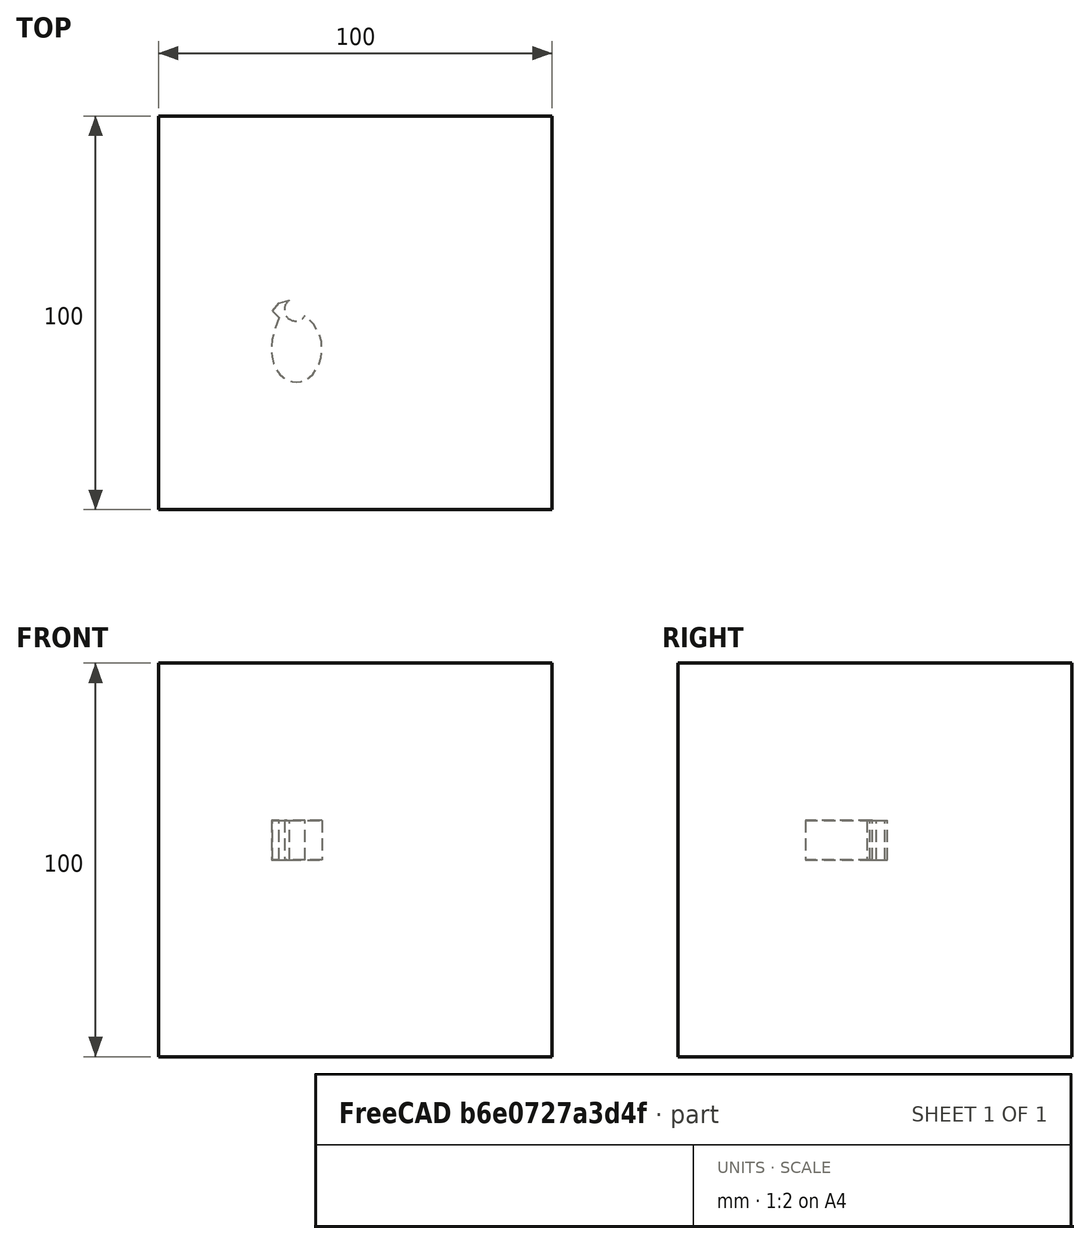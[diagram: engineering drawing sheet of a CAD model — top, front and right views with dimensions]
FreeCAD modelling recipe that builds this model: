
FCSTD DOCUMENT  (FreeCAD 0.19RUnknown)
Label: mirrorTest-1c
License: All rights reserved
LicenseURL: http://en.wikipedia.org/wiki/All_rights_reserved
objects: App::DocumentObjectGroupPython×1248, App::Part×2, Part::FeaturePython×1, Sketcher::SketchObject×1, Part::Extrusion×1, Part::Mirroring×1
note: 4 computed .brp shape members not serialized (recipe doc carries the construction recipe); baked Part::Feature solids carry a one-line shape summary decoded from their .brp

FEATURE [App::DocumentObjectGroupPython] HALFPI  # scripted group (container) (typed FeaturePython)
  name = HALFPI
  value = pi/2.
FEATURE [App::DocumentObjectGroupPython] PI  # scripted group (container) (typed FeaturePython)
  name = PI
  value = 1.*pi
FEATURE [App::DocumentObjectGroupPython] TWOPI  # scripted group (container) (typed FeaturePython)
  name = TWOPI
  value = 2.*pi
FEATURE [App::DocumentObjectGroupPython] Constants  # scripted group (container) (typed FeaturePython)
  Group = -> [HALFPI,PI,TWOPI]
FEATURE [App::DocumentObjectGroupPython] Variables  # scripted group (container) (typed FeaturePython)
FEATURE [App::DocumentObjectGroupPython] Quantities  # scripted group (container) (typed FeaturePython)
FEATURE [App::DocumentObjectGroupPython] Isotopes  # scripted group (container) (typed FeaturePython)
FEATURE [App::DocumentObjectGroupPython] Elements  # scripted group (container) (typed FeaturePython)
FEATURE [App::DocumentObjectGroupPython] G4Isotopes  # scripted group (container) (typed FeaturePython)
FEATURE [App::DocumentObjectGroupPython] H_element  # scripted group (container) (typed FeaturePython)
  Z = 1
  atom_value = 1.008
  formula = H
  name = H_element
FEATURE [App::DocumentObjectGroupPython] He_element  # scripted group (container) (typed FeaturePython)
  Z = 2
  atom_value = 4.0026
  formula = He
  name = He_element
FEATURE [App::DocumentObjectGroupPython] Li_element  # scripted group (container) (typed FeaturePython)
  Z = 3
  atom_value = 6.94
  formula = Li
  name = Li_element
FEATURE [App::DocumentObjectGroupPython] Be_element  # scripted group (container) (typed FeaturePython)
  Z = 4
  atom_value = 9.01218
  formula = Be
  name = Be_element
FEATURE [App::DocumentObjectGroupPython] B_element  # scripted group (container) (typed FeaturePython)
  Z = 5
  atom_value = 10.81
  formula = B
  name = B_element
FEATURE [App::DocumentObjectGroupPython] C_element  # scripted group (container) (typed FeaturePython)
  Z = 6
  atom_value = 12.011
  formula = C
  name = C_element
FEATURE [App::DocumentObjectGroupPython] N_element  # scripted group (container) (typed FeaturePython)
  Z = 7
  atom_value = 14.007
  formula = N
  name = N_element
FEATURE [App::DocumentObjectGroupPython] O_element  # scripted group (container) (typed FeaturePython)
  Z = 8
  atom_value = 15.999
  formula = O
  name = O_element
FEATURE [App::DocumentObjectGroupPython] F_element  # scripted group (container) (typed FeaturePython)
  Z = 9
  atom_value = 18.9984
  formula = F
  name = F_element
FEATURE [App::DocumentObjectGroupPython] Ne_element  # scripted group (container) (typed FeaturePython)
  Z = 10
  atom_value = 20.1797
  formula = Ne
  name = Ne_element
FEATURE [App::DocumentObjectGroupPython] Na_element  # scripted group (container) (typed FeaturePython)
  Z = 11
  atom_value = 22.9898
  formula = Na
  name = Na_element
FEATURE [App::DocumentObjectGroupPython] Mg_element  # scripted group (container) (typed FeaturePython)
  Z = 12
  atom_value = 24.305
  formula = Mg
  name = Mg_element
FEATURE [App::DocumentObjectGroupPython] Al_element  # scripted group (container) (typed FeaturePython)
  Z = 13
  atom_value = 26.9815
  formula = Al
  name = Al_element
FEATURE [App::DocumentObjectGroupPython] Si_element  # scripted group (container) (typed FeaturePython)
  Z = 14
  atom_value = 28.085
  formula = Si
  name = Si_element
FEATURE [App::DocumentObjectGroupPython] P_element  # scripted group (container) (typed FeaturePython)
  Z = 15
  atom_value = 30.9738
  formula = P
  name = P_element
FEATURE [App::DocumentObjectGroupPython] S_element  # scripted group (container) (typed FeaturePython)
  Z = 16
  atom_value = 32.06
  formula = S
  name = S_element
FEATURE [App::DocumentObjectGroupPython] Cl_element  # scripted group (container) (typed FeaturePython)
  Z = 17
  atom_value = 35.45
  formula = Cl
  name = Cl_element
FEATURE [App::DocumentObjectGroupPython] Ar_element  # scripted group (container) (typed FeaturePython)
  Z = 18
  atom_value = 39.95
  formula = Ar
  name = Ar_element
FEATURE [App::DocumentObjectGroupPython] K_element  # scripted group (container) (typed FeaturePython)
  Z = 19
  atom_value = 39.0983
  formula = K
  name = K_element
FEATURE [App::DocumentObjectGroupPython] Ca_element  # scripted group (container) (typed FeaturePython)
  Z = 20
  atom_value = 40.078
  formula = Ca
  name = Ca_element
FEATURE [App::DocumentObjectGroupPython] Sc_element  # scripted group (container) (typed FeaturePython)
  Z = 21
  atom_value = 44.9559
  formula = Sc
  name = Sc_element
FEATURE [App::DocumentObjectGroupPython] Ti_element  # scripted group (container) (typed FeaturePython)
  Z = 22
  atom_value = 47.867
  formula = Ti
  name = Ti_element
FEATURE [App::DocumentObjectGroupPython] V_element  # scripted group (container) (typed FeaturePython)
  Z = 23
  atom_value = 50.9415
  formula = V
  name = V_element
FEATURE [App::DocumentObjectGroupPython] Cr_element  # scripted group (container) (typed FeaturePython)
  Z = 24
  atom_value = 51.9961
  formula = Cr
  name = Cr_element
FEATURE [App::DocumentObjectGroupPython] Mn_element  # scripted group (container) (typed FeaturePython)
  Z = 25
  atom_value = 54.938
  formula = Mn
  name = Mn_element
FEATURE [App::DocumentObjectGroupPython] Fe_element  # scripted group (container) (typed FeaturePython)
  Z = 26
  atom_value = 55.845
  formula = Fe
  name = Fe_element
FEATURE [App::DocumentObjectGroupPython] Co_element  # scripted group (container) (typed FeaturePython)
  Z = 27
  atom_value = 58.9332
  formula = Co
  name = Co_element
FEATURE [App::DocumentObjectGroupPython] Ni_element  # scripted group (container) (typed FeaturePython)
  Z = 28
  atom_value = 58.6934
  formula = Ni
  name = Ni_element
FEATURE [App::DocumentObjectGroupPython] Cu_element  # scripted group (container) (typed FeaturePython)
  Z = 29
  atom_value = 63.546
  formula = Cu
  name = Cu_element
FEATURE [App::DocumentObjectGroupPython] Zn_element  # scripted group (container) (typed FeaturePython)
  Z = 30
  atom_value = 65.38
  formula = Zn
  name = Zn_element
FEATURE [App::DocumentObjectGroupPython] Ga_element  # scripted group (container) (typed FeaturePython)
  Z = 31
  atom_value = 69.723
  formula = Ga
  name = Ga_element
FEATURE [App::DocumentObjectGroupPython] Ge_element  # scripted group (container) (typed FeaturePython)
  Z = 32
  atom_value = 72.63
  formula = Ge
  name = Ge_element
FEATURE [App::DocumentObjectGroupPython] As_element  # scripted group (container) (typed FeaturePython)
  Z = 33
  atom_value = 74.9216
  formula = As
  name = As_element
FEATURE [App::DocumentObjectGroupPython] Se_element  # scripted group (container) (typed FeaturePython)
  Z = 34
  atom_value = 78.971
  formula = Se
  name = Se_element
FEATURE [App::DocumentObjectGroupPython] Br_element  # scripted group (container) (typed FeaturePython)
  Z = 35
  atom_value = 79.904
  formula = Br
  name = Br_element
FEATURE [App::DocumentObjectGroupPython] Kr_element  # scripted group (container) (typed FeaturePython)
  Z = 36
  atom_value = 83.798
  formula = Kr
  name = Kr_element
FEATURE [App::DocumentObjectGroupPython] Rb_element  # scripted group (container) (typed FeaturePython)
  Z = 37
  atom_value = 85.4678
  formula = Rb
  name = Rb_element
FEATURE [App::DocumentObjectGroupPython] Sr_element  # scripted group (container) (typed FeaturePython)
  Z = 38
  atom_value = 87.62
  formula = Sr
  name = Sr_element
FEATURE [App::DocumentObjectGroupPython] Y_element  # scripted group (container) (typed FeaturePython)
  Z = 39
  atom_value = 88.9058
  formula = Y
  name = Y_element
FEATURE [App::DocumentObjectGroupPython] Zr_element  # scripted group (container) (typed FeaturePython)
  Z = 40
  atom_value = 91.224
  formula = Zr
  name = Zr_element
FEATURE [App::DocumentObjectGroupPython] Nb_element  # scripted group (container) (typed FeaturePython)
  Z = 41
  atom_value = 92.9064
  formula = Nb
  name = Nb_element
FEATURE [App::DocumentObjectGroupPython] Mo_element  # scripted group (container) (typed FeaturePython)
  Z = 42
  atom_value = 95.95
  formula = Mo
  name = Mo_element
FEATURE [App::DocumentObjectGroupPython] Tc_element  # scripted group (container) (typed FeaturePython)
  Z = 43
  atom_value = 97
  formula = Tc
  name = Tc_element
FEATURE [App::DocumentObjectGroupPython] Ru_element  # scripted group (container) (typed FeaturePython)
  Z = 44
  atom_value = 101.07
  formula = Ru
  name = Ru_element
FEATURE [App::DocumentObjectGroupPython] Rh_element  # scripted group (container) (typed FeaturePython)
  Z = 45
  atom_value = 102.905
  formula = Rh
  name = Rh_element
FEATURE [App::DocumentObjectGroupPython] Pd_element  # scripted group (container) (typed FeaturePython)
  Z = 46
  atom_value = 106.42
  formula = Pd
  name = Pd_element
FEATURE [App::DocumentObjectGroupPython] Ag_element  # scripted group (container) (typed FeaturePython)
  Z = 47
  atom_value = 107.868
  formula = Ag
  name = Ag_element
FEATURE [App::DocumentObjectGroupPython] Cd_element  # scripted group (container) (typed FeaturePython)
  Z = 48
  atom_value = 112.414
  formula = Cd
  name = Cd_element
FEATURE [App::DocumentObjectGroupPython] In_element  # scripted group (container) (typed FeaturePython)
  Z = 49
  atom_value = 114.818
  formula = In
  name = In_element
FEATURE [App::DocumentObjectGroupPython] Sn_element  # scripted group (container) (typed FeaturePython)
  Z = 50
  atom_value = 118.71
  formula = Sn
  name = Sn_element
FEATURE [App::DocumentObjectGroupPython] Sb_element  # scripted group (container) (typed FeaturePython)
  Z = 51
  atom_value = 121.76
  formula = Sb
  name = Sb_element
FEATURE [App::DocumentObjectGroupPython] Te_element  # scripted group (container) (typed FeaturePython)
  Z = 52
  atom_value = 127.6
  formula = Te
  name = Te_element
FEATURE [App::DocumentObjectGroupPython] I_element  # scripted group (container) (typed FeaturePython)
  Z = 53
  atom_value = 126.904
  formula = I
  name = I_element
FEATURE [App::DocumentObjectGroupPython] Xe_element  # scripted group (container) (typed FeaturePython)
  Z = 54
  atom_value = 131.293
  formula = Xe
  name = Xe_element
FEATURE [App::DocumentObjectGroupPython] Cs_element  # scripted group (container) (typed FeaturePython)
  Z = 55
  atom_value = 132.905
  formula = Cs
  name = Cs_element
FEATURE [App::DocumentObjectGroupPython] Ba_element  # scripted group (container) (typed FeaturePython)
  Z = 56
  atom_value = 137.327
  formula = Ba
  name = Ba_element
FEATURE [App::DocumentObjectGroupPython] La_element  # scripted group (container) (typed FeaturePython)
  Z = 57
  atom_value = 138.905
  formula = La
  name = La_element
FEATURE [App::DocumentObjectGroupPython] Ce_element  # scripted group (container) (typed FeaturePython)
  Z = 58
  atom_value = 140.116
  formula = Ce
  name = Ce_element
FEATURE [App::DocumentObjectGroupPython] Pr_element  # scripted group (container) (typed FeaturePython)
  Z = 59
  atom_value = 140.908
  formula = Pr
  name = Pr_element
FEATURE [App::DocumentObjectGroupPython] Nd_element  # scripted group (container) (typed FeaturePython)
  Z = 60
  atom_value = 144.242
  formula = Nd
  name = Nd_element
FEATURE [App::DocumentObjectGroupPython] Pm_element  # scripted group (container) (typed FeaturePython)
  Z = 61
  atom_value = 145
  formula = Pm
  name = Pm_element
FEATURE [App::DocumentObjectGroupPython] Sm_element  # scripted group (container) (typed FeaturePython)
  Z = 62
  atom_value = 150.36
  formula = Sm
  name = Sm_element
FEATURE [App::DocumentObjectGroupPython] Eu_element  # scripted group (container) (typed FeaturePython)
  Z = 63
  atom_value = 151.964
  formula = Eu
  name = Eu_element
FEATURE [App::DocumentObjectGroupPython] Gd_element  # scripted group (container) (typed FeaturePython)
  Z = 64
  atom_value = 157.25
  formula = Gd
  name = Gd_element
FEATURE [App::DocumentObjectGroupPython] Tb_element  # scripted group (container) (typed FeaturePython)
  Z = 65
  atom_value = 158.925
  formula = Tb
  name = Tb_element
FEATURE [App::DocumentObjectGroupPython] Dy_element  # scripted group (container) (typed FeaturePython)
  Z = 66
  atom_value = 162.5
  formula = Dy
  name = Dy_element
FEATURE [App::DocumentObjectGroupPython] Ho_element  # scripted group (container) (typed FeaturePython)
  Z = 67
  atom_value = 164.93
  formula = Ho
  name = Ho_element
FEATURE [App::DocumentObjectGroupPython] Er_element  # scripted group (container) (typed FeaturePython)
  Z = 68
  atom_value = 167.259
  formula = Er
  name = Er_element
FEATURE [App::DocumentObjectGroupPython] Tm_element  # scripted group (container) (typed FeaturePython)
  Z = 69
  atom_value = 168.934
  formula = Tm
  name = Tm_element
FEATURE [App::DocumentObjectGroupPython] Yb_element  # scripted group (container) (typed FeaturePython)
  Z = 70
  atom_value = 173.045
  formula = Yb
  name = Yb_element
FEATURE [App::DocumentObjectGroupPython] Lu_element  # scripted group (container) (typed FeaturePython)
  Z = 71
  atom_value = 174.967
  formula = Lu
  name = Lu_element
FEATURE [App::DocumentObjectGroupPython] Hf_element  # scripted group (container) (typed FeaturePython)
  Z = 72
  atom_value = 178.49
  formula = Hf
  name = Hf_element
FEATURE [App::DocumentObjectGroupPython] Ta_element  # scripted group (container) (typed FeaturePython)
  Z = 73
  atom_value = 180.948
  formula = Ta
  name = Ta_element
FEATURE [App::DocumentObjectGroupPython] W_element  # scripted group (container) (typed FeaturePython)
  Z = 74
  atom_value = 183.84
  formula = W
  name = W_element
FEATURE [App::DocumentObjectGroupPython] Re_element  # scripted group (container) (typed FeaturePython)
  Z = 75
  atom_value = 186.207
  formula = Re
  name = Re_element
FEATURE [App::DocumentObjectGroupPython] Os_element  # scripted group (container) (typed FeaturePython)
  Z = 76
  atom_value = 190.23
  formula = Os
  name = Os_element
FEATURE [App::DocumentObjectGroupPython] Ir_element  # scripted group (container) (typed FeaturePython)
  Z = 77
  atom_value = 192.217
  formula = Ir
  name = Ir_element
FEATURE [App::DocumentObjectGroupPython] Pt_element  # scripted group (container) (typed FeaturePython)
  Z = 78
  atom_value = 195.084
  formula = Pt
  name = Pt_element
FEATURE [App::DocumentObjectGroupPython] Au_element  # scripted group (container) (typed FeaturePython)
  Z = 79
  atom_value = 196.967
  formula = Au
  name = Au_element
FEATURE [App::DocumentObjectGroupPython] Hg_element  # scripted group (container) (typed FeaturePython)
  Z = 80
  atom_value = 200.592
  formula = Hg
  name = Hg_element
FEATURE [App::DocumentObjectGroupPython] Tl_element  # scripted group (container) (typed FeaturePython)
  Z = 81
  atom_value = 204.38
  formula = Tl
  name = Tl_element
FEATURE [App::DocumentObjectGroupPython] Pb_element  # scripted group (container) (typed FeaturePython)
  Z = 82
  atom_value = 207.2
  formula = Pb
  name = Pb_element
FEATURE [App::DocumentObjectGroupPython] Bi_element  # scripted group (container) (typed FeaturePython)
  Z = 83
  atom_value = 208.98
  formula = Bi
  name = Bi_element
FEATURE [App::DocumentObjectGroupPython] Po_element  # scripted group (container) (typed FeaturePython)
  Z = 84
  atom_value = 209
  formula = Po
  name = Po_element
FEATURE [App::DocumentObjectGroupPython] At_element  # scripted group (container) (typed FeaturePython)
  Z = 85
  atom_value = 210
  formula = At
  name = At_element
FEATURE [App::DocumentObjectGroupPython] Rn_element  # scripted group (container) (typed FeaturePython)
  Z = 86
  atom_value = 222
  formula = Rn
  name = Rn_element
FEATURE [App::DocumentObjectGroupPython] Fr_element  # scripted group (container) (typed FeaturePython)
  Z = 87
  atom_value = 223
  formula = Fr
  name = Fr_element
FEATURE [App::DocumentObjectGroupPython] Ra_element  # scripted group (container) (typed FeaturePython)
  Z = 88
  atom_value = 226
  formula = Ra
  name = Ra_element
FEATURE [App::DocumentObjectGroupPython] Ac_element  # scripted group (container) (typed FeaturePython)
  Z = 89
  atom_value = 227
  formula = Ac
  name = Ac_element
FEATURE [App::DocumentObjectGroupPython] Th_element  # scripted group (container) (typed FeaturePython)
  Z = 90
  atom_value = 232.038
  formula = Th
  name = Th_element
FEATURE [App::DocumentObjectGroupPython] Pa_element  # scripted group (container) (typed FeaturePython)
  Z = 91
  atom_value = 231.036
  formula = Pa
  name = Pa_element
FEATURE [App::DocumentObjectGroupPython] U_element  # scripted group (container) (typed FeaturePython)
  Z = 92
  atom_value = 238.029
  formula = U
  name = U_element
FEATURE [App::DocumentObjectGroupPython] Np_element  # scripted group (container) (typed FeaturePython)
  Z = 93
  atom_value = 237
  formula = Np
  name = Np_element
FEATURE [App::DocumentObjectGroupPython] Pu_element  # scripted group (container) (typed FeaturePython)
  Z = 94
  atom_value = 244
  formula = Pu
  name = Pu_element
FEATURE [App::DocumentObjectGroupPython] Am_element  # scripted group (container) (typed FeaturePython)
  Z = 95
  atom_value = 243
  formula = Am
  name = Am_element
FEATURE [App::DocumentObjectGroupPython] Cm_element  # scripted group (container) (typed FeaturePython)
  Z = 96
  atom_value = 247
  formula = Cm
  name = Cm_element
FEATURE [App::DocumentObjectGroupPython] Bk_element  # scripted group (container) (typed FeaturePython)
  Z = 97
  atom_value = 247
  formula = Bk
  name = Bk_element
FEATURE [App::DocumentObjectGroupPython] Cf_element  # scripted group (container) (typed FeaturePython)
  Z = 98
  atom_value = 251
  formula = Cf
  name = Cf_element
FEATURE [App::DocumentObjectGroupPython] G4Elements  # scripted group (container) (typed FeaturePython)
  Group = -> [H_element,He_element,Li_element,Be_element,B_element,C_element,N_element,O_element,F_element,Ne_element,Na_element,Mg_element,Al_element,Si_element,P_element,S_element,Cl_element,Ar_element,K_element,Ca_element,Sc_element,Ti_element,V_element,Cr_element,Mn_element,Fe_element,Co_element,Ni_element,Cu_element,Zn_element,Ga_element,Ge_element,As_element,Se_element,Br_element,Kr_element,Rb_element,+61 more]
FEATURE [App::DocumentObjectGroupPython] H_element001  label="H_element : 0.101"  # scripted group (container) (typed FeaturePython)
  n = 0.101327
FEATURE [App::DocumentObjectGroupPython] C_element001  label="C_element : 0.775"  # scripted group (container) (typed FeaturePython)
  n = 0.7755
FEATURE [App::DocumentObjectGroupPython] N_element001  label="N_element : 0.035"  # scripted group (container) (typed FeaturePython)
  n = 0.035057
FEATURE [App::DocumentObjectGroupPython] O_element001  label="O_element : 0.052"  # scripted group (container) (typed FeaturePython)
  n = 0.0523159
FEATURE [App::DocumentObjectGroupPython] F_element001  label="F_element : 0.017"  # scripted group (container) (typed FeaturePython)
  n = 0.017422
FEATURE [App::DocumentObjectGroupPython] Ca_element001  label="Ca_element : 0.018"  # scripted group (container) (typed FeaturePython)
  n = 0.018378
FEATURE [App::DocumentObjectGroupPython] G4_A_150_TISSUE  label="G4_A-150_TISSUE"  # scripted group (container) (typed FeaturePython)
  Dunit = g/cm3
  Dvalue = 1.127
  Group = -> [H_element001,C_element001,N_element001,O_element001,F_element001,Ca_element001]
  conduct = 2
  density = 1
  expand = 3
  formula = G4_A-150_TISSUE
  name = G4_A-150_TISSUE
  specific = 4
FEATURE [App::DocumentObjectGroupPython] C_element002  label="C_element : 3"  # scripted group (container) (typed FeaturePython)
  n = 3
  ref = C_element
FEATURE [App::DocumentObjectGroupPython] H_element002  label="H_element : 6"  # scripted group (container) (typed FeaturePython)
  n = 6
  ref = H_element
FEATURE [App::DocumentObjectGroupPython] O_element002  label="O_element : 1"  # scripted group (container) (typed FeaturePython)
  n = 1
  ref = O_element
FEATURE [App::DocumentObjectGroupPython] G4_ACETONE  # scripted group (container) (typed FeaturePython)
  Dunit = g/cm3
  Dvalue = 0.7899
  Group = -> [C_element002,H_element002,O_element002]
  conduct = 2
  density = 1
  expand = 3
  formula = G4_ACETONE
  name = G4_ACETONE
  specific = 4
FEATURE [App::DocumentObjectGroupPython] C_element003  label="C_element : 2"  # scripted group (container) (typed FeaturePython)
  n = 2
  ref = C_element
FEATURE [App::DocumentObjectGroupPython] H_element003  label="H_element : 2"  # scripted group (container) (typed FeaturePython)
  n = 2
  ref = H_element
FEATURE [App::DocumentObjectGroupPython] G4_ACETYLENE  # scripted group (container) (typed FeaturePython)
  Dunit = g/cm3
  Dvalue = 0.0010967
  Group = -> [C_element003,H_element003]
  conduct = 2
  density = 1
  expand = 3
  formula = G4_ACETYLENE
  name = G4_ACETYLENE
  specific = 4
FEATURE [App::DocumentObjectGroupPython] C_element004  label="C_element : 5"  # scripted group (container) (typed FeaturePython)
  n = 5
  ref = C_element
FEATURE [App::DocumentObjectGroupPython] H_element004  label="H_element : 5"  # scripted group (container) (typed FeaturePython)
  n = 5
  ref = H_element
FEATURE [App::DocumentObjectGroupPython] N_element002  label="N_element : 5"  # scripted group (container) (typed FeaturePython)
  n = 5
  ref = N_element
FEATURE [App::DocumentObjectGroupPython] G4_ADENINE  # scripted group (container) (typed FeaturePython)
  Dunit = g/cm3
  Dvalue = 1.6
  Group = -> [C_element004,H_element004,N_element002]
  conduct = 2
  density = 1
  expand = 3
  formula = G4_ADENINE
  name = G4_ADENINE
  specific = 4
FEATURE [App::DocumentObjectGroupPython] H_element005  label="H_element : 0.114"  # scripted group (container) (typed FeaturePython)
  n = 0.114
FEATURE [App::DocumentObjectGroupPython] C_element005  label="C_element : 0.598"  # scripted group (container) (typed FeaturePython)
  n = 0.598
FEATURE [App::DocumentObjectGroupPython] N_element003  label="N_element : 0.007"  # scripted group (container) (typed FeaturePython)
  n = 0.007
FEATURE [App::DocumentObjectGroupPython] O_element003  label="O_element : 0.278"  # scripted group (container) (typed FeaturePython)
  n = 0.278
FEATURE [App::DocumentObjectGroupPython] Na_element001  label="Na_element : 0.001"  # scripted group (container) (typed FeaturePython)
  n = 0.001
FEATURE [App::DocumentObjectGroupPython] S_element001  label="S_element : 0.001"  # scripted group (container) (typed FeaturePython)
  n = 0.001
FEATURE [App::DocumentObjectGroupPython] Cl_element001  label="Cl_element : 0.001"  # scripted group (container) (typed FeaturePython)
  n = 0.001
FEATURE [App::DocumentObjectGroupPython] G4_ADIPOSE_TISSUE_ICRP  # scripted group (container) (typed FeaturePython)
  Dunit = g/cm3
  Dvalue = 0.95
  Group = -> [H_element005,C_element005,N_element003,O_element003,Na_element001,S_element001,Cl_element001]
  conduct = 2
  density = 1
  expand = 3
  formula = G4_ADIPOSE_TISSUE_ICRP
  name = G4_ADIPOSE_TISSUE_ICRP
  specific = 4
FEATURE [App::DocumentObjectGroupPython] C_element006  label="C_element : 0.000"  # scripted group (container) (typed FeaturePython)
  n = 0.000124
FEATURE [App::DocumentObjectGroupPython] N_element004  label="N_element : 0.755"  # scripted group (container) (typed FeaturePython)
  n = 0.755268
FEATURE [App::DocumentObjectGroupPython] O_element004  label="O_element : 0.232"  # scripted group (container) (typed FeaturePython)
  n = 0.231781
FEATURE [App::DocumentObjectGroupPython] Ar_element001  label="Ar_element : 0.013"  # scripted group (container) (typed FeaturePython)
  n = 0.012827
FEATURE [App::DocumentObjectGroupPython] G4_AIR  # scripted group (container) (typed FeaturePython)
  Dunit = g/cm3
  Dvalue = 0.00120479
  Group = -> [C_element006,N_element004,O_element004,Ar_element001]
  conduct = 2
  density = 1
  expand = 3
  formula = G4_AIR
  name = G4_AIR
  specific = 4
FEATURE [App::DocumentObjectGroupPython] C_element007  label="C_element : 006"  # scripted group (container) (typed FeaturePython)
  n = 3
  ref = C_element
FEATURE [App::DocumentObjectGroupPython] H_element006  label="H_element : 7"  # scripted group (container) (typed FeaturePython)
  n = 7
  ref = H_element
FEATURE [App::DocumentObjectGroupPython] N_element005  label="N_element : 1"  # scripted group (container) (typed FeaturePython)
  n = 1
  ref = N_element
FEATURE [App::DocumentObjectGroupPython] O_element005  label="O_element : 2"  # scripted group (container) (typed FeaturePython)
  n = 2
  ref = O_element
FEATURE [App::DocumentObjectGroupPython] G4_ALANINE  # scripted group (container) (typed FeaturePython)
  Dunit = g/cm3
  Dvalue = 1.42
  Group = -> [C_element007,H_element006,N_element005,O_element005]
  conduct = 2
  density = 1
  expand = 3
  formula = G4_ALANINE
  name = G4_ALANINE
  specific = 4
FEATURE [App::DocumentObjectGroupPython] Al_element001  label="Al_element : 2"  # scripted group (container) (typed FeaturePython)
  n = 2
  ref = Al_element
FEATURE [App::DocumentObjectGroupPython] O_element006  label="O_element : 3"  # scripted group (container) (typed FeaturePython)
  n = 3
  ref = O_element
FEATURE [App::DocumentObjectGroupPython] G4_ALUMINUM_OXIDE  # scripted group (container) (typed FeaturePython)
  Dunit = g/cm3
  Dvalue = 3.97
  Group = -> [Al_element001,O_element006]
  conduct = 2
  density = 1
  expand = 3
  formula = G4_ALUMINUM_OXIDE
  name = G4_ALUMINUM_OXIDE
  specific = 4
FEATURE [App::DocumentObjectGroupPython] H_element007  label="H_element : 0.106"  # scripted group (container) (typed FeaturePython)
  n = 0.10593
FEATURE [App::DocumentObjectGroupPython] C_element008  label="C_element : 0.789"  # scripted group (container) (typed FeaturePython)
  n = 0.788974
FEATURE [App::DocumentObjectGroupPython] O_element007  label="O_element : 0.105"  # scripted group (container) (typed FeaturePython)
  n = 0.105096
FEATURE [App::DocumentObjectGroupPython] G4_AMBER  # scripted group (container) (typed FeaturePython)
  Dunit = g/cm3
  Dvalue = 1.1
  Group = -> [H_element007,C_element008,O_element007]
  conduct = 2
  density = 1
  expand = 3
  formula = G4_AMBER
  name = G4_AMBER
  specific = 4
FEATURE [App::DocumentObjectGroupPython] N_element006  label="N_element : 006"  # scripted group (container) (typed FeaturePython)
  n = 1
  ref = N_element
FEATURE [App::DocumentObjectGroupPython] H_element008  label="H_element : 3"  # scripted group (container) (typed FeaturePython)
  n = 3
  ref = H_element
FEATURE [App::DocumentObjectGroupPython] G4_AMMONIA  # scripted group (container) (typed FeaturePython)
  Dunit = g/cm3
  Dvalue = 0.000826019
  Group = -> [N_element006,H_element008]
  conduct = 2
  density = 1
  expand = 3
  formula = G4_AMMONIA
  name = G4_AMMONIA
  specific = 4
FEATURE [App::DocumentObjectGroupPython] C_element009  label="C_element : 6"  # scripted group (container) (typed FeaturePython)
  n = 6
  ref = C_element
FEATURE [App::DocumentObjectGroupPython] H_element009  label="H_element : 008"  # scripted group (container) (typed FeaturePython)
  n = 7
  ref = H_element
FEATURE [App::DocumentObjectGroupPython] N_element007  label="N_element : 007"  # scripted group (container) (typed FeaturePython)
  n = 1
  ref = N_element
FEATURE [App::DocumentObjectGroupPython] G4_ANILINE  # scripted group (container) (typed FeaturePython)
  Dunit = g/cm3
  Dvalue = 1.0235
  Group = -> [C_element009,H_element009,N_element007]
  conduct = 2
  density = 1
  expand = 3
  formula = G4_ANILINE
  name = G4_ANILINE
  specific = 4
FEATURE [App::DocumentObjectGroupPython] C_element010  label="C_element : 14"  # scripted group (container) (typed FeaturePython)
  n = 14
  ref = C_element
FEATURE [App::DocumentObjectGroupPython] H_element010  label="H_element : 10"  # scripted group (container) (typed FeaturePython)
  n = 10
  ref = H_element
FEATURE [App::DocumentObjectGroupPython] G4_ANTHRACENE  # scripted group (container) (typed FeaturePython)
  Dunit = g/cm3
  Dvalue = 1.283
  Group = -> [C_element010,H_element010]
  conduct = 2
  density = 1
  expand = 3
  formula = G4_ANTHRACENE
  name = G4_ANTHRACENE
  specific = 4
FEATURE [App::DocumentObjectGroupPython] H_element011  label="H_element : 0.065"  # scripted group (container) (typed FeaturePython)
  n = 0.0654709
FEATURE [App::DocumentObjectGroupPython] C_element011  label="C_element : 0.537"  # scripted group (container) (typed FeaturePython)
  n = 0.536944
FEATURE [App::DocumentObjectGroupPython] N_element008  label="N_element : 0.021"  # scripted group (container) (typed FeaturePython)
  n = 0.0215
FEATURE [App::DocumentObjectGroupPython] O_element008  label="O_element : 0.032"  # scripted group (container) (typed FeaturePython)
  n = 0.032085
FEATURE [App::DocumentObjectGroupPython] F_element002  label="F_element : 0.167"  # scripted group (container) (typed FeaturePython)
  n = 0.167411
FEATURE [App::DocumentObjectGroupPython] Ca_element002  label="Ca_element : 0.177"  # scripted group (container) (typed FeaturePython)
  n = 0.176589
FEATURE [App::DocumentObjectGroupPython] G4_B_100_BONE  label="G4_B-100_BONE"  # scripted group (container) (typed FeaturePython)
  Dunit = g/cm3
  Dvalue = 1.45
  Group = -> [H_element011,C_element011,N_element008,O_element008,F_element002,Ca_element002]
  conduct = 2
  density = 1
  expand = 3
  formula = G4_B-100_BONE
  name = G4_B-100_BONE
  specific = 4
FEATURE [App::DocumentObjectGroupPython] H_element012  label="H_element : 0.057"  # scripted group (container) (typed FeaturePython)
  n = 0.057441
FEATURE [App::DocumentObjectGroupPython] C_element012  label="C_element : 0.790"  # scripted group (container) (typed FeaturePython)
  n = 0.774591
FEATURE [App::DocumentObjectGroupPython] O_element009  label="O_element : 0.168"  # scripted group (container) (typed FeaturePython)
  n = 0.167968
FEATURE [App::DocumentObjectGroupPython] G4_BAKELITE  # scripted group (container) (typed FeaturePython)
  Dunit = g/cm3
  Dvalue = 1.25
  Group = -> [H_element012,C_element012,O_element009]
  conduct = 2
  density = 1
  expand = 3
  formula = G4_BAKELITE
  name = G4_BAKELITE
  specific = 4
FEATURE [App::DocumentObjectGroupPython] Ba_element001  label="Ba_element : 1"  # scripted group (container) (typed FeaturePython)
  n = 1
  ref = Ba_element
FEATURE [App::DocumentObjectGroupPython] F_element003  label="F_element : 2"  # scripted group (container) (typed FeaturePython)
  n = 2
  ref = F_element
FEATURE [App::DocumentObjectGroupPython] G4_BARIUM_FLUORIDE  # scripted group (container) (typed FeaturePython)
  Dunit = g/cm3
  Dvalue = 4.89
  Group = -> [Ba_element001,F_element003]
  conduct = 2
  density = 1
  expand = 3
  formula = G4_BARIUM_FLUORIDE
  name = G4_BARIUM_FLUORIDE
  specific = 4
FEATURE [App::DocumentObjectGroupPython] Ba_element002  label="Ba_element : 002"  # scripted group (container) (typed FeaturePython)
  n = 1
  ref = Ba_element
FEATURE [App::DocumentObjectGroupPython] S_element002  label="S_element : 1"  # scripted group (container) (typed FeaturePython)
  n = 1
  ref = S_element
FEATURE [App::DocumentObjectGroupPython] O_element010  label="O_element : 4"  # scripted group (container) (typed FeaturePython)
  n = 4
  ref = O_element
FEATURE [App::DocumentObjectGroupPython] G4_BARIUM_SULFATE  # scripted group (container) (typed FeaturePython)
  Dunit = g/cm3
  Dvalue = 4.5
  Group = -> [Ba_element002,S_element002,O_element010]
  conduct = 2
  density = 1
  expand = 3
  formula = G4_BARIUM_SULFATE
  name = G4_BARIUM_SULFATE
  specific = 4
FEATURE [App::DocumentObjectGroupPython] C_element013  label="C_element : 007"  # scripted group (container) (typed FeaturePython)
  n = 6
  ref = C_element
FEATURE [App::DocumentObjectGroupPython] H_element013  label="H_element : 009"  # scripted group (container) (typed FeaturePython)
  n = 6
  ref = H_element
FEATURE [App::DocumentObjectGroupPython] G4_BENZENE  # scripted group (container) (typed FeaturePython)
  Dunit = g/cm3
  Dvalue = 0.87865
  Group = -> [C_element013,H_element013]
  conduct = 2
  density = 1
  expand = 3
  formula = G4_BENZENE
  name = G4_BENZENE
  specific = 4
FEATURE [App::DocumentObjectGroupPython] Be_element001  label="Be_element : 1"  # scripted group (container) (typed FeaturePython)
  n = 1
  ref = Be_element
FEATURE [App::DocumentObjectGroupPython] O_element011  label="O_element : 005"  # scripted group (container) (typed FeaturePython)
  n = 1
  ref = O_element
FEATURE [App::DocumentObjectGroupPython] G4_BERYLLIUM_OXIDE  # scripted group (container) (typed FeaturePython)
  Dunit = g/cm3
  Dvalue = 3.01
  Group = -> [Be_element001,O_element011]
  conduct = 2
  density = 1
  expand = 3
  formula = G4_BERYLLIUM_OXIDE
  name = G4_BERYLLIUM_OXIDE
  specific = 4
FEATURE [App::DocumentObjectGroupPython] Bi_element001  label="Bi_element : 4"  # scripted group (container) (typed FeaturePython)
  n = 4
  ref = Bi_element
FEATURE [App::DocumentObjectGroupPython] Ge_element001  label="Ge_element : 3"  # scripted group (container) (typed FeaturePython)
  n = 3
  ref = Ge_element
FEATURE [App::DocumentObjectGroupPython] O_element012  label="O_element : 12"  # scripted group (container) (typed FeaturePython)
  n = 12
  ref = O_element
FEATURE [App::DocumentObjectGroupPython] G4_BGO  # scripted group (container) (typed FeaturePython)
  Dunit = g/cm3
  Dvalue = 7.13
  Group = -> [Bi_element001,Ge_element001,O_element012]
  conduct = 2
  density = 1
  expand = 3
  formula = G4_BGO
  name = G4_BGO
  specific = 4
FEATURE [App::DocumentObjectGroupPython] H_element014  label="H_element : 0.102"  # scripted group (container) (typed FeaturePython)
  n = 0.102
FEATURE [App::DocumentObjectGroupPython] C_element014  label="C_element : 0.110"  # scripted group (container) (typed FeaturePython)
  n = 0.11
FEATURE [App::DocumentObjectGroupPython] N_element009  label="N_element : 0.033"  # scripted group (container) (typed FeaturePython)
  n = 0.033
FEATURE [App::DocumentObjectGroupPython] O_element013  label="O_element : 0.745"  # scripted group (container) (typed FeaturePython)
  n = 0.745
FEATURE [App::DocumentObjectGroupPython] Na_element002  label="Na_element : 0.002"  # scripted group (container) (typed FeaturePython)
  n = 0.001
FEATURE [App::DocumentObjectGroupPython] P_element001  label="P_element : 0.001"  # scripted group (container) (typed FeaturePython)
  n = 0.001
FEATURE [App::DocumentObjectGroupPython] S_element003  label="S_element : 0.002"  # scripted group (container) (typed FeaturePython)
  n = 0.002
FEATURE [App::DocumentObjectGroupPython] Cl_element002  label="Cl_element : 0.003"  # scripted group (container) (typed FeaturePython)
  n = 0.003
FEATURE [App::DocumentObjectGroupPython] K_element001  label="K_element : 0.002"  # scripted group (container) (typed FeaturePython)
  n = 0.002
FEATURE [App::DocumentObjectGroupPython] Fe_element001  label="Fe_element : 0.001"  # scripted group (container) (typed FeaturePython)
  n = 0.001
FEATURE [App::DocumentObjectGroupPython] G4_BLOOD_ICRP  # scripted group (container) (typed FeaturePython)
  Dunit = g/cm3
  Dvalue = 1.06
  Group = -> [H_element014,C_element014,N_element009,O_element013,Na_element002,P_element001,S_element003,Cl_element002,K_element001,Fe_element001]
  conduct = 2
  density = 1
  expand = 3
  formula = G4_BLOOD_ICRP
  name = G4_BLOOD_ICRP
  specific = 4
FEATURE [App::DocumentObjectGroupPython] H_element015  label="H_element : 0.064"  # scripted group (container) (typed FeaturePython)
  n = 0.064
FEATURE [App::DocumentObjectGroupPython] C_element015  label="C_element : 0.278"  # scripted group (container) (typed FeaturePython)
  n = 0.278
FEATURE [App::DocumentObjectGroupPython] N_element010  label="N_element : 0.027"  # scripted group (container) (typed FeaturePython)
  n = 0.027
FEATURE [App::DocumentObjectGroupPython] O_element014  label="O_element : 0.410"  # scripted group (container) (typed FeaturePython)
  n = 0.41
FEATURE [App::DocumentObjectGroupPython] Mg_element001  label="Mg_element : 0.002"  # scripted group (container) (typed FeaturePython)
  n = 0.002
FEATURE [App::DocumentObjectGroupPython] P_element002  label="P_element : 0.070"  # scripted group (container) (typed FeaturePython)
  n = 0.07
FEATURE [App::DocumentObjectGroupPython] S_element004  label="S_element : 0.003"  # scripted group (container) (typed FeaturePython)
  n = 0.002
FEATURE [App::DocumentObjectGroupPython] Ca_element003  label="Ca_element : 0.147"  # scripted group (container) (typed FeaturePython)
  n = 0.147
FEATURE [App::DocumentObjectGroupPython] G4_BONE_COMPACT_ICRU  # scripted group (container) (typed FeaturePython)
  Dunit = g/cm3
  Dvalue = 1.85
  Group = -> [H_element015,C_element015,N_element010,O_element014,Mg_element001,P_element002,S_element004,Ca_element003]
  conduct = 2
  density = 1
  expand = 3
  formula = G4_BONE_COMPACT_ICRU
  name = G4_BONE_COMPACT_ICRU
  specific = 4
FEATURE [App::DocumentObjectGroupPython] H_element016  label="H_element : 0.034"  # scripted group (container) (typed FeaturePython)
  n = 0.034
FEATURE [App::DocumentObjectGroupPython] C_element016  label="C_element : 0.155"  # scripted group (container) (typed FeaturePython)
  n = 0.155
FEATURE [App::DocumentObjectGroupPython] N_element011  label="N_element : 0.042"  # scripted group (container) (typed FeaturePython)
  n = 0.042
FEATURE [App::DocumentObjectGroupPython] O_element015  label="O_element : 0.435"  # scripted group (container) (typed FeaturePython)
  n = 0.435
FEATURE [App::DocumentObjectGroupPython] Na_element003  label="Na_element : 0.003"  # scripted group (container) (typed FeaturePython)
  n = 0.001
FEATURE [App::DocumentObjectGroupPython] Mg_element002  label="Mg_element : 0.003"  # scripted group (container) (typed FeaturePython)
  n = 0.002
FEATURE [App::DocumentObjectGroupPython] P_element003  label="P_element : 0.103"  # scripted group (container) (typed FeaturePython)
  n = 0.103
FEATURE [App::DocumentObjectGroupPython] S_element005  label="S_element : 0.004"  # scripted group (container) (typed FeaturePython)
  n = 0.003
FEATURE [App::DocumentObjectGroupPython] Ca_element004  label="Ca_element : 0.225"  # scripted group (container) (typed FeaturePython)
  n = 0.225
FEATURE [App::DocumentObjectGroupPython] G4_BONE_CORTICAL_ICRP  # scripted group (container) (typed FeaturePython)
  Dunit = g/cm3
  Dvalue = 1.92
  Group = -> [H_element016,C_element016,N_element011,O_element015,Na_element003,Mg_element002,P_element003,S_element005,Ca_element004]
  conduct = 2
  density = 1
  expand = 3
  formula = G4_BONE_CORTICAL_ICRP
  name = G4_BONE_CORTICAL_ICRP
  specific = 4
FEATURE [App::DocumentObjectGroupPython] B_element001  label="B_element : 4"  # scripted group (container) (typed FeaturePython)
  n = 4
  ref = B_element
FEATURE [App::DocumentObjectGroupPython] C_element017  label="C_element : 1"  # scripted group (container) (typed FeaturePython)
  n = 1
  ref = C_element
FEATURE [App::DocumentObjectGroupPython] G4_BORON_CARBIDE  # scripted group (container) (typed FeaturePython)
  Dunit = g/cm3
  Dvalue = 2.52
  Group = -> [B_element001,C_element017]
  conduct = 2
  density = 1
  expand = 3
  formula = G4_BORON_CARBIDE
  name = G4_BORON_CARBIDE
  specific = 4
FEATURE [App::DocumentObjectGroupPython] B_element002  label="B_element : 2"  # scripted group (container) (typed FeaturePython)
  n = 2
  ref = B_element
FEATURE [App::DocumentObjectGroupPython] O_element016  label="O_element : 006"  # scripted group (container) (typed FeaturePython)
  n = 3
  ref = O_element
FEATURE [App::DocumentObjectGroupPython] G4_BORON_OXIDE  # scripted group (container) (typed FeaturePython)
  Dunit = g/cm3
  Dvalue = 1.812
  Group = -> [B_element002,O_element016]
  conduct = 2
  density = 1
  expand = 3
  formula = G4_BORON_OXIDE
  name = G4_BORON_OXIDE
  specific = 4
FEATURE [App::DocumentObjectGroupPython] H_element017  label="H_element : 0.107"  # scripted group (container) (typed FeaturePython)
  n = 0.107
FEATURE [App::DocumentObjectGroupPython] C_element018  label="C_element : 0.145"  # scripted group (container) (typed FeaturePython)
  n = 0.145
FEATURE [App::DocumentObjectGroupPython] N_element012  label="N_element : 0.022"  # scripted group (container) (typed FeaturePython)
  n = 0.022
FEATURE [App::DocumentObjectGroupPython] O_element017  label="O_element : 0.712"  # scripted group (container) (typed FeaturePython)
  n = 0.712
FEATURE [App::DocumentObjectGroupPython] Na_element004  label="Na_element : 0.004"  # scripted group (container) (typed FeaturePython)
  n = 0.002
FEATURE [App::DocumentObjectGroupPython] P_element004  label="P_element : 0.004"  # scripted group (container) (typed FeaturePython)
  n = 0.004
FEATURE [App::DocumentObjectGroupPython] S_element006  label="S_element : 0.005"  # scripted group (container) (typed FeaturePython)
  n = 0.002
FEATURE [App::DocumentObjectGroupPython] Cl_element003  label="Cl_element : 0.004"  # scripted group (container) (typed FeaturePython)
  n = 0.003
FEATURE [App::DocumentObjectGroupPython] K_element002  label="K_element : 0.003"  # scripted group (container) (typed FeaturePython)
  n = 0.003
FEATURE [App::DocumentObjectGroupPython] G4_BRAIN_ICRP  # scripted group (container) (typed FeaturePython)
  Dunit = g/cm3
  Dvalue = 1.04
  Group = -> [H_element017,C_element018,N_element012,O_element017,Na_element004,P_element004,S_element006,Cl_element003,K_element002]
  conduct = 2
  density = 1
  expand = 3
  formula = G4_BRAIN_ICRP
  name = G4_BRAIN_ICRP
  specific = 4
FEATURE [App::DocumentObjectGroupPython] C_element019  label="C_element : 4"  # scripted group (container) (typed FeaturePython)
  n = 4
  ref = C_element
FEATURE [App::DocumentObjectGroupPython] H_element018  label="H_element : 010"  # scripted group (container) (typed FeaturePython)
  n = 10
  ref = H_element
FEATURE [App::DocumentObjectGroupPython] G4_BUTANE  # scripted group (container) (typed FeaturePython)
  Dunit = g/cm3
  Dvalue = 0.00249343
  Group = -> [C_element019,H_element018]
  conduct = 2
  density = 1
  expand = 3
  formula = G4_BUTANE
  name = G4_BUTANE
  specific = 4
FEATURE [App::DocumentObjectGroupPython] C_element020  label="C_element : 008"  # scripted group (container) (typed FeaturePython)
  n = 4
  ref = C_element
FEATURE [App::DocumentObjectGroupPython] H_element019  label="H_element : 011"  # scripted group (container) (typed FeaturePython)
  n = 10
  ref = H_element
FEATURE [App::DocumentObjectGroupPython] O_element018  label="O_element : 007"  # scripted group (container) (typed FeaturePython)
  n = 1
  ref = O_element
FEATURE [App::DocumentObjectGroupPython] G4_N_BUTYL_ALCOHOL  label="G4_N-BUTYL_ALCOHOL"  # scripted group (container) (typed FeaturePython)
  Dunit = g/cm3
  Dvalue = 0.8098
  Group = -> [C_element020,H_element019,O_element018]
  conduct = 2
  density = 1
  expand = 3
  formula = G4_N-BUTYL_ALCOHOL
  name = G4_N-BUTYL_ALCOHOL
  specific = 4
FEATURE [App::DocumentObjectGroupPython] H_element020  label="H_element : 0.025"  # scripted group (container) (typed FeaturePython)
  n = 0.02468
FEATURE [App::DocumentObjectGroupPython] C_element021  label="C_element : 0.502"  # scripted group (container) (typed FeaturePython)
  n = 0.501611
FEATURE [App::DocumentObjectGroupPython] O_element019  label="O_element : 0.005"  # scripted group (container) (typed FeaturePython)
  n = 0.004527
FEATURE [App::DocumentObjectGroupPython] F_element004  label="F_element : 0.465"  # scripted group (container) (typed FeaturePython)
  n = 0.465209
FEATURE [App::DocumentObjectGroupPython] Si_element001  label="Si_element : 0.004"  # scripted group (container) (typed FeaturePython)
  n = 0.003973
FEATURE [App::DocumentObjectGroupPython] G4_C_552  label="G4_C-552"  # scripted group (container) (typed FeaturePython)
  Dunit = g/cm3
  Dvalue = 1.76
  Group = -> [H_element020,C_element021,O_element019,F_element004,Si_element001]
  conduct = 2
  density = 1
  expand = 3
  formula = G4_C-552
  name = G4_C-552
  specific = 4
FEATURE [App::DocumentObjectGroupPython] Cd_element001  label="Cd_element : 1"  # scripted group (container) (typed FeaturePython)
  n = 1
  ref = Cd_element
FEATURE [App::DocumentObjectGroupPython] Te_element001  label="Te_element : 1"  # scripted group (container) (typed FeaturePython)
  n = 1
  ref = Te_element
FEATURE [App::DocumentObjectGroupPython] G4_CADMIUM_TELLURIDE  # scripted group (container) (typed FeaturePython)
  Dunit = g/cm3
  Dvalue = 6.2
  Group = -> [Cd_element001,Te_element001]
  conduct = 2
  density = 1
  expand = 3
  formula = G4_CADMIUM_TELLURIDE
  name = G4_CADMIUM_TELLURIDE
  specific = 4
FEATURE [App::DocumentObjectGroupPython] Cd_element002  label="Cd_element : 002"  # scripted group (container) (typed FeaturePython)
  n = 1
  ref = Cd_element
FEATURE [App::DocumentObjectGroupPython] W_element001  label="W_element : 1"  # scripted group (container) (typed FeaturePython)
  n = 1
  ref = W_element
FEATURE [App::DocumentObjectGroupPython] O_element020  label="O_element : 008"  # scripted group (container) (typed FeaturePython)
  n = 4
  ref = O_element
FEATURE [App::DocumentObjectGroupPython] G4_CADMIUM_TUNGSTATE  # scripted group (container) (typed FeaturePython)
  Dunit = g/cm3
  Dvalue = 7.9
  Group = -> [Cd_element002,W_element001,O_element020]
  conduct = 2
  density = 1
  expand = 3
  formula = G4_CADMIUM_TUNGSTATE
  name = G4_CADMIUM_TUNGSTATE
  specific = 4
FEATURE [App::DocumentObjectGroupPython] Ca_element005  label="Ca_element : 1"  # scripted group (container) (typed FeaturePython)
  n = 1
  ref = Ca_element
FEATURE [App::DocumentObjectGroupPython] C_element022  label="C_element : 009"  # scripted group (container) (typed FeaturePython)
  n = 1
  ref = C_element
FEATURE [App::DocumentObjectGroupPython] O_element021  label="O_element : 009"  # scripted group (container) (typed FeaturePython)
  n = 3
  ref = O_element
FEATURE [App::DocumentObjectGroupPython] G4_CALCIUM_CARBONATE  # scripted group (container) (typed FeaturePython)
  Dunit = g/cm3
  Dvalue = 2.8
  Group = -> [Ca_element005,C_element022,O_element021]
  conduct = 2
  density = 1
  expand = 3
  formula = G4_CALCIUM_CARBONATE
  name = G4_CALCIUM_CARBONATE
  specific = 4
FEATURE [App::DocumentObjectGroupPython] Ca_element006  label="Ca_element : 002"  # scripted group (container) (typed FeaturePython)
  n = 1
  ref = Ca_element
FEATURE [App::DocumentObjectGroupPython] F_element005  label="F_element : 003"  # scripted group (container) (typed FeaturePython)
  n = 2
  ref = F_element
FEATURE [App::DocumentObjectGroupPython] G4_CALCIUM_FLUORIDE  # scripted group (container) (typed FeaturePython)
  Dunit = g/cm3
  Dvalue = 3.18
  Group = -> [Ca_element006,F_element005]
  conduct = 2
  density = 1
  expand = 3
  formula = G4_CALCIUM_FLUORIDE
  name = G4_CALCIUM_FLUORIDE
  specific = 4
FEATURE [App::DocumentObjectGroupPython] Ca_element007  label="Ca_element : 003"  # scripted group (container) (typed FeaturePython)
  n = 1
  ref = Ca_element
FEATURE [App::DocumentObjectGroupPython] O_element022  label="O_element : 010"  # scripted group (container) (typed FeaturePython)
  n = 1
  ref = O_element
FEATURE [App::DocumentObjectGroupPython] G4_CALCIUM_OXIDE  # scripted group (container) (typed FeaturePython)
  Dunit = g/cm3
  Dvalue = 3.3
  Group = -> [Ca_element007,O_element022]
  conduct = 2
  density = 1
  expand = 3
  formula = G4_CALCIUM_OXIDE
  name = G4_CALCIUM_OXIDE
  specific = 4
FEATURE [App::DocumentObjectGroupPython] Ca_element008  label="Ca_element : 004"  # scripted group (container) (typed FeaturePython)
  n = 1
  ref = Ca_element
FEATURE [App::DocumentObjectGroupPython] S_element007  label="S_element : 002"  # scripted group (container) (typed FeaturePython)
  n = 1
  ref = S_element
FEATURE [App::DocumentObjectGroupPython] O_element023  label="O_element : 011"  # scripted group (container) (typed FeaturePython)
  n = 4
  ref = O_element
FEATURE [App::DocumentObjectGroupPython] G4_CALCIUM_SULFATE  # scripted group (container) (typed FeaturePython)
  Dunit = g/cm3
  Dvalue = 2.96
  Group = -> [Ca_element008,S_element007,O_element023]
  conduct = 2
  density = 1
  expand = 3
  formula = G4_CALCIUM_SULFATE
  name = G4_CALCIUM_SULFATE
  specific = 4
FEATURE [App::DocumentObjectGroupPython] Ca_element009  label="Ca_element : 005"  # scripted group (container) (typed FeaturePython)
  n = 1
  ref = Ca_element
FEATURE [App::DocumentObjectGroupPython] W_element002  label="W_element : 002"  # scripted group (container) (typed FeaturePython)
  n = 1
  ref = W_element
FEATURE [App::DocumentObjectGroupPython] O_element024  label="O_element : 012"  # scripted group (container) (typed FeaturePython)
  n = 4
  ref = O_element
FEATURE [App::DocumentObjectGroupPython] G4_CALCIUM_TUNGSTATE  # scripted group (container) (typed FeaturePython)
  Dunit = g/cm3
  Dvalue = 6.062
  Group = -> [Ca_element009,W_element002,O_element024]
  conduct = 2
  density = 1
  expand = 3
  formula = G4_CALCIUM_TUNGSTATE
  name = G4_CALCIUM_TUNGSTATE
  specific = 4
FEATURE [App::DocumentObjectGroupPython] C_element023  label="C_element : 010"  # scripted group (container) (typed FeaturePython)
  n = 1
  ref = C_element
FEATURE [App::DocumentObjectGroupPython] O_element025  label="O_element : 013"  # scripted group (container) (typed FeaturePython)
  n = 2
  ref = O_element
FEATURE [App::DocumentObjectGroupPython] G4_CARBON_DIOXIDE  # scripted group (container) (typed FeaturePython)
  Dunit = g/cm3
  Dvalue = 0.00184212
  Group = -> [C_element023,O_element025]
  conduct = 2
  density = 1
  expand = 3
  formula = G4_CARBON_DIOXIDE
  name = G4_CARBON_DIOXIDE
  specific = 4
FEATURE [App::DocumentObjectGroupPython] C_element024  label="C_element : 011"  # scripted group (container) (typed FeaturePython)
  n = 1
  ref = C_element
FEATURE [App::DocumentObjectGroupPython] Cl_element004  label="Cl_element : 4"  # scripted group (container) (typed FeaturePython)
  n = 4
  ref = Cl_element
FEATURE [App::DocumentObjectGroupPython] G4_CARBON_TETRACHLORIDE  # scripted group (container) (typed FeaturePython)
  Dunit = g/cm3
  Dvalue = 1.594
  Group = -> [C_element024,Cl_element004]
  conduct = 2
  density = 1
  expand = 3
  formula = G4_CARBON_TETRACHLORIDE
  name = G4_CARBON_TETRACHLORIDE
  specific = 4
FEATURE [App::DocumentObjectGroupPython] C_element025  label="C_element : 012"  # scripted group (container) (typed FeaturePython)
  n = 6
  ref = C_element
FEATURE [App::DocumentObjectGroupPython] H_element021  label="H_element : 012"  # scripted group (container) (typed FeaturePython)
  n = 10
  ref = H_element
FEATURE [App::DocumentObjectGroupPython] O_element026  label="O_element : 5"  # scripted group (container) (typed FeaturePython)
  n = 5
  ref = O_element
FEATURE [App::DocumentObjectGroupPython] G4_CELLULOSE_CELLOPHANE  # scripted group (container) (typed FeaturePython)
  Dunit = g/cm3
  Dvalue = 1.42
  Group = -> [C_element025,H_element021,O_element026]
  conduct = 2
  density = 1
  expand = 3
  formula = G4_CELLULOSE_CELLOPHANE
  name = G4_CELLULOSE_CELLOPHANE
  specific = 4
FEATURE [App::DocumentObjectGroupPython] H_element022  label="H_element : 0.067"  # scripted group (container) (typed FeaturePython)
  n = 0.067125
FEATURE [App::DocumentObjectGroupPython] C_element026  label="C_element : 0.545"  # scripted group (container) (typed FeaturePython)
  n = 0.545403
FEATURE [App::DocumentObjectGroupPython] O_element027  label="O_element : 0.387"  # scripted group (container) (typed FeaturePython)
  n = 0.387472
FEATURE [App::DocumentObjectGroupPython] G4_CELLULOSE_BUTYRATE  # scripted group (container) (typed FeaturePython)
  Dunit = g/cm3
  Dvalue = 1.2
  Group = -> [H_element022,C_element026,O_element027]
  conduct = 2
  density = 1
  expand = 3
  formula = G4_CELLULOSE_BUTYRATE
  name = G4_CELLULOSE_BUTYRATE
  specific = 4
FEATURE [App::DocumentObjectGroupPython] H_element023  label="H_element : 0.029"  # scripted group (container) (typed FeaturePython)
  n = 0.029216
FEATURE [App::DocumentObjectGroupPython] C_element027  label="C_element : 0.271"  # scripted group (container) (typed FeaturePython)
  n = 0.271296
FEATURE [App::DocumentObjectGroupPython] N_element013  label="N_element : 0.121"  # scripted group (container) (typed FeaturePython)
  n = 0.121276
FEATURE [App::DocumentObjectGroupPython] O_element028  label="O_element : 0.578"  # scripted group (container) (typed FeaturePython)
  n = 0.578212
FEATURE [App::DocumentObjectGroupPython] G4_CELLULOSE_NITRATE  # scripted group (container) (typed FeaturePython)
  Dunit = g/cm3
  Dvalue = 1.49
  Group = -> [H_element023,C_element027,N_element013,O_element028]
  conduct = 2
  density = 1
  expand = 3
  formula = G4_CELLULOSE_NITRATE
  name = G4_CELLULOSE_NITRATE
  specific = 4
FEATURE [App::DocumentObjectGroupPython] H_element024  label="H_element : 0.108"  # scripted group (container) (typed FeaturePython)
  n = 0.107596
FEATURE [App::DocumentObjectGroupPython] N_element014  label="N_element : 0.001"  # scripted group (container) (typed FeaturePython)
  n = 0.0008
FEATURE [App::DocumentObjectGroupPython] O_element029  label="O_element : 0.875"  # scripted group (container) (typed FeaturePython)
  n = 0.874976
FEATURE [App::DocumentObjectGroupPython] S_element008  label="S_element : 0.015"  # scripted group (container) (typed FeaturePython)
  n = 0.014627
FEATURE [App::DocumentObjectGroupPython] Ce_element001  label="Ce_element : 0.002"  # scripted group (container) (typed FeaturePython)
  n = 0.002001
FEATURE [App::DocumentObjectGroupPython] G4_CERIC_SULFATE  # scripted group (container) (typed FeaturePython)
  Dunit = g/cm3
  Dvalue = 1.03
  Group = -> [H_element024,N_element014,O_element029,S_element008,Ce_element001]
  conduct = 2
  density = 1
  expand = 3
  formula = G4_CERIC_SULFATE
  name = G4_CERIC_SULFATE
  specific = 4
FEATURE [App::DocumentObjectGroupPython] Cs_element001  label="Cs_element : 1"  # scripted group (container) (typed FeaturePython)
  n = 1
  ref = Cs_element
FEATURE [App::DocumentObjectGroupPython] F_element006  label="F_element : 1"  # scripted group (container) (typed FeaturePython)
  n = 1
  ref = F_element
FEATURE [App::DocumentObjectGroupPython] G4_CESIUM_FLUORIDE  # scripted group (container) (typed FeaturePython)
  Dunit = g/cm3
  Dvalue = 4.115
  Group = -> [Cs_element001,F_element006]
  conduct = 2
  density = 1
  expand = 3
  formula = G4_CESIUM_FLUORIDE
  name = G4_CESIUM_FLUORIDE
  specific = 4
FEATURE [App::DocumentObjectGroupPython] Cs_element002  label="Cs_element : 002"  # scripted group (container) (typed FeaturePython)
  n = 1
  ref = Cs_element
FEATURE [App::DocumentObjectGroupPython] I_element001  label="I_element : 1"  # scripted group (container) (typed FeaturePython)
  n = 1
  ref = I_element
FEATURE [App::DocumentObjectGroupPython] G4_CESIUM_IODIDE  # scripted group (container) (typed FeaturePython)
  Dunit = g/cm3
  Dvalue = 4.51
  Group = -> [Cs_element002,I_element001]
  conduct = 2
  density = 1
  expand = 3
  formula = G4_CESIUM_IODIDE
  name = G4_CESIUM_IODIDE
  specific = 4
FEATURE [App::DocumentObjectGroupPython] C_element028  label="C_element : 013"  # scripted group (container) (typed FeaturePython)
  n = 6
  ref = C_element
FEATURE [App::DocumentObjectGroupPython] H_element025  label="H_element : 013"  # scripted group (container) (typed FeaturePython)
  n = 5
  ref = H_element
FEATURE [App::DocumentObjectGroupPython] Cl_element005  label="Cl_element : 1"  # scripted group (container) (typed FeaturePython)
  n = 1
  ref = Cl_element
FEATURE [App::DocumentObjectGroupPython] G4_CHLOROBENZENE  # scripted group (container) (typed FeaturePython)
  Dunit = g/cm3
  Dvalue = 1.1058
  Group = -> [C_element028,H_element025,Cl_element005]
  conduct = 2
  density = 1
  expand = 3
  formula = G4_CHLOROBENZENE
  name = G4_CHLOROBENZENE
  specific = 4
FEATURE [App::DocumentObjectGroupPython] C_element029  label="C_element : 014"  # scripted group (container) (typed FeaturePython)
  n = 1
  ref = C_element
FEATURE [App::DocumentObjectGroupPython] H_element026  label="H_element : 1"  # scripted group (container) (typed FeaturePython)
  n = 1
  ref = H_element
FEATURE [App::DocumentObjectGroupPython] Cl_element006  label="Cl_element : 3"  # scripted group (container) (typed FeaturePython)
  n = 3
  ref = Cl_element
FEATURE [App::DocumentObjectGroupPython] G4_CHLOROFORM  # scripted group (container) (typed FeaturePython)
  Dunit = g/cm3
  Dvalue = 1.4832
  Group = -> [C_element029,H_element026,Cl_element006]
  conduct = 2
  density = 1
  expand = 3
  formula = G4_CHLOROFORM
  name = G4_CHLOROFORM
  specific = 4
FEATURE [App::DocumentObjectGroupPython] H_element027  label="H_element : 0.010"  # scripted group (container) (typed FeaturePython)
  n = 0.01
FEATURE [App::DocumentObjectGroupPython] C_element030  label="C_element : 0.001"  # scripted group (container) (typed FeaturePython)
  n = 0.001
FEATURE [App::DocumentObjectGroupPython] O_element030  label="O_element : 0.529"  # scripted group (container) (typed FeaturePython)
  n = 0.529107
FEATURE [App::DocumentObjectGroupPython] Na_element005  label="Na_element : 0.016"  # scripted group (container) (typed FeaturePython)
  n = 0.016
FEATURE [App::DocumentObjectGroupPython] Mg_element003  label="Mg_element : 0.004"  # scripted group (container) (typed FeaturePython)
  n = 0.002
FEATURE [App::DocumentObjectGroupPython] Al_element002  label="Al_element : 0.034"  # scripted group (container) (typed FeaturePython)
  n = 0.033872
FEATURE [App::DocumentObjectGroupPython] Si_element002  label="Si_element : 0.337"  # scripted group (container) (typed FeaturePython)
  n = 0.337021
FEATURE [App::DocumentObjectGroupPython] K_element003  label="K_element : 0.013"  # scripted group (container) (typed FeaturePython)
  n = 0.013
FEATURE [App::DocumentObjectGroupPython] Ca_element010  label="Ca_element : 0.044"  # scripted group (container) (typed FeaturePython)
  n = 0.044
FEATURE [App::DocumentObjectGroupPython] Fe_element002  label="Fe_element : 0.014"  # scripted group (container) (typed FeaturePython)
  n = 0.014
FEATURE [App::DocumentObjectGroupPython] G4_CONCRETE  # scripted group (container) (typed FeaturePython)
  Dunit = g/cm3
  Dvalue = 2.3
  Group = -> [H_element027,C_element030,O_element030,Na_element005,Mg_element003,Al_element002,Si_element002,K_element003,Ca_element010,Fe_element002]
  conduct = 2
  density = 1
  expand = 3
  formula = G4_CONCRETE
  name = G4_CONCRETE
  specific = 4
FEATURE [App::DocumentObjectGroupPython] C_element031  label="C_element : 015"  # scripted group (container) (typed FeaturePython)
  n = 6
  ref = C_element
FEATURE [App::DocumentObjectGroupPython] H_element028  label="H_element : 12"  # scripted group (container) (typed FeaturePython)
  n = 12
  ref = H_element
FEATURE [App::DocumentObjectGroupPython] G4_CYCLOHEXANE  # scripted group (container) (typed FeaturePython)
  Dunit = g/cm3
  Dvalue = 0.779
  Group = -> [C_element031,H_element028]
  conduct = 2
  density = 1
  expand = 3
  formula = G4_CYCLOHEXANE
  name = G4_CYCLOHEXANE
  specific = 4
FEATURE [App::DocumentObjectGroupPython] C_element032  label="C_element : 016"  # scripted group (container) (typed FeaturePython)
  n = 6
  ref = C_element
FEATURE [App::DocumentObjectGroupPython] H_element029  label="H_element : 4"  # scripted group (container) (typed FeaturePython)
  n = 4
  ref = H_element
FEATURE [App::DocumentObjectGroupPython] Cl_element007  label="Cl_element : 2"  # scripted group (container) (typed FeaturePython)
  n = 2
  ref = Cl_element
FEATURE [App::DocumentObjectGroupPython] G4_1_2_DICHLOROBENZENE  label="G4_1.2-DICHLOROBENZENE"  # scripted group (container) (typed FeaturePython)
  Dunit = g/cm3
  Dvalue = 1.3048
  Group = -> [C_element032,H_element029,Cl_element007]
  conduct = 2
  density = 1
  expand = 3
  formula = G4_1.2-DICHLOROBENZENE
  name = G4_1.2-DICHLOROBENZENE
  specific = 4
FEATURE [App::DocumentObjectGroupPython] C_element033  label="C_element : 017"  # scripted group (container) (typed FeaturePython)
  n = 4
  ref = C_element
FEATURE [App::DocumentObjectGroupPython] H_element030  label="H_element : 8"  # scripted group (container) (typed FeaturePython)
  n = 8
  ref = H_element
FEATURE [App::DocumentObjectGroupPython] O_element031  label="O_element : 014"  # scripted group (container) (typed FeaturePython)
  n = 1
  ref = O_element
FEATURE [App::DocumentObjectGroupPython] Cl_element008  label="Cl_element : 005"  # scripted group (container) (typed FeaturePython)
  n = 2
  ref = Cl_element
FEATURE [App::DocumentObjectGroupPython] G4_DICHLORODIETHYL_ETHER  # scripted group (container) (typed FeaturePython)
  Dunit = g/cm3
  Dvalue = 1.2199
  Group = -> [C_element033,H_element030,O_element031,Cl_element008]
  conduct = 2
  density = 1
  expand = 3
  formula = G4_DICHLORODIETHYL_ETHER
  name = G4_DICHLORODIETHYL_ETHER
  specific = 4
FEATURE [App::DocumentObjectGroupPython] C_element034  label="C_element : 018"  # scripted group (container) (typed FeaturePython)
  n = 2
  ref = C_element
FEATURE [App::DocumentObjectGroupPython] H_element031  label="H_element : 014"  # scripted group (container) (typed FeaturePython)
  n = 4
  ref = H_element
FEATURE [App::DocumentObjectGroupPython] Cl_element009  label="Cl_element : 006"  # scripted group (container) (typed FeaturePython)
  n = 2
  ref = Cl_element
FEATURE [App::DocumentObjectGroupPython] G4_1_2_DICHLOROETHANE  label="G4_1.2-DICHLOROETHANE"  # scripted group (container) (typed FeaturePython)
  Dunit = g/cm3
  Dvalue = 1.2351
  Group = -> [C_element034,H_element031,Cl_element009]
  conduct = 2
  density = 1
  expand = 3
  formula = G4_1.2-DICHLOROETHANE
  name = G4_1.2-DICHLOROETHANE
  specific = 4
FEATURE [App::DocumentObjectGroupPython] C_element035  label="C_element : 019"  # scripted group (container) (typed FeaturePython)
  n = 4
  ref = C_element
FEATURE [App::DocumentObjectGroupPython] H_element032  label="H_element : 015"  # scripted group (container) (typed FeaturePython)
  n = 10
  ref = H_element
FEATURE [App::DocumentObjectGroupPython] O_element032  label="O_element : 015"  # scripted group (container) (typed FeaturePython)
  n = 1
  ref = O_element
FEATURE [App::DocumentObjectGroupPython] G4_DIETHYL_ETHER  # scripted group (container) (typed FeaturePython)
  Dunit = g/cm3
  Dvalue = 0.71378
  Group = -> [C_element035,H_element032,O_element032]
  conduct = 2
  density = 1
  expand = 3
  formula = G4_DIETHYL_ETHER
  name = G4_DIETHYL_ETHER
  specific = 4
FEATURE [App::DocumentObjectGroupPython] C_element036  label="C_element : 020"  # scripted group (container) (typed FeaturePython)
  n = 3
  ref = C_element
FEATURE [App::DocumentObjectGroupPython] H_element033  label="H_element : 016"  # scripted group (container) (typed FeaturePython)
  n = 7
  ref = H_element
FEATURE [App::DocumentObjectGroupPython] N_element015  label="N_element : 008"  # scripted group (container) (typed FeaturePython)
  n = 1
  ref = N_element
FEATURE [App::DocumentObjectGroupPython] O_element033  label="O_element : 016"  # scripted group (container) (typed FeaturePython)
  n = 1
  ref = O_element
FEATURE [App::DocumentObjectGroupPython] G4_N_N_DIMETHYL_FORMAMIDE  label="G4_N.N-DIMETHYL_FORMAMIDE"  # scripted group (container) (typed FeaturePython)
  Dunit = g/cm3
  Dvalue = 0.9487
  Group = -> [C_element036,H_element033,N_element015,O_element033]
  conduct = 2
  density = 1
  expand = 3
  formula = G4_N.N-DIMETHYL_FORMAMIDE
  name = G4_N.N-DIMETHYL_FORMAMIDE
  specific = 4
FEATURE [App::DocumentObjectGroupPython] C_element037  label="C_element : 021"  # scripted group (container) (typed FeaturePython)
  n = 2
  ref = C_element
FEATURE [App::DocumentObjectGroupPython] H_element034  label="H_element : 017"  # scripted group (container) (typed FeaturePython)
  n = 6
  ref = H_element
FEATURE [App::DocumentObjectGroupPython] O_element034  label="O_element : 017"  # scripted group (container) (typed FeaturePython)
  n = 1
  ref = O_element
FEATURE [App::DocumentObjectGroupPython] S_element009  label="S_element : 003"  # scripted group (container) (typed FeaturePython)
  n = 1
  ref = S_element
FEATURE [App::DocumentObjectGroupPython] G4_DIMETHYL_SULFOXIDE  # scripted group (container) (typed FeaturePython)
  Dunit = g/cm3
  Dvalue = 1.1014
  Group = -> [C_element037,H_element034,O_element034,S_element009]
  conduct = 2
  density = 1
  expand = 3
  formula = G4_DIMETHYL_SULFOXIDE
  name = G4_DIMETHYL_SULFOXIDE
  specific = 4
FEATURE [App::DocumentObjectGroupPython] C_element038  label="C_element : 022"  # scripted group (container) (typed FeaturePython)
  n = 2
  ref = C_element
FEATURE [App::DocumentObjectGroupPython] H_element035  label="H_element : 018"  # scripted group (container) (typed FeaturePython)
  n = 6
  ref = H_element
FEATURE [App::DocumentObjectGroupPython] G4_ETHANE  # scripted group (container) (typed FeaturePython)
  Dunit = g/cm3
  Dvalue = 0.00125324
  Group = -> [C_element038,H_element035]
  conduct = 2
  density = 1
  expand = 3
  formula = G4_ETHANE
  name = G4_ETHANE
  specific = 4
FEATURE [App::DocumentObjectGroupPython] C_element039  label="C_element : 023"  # scripted group (container) (typed FeaturePython)
  n = 2
  ref = C_element
FEATURE [App::DocumentObjectGroupPython] H_element036  label="H_element : 019"  # scripted group (container) (typed FeaturePython)
  n = 6
  ref = H_element
FEATURE [App::DocumentObjectGroupPython] O_element035  label="O_element : 018"  # scripted group (container) (typed FeaturePython)
  n = 1
  ref = O_element
FEATURE [App::DocumentObjectGroupPython] G4_ETHYL_ALCOHOL  # scripted group (container) (typed FeaturePython)
  Dunit = g/cm3
  Dvalue = 0.7893
  Group = -> [C_element039,H_element036,O_element035]
  conduct = 2
  density = 1
  expand = 3
  formula = G4_ETHYL_ALCOHOL
  name = G4_ETHYL_ALCOHOL
  specific = 4
FEATURE [App::DocumentObjectGroupPython] H_element037  label="H_element : 0.090"  # scripted group (container) (typed FeaturePython)
  n = 0.090027
FEATURE [App::DocumentObjectGroupPython] C_element040  label="C_element : 0.585"  # scripted group (container) (typed FeaturePython)
  n = 0.585182
FEATURE [App::DocumentObjectGroupPython] O_element036  label="O_element : 0.325"  # scripted group (container) (typed FeaturePython)
  n = 0.324791
FEATURE [App::DocumentObjectGroupPython] G4_ETHYL_CELLULOSE  # scripted group (container) (typed FeaturePython)
  Dunit = g/cm3
  Dvalue = 1.13
  Group = -> [H_element037,C_element040,O_element036]
  conduct = 2
  density = 1
  expand = 3
  formula = G4_ETHYL_CELLULOSE
  name = G4_ETHYL_CELLULOSE
  specific = 4
FEATURE [App::DocumentObjectGroupPython] C_element041  label="C_element : 024"  # scripted group (container) (typed FeaturePython)
  n = 2
  ref = C_element
FEATURE [App::DocumentObjectGroupPython] H_element038  label="H_element : 020"  # scripted group (container) (typed FeaturePython)
  n = 4
  ref = H_element
FEATURE [App::DocumentObjectGroupPython] G4_ETHYLENE  # scripted group (container) (typed FeaturePython)
  Dunit = g/cm3
  Dvalue = 0.00117497
  Group = -> [C_element041,H_element038]
  conduct = 2
  density = 1
  expand = 3
  formula = G4_ETHYLENE
  name = G4_ETHYLENE
  specific = 4
FEATURE [App::DocumentObjectGroupPython] H_element039  label="H_element : 0.096"  # scripted group (container) (typed FeaturePython)
  n = 0.096
FEATURE [App::DocumentObjectGroupPython] C_element042  label="C_element : 0.195"  # scripted group (container) (typed FeaturePython)
  n = 0.195
FEATURE [App::DocumentObjectGroupPython] N_element016  label="N_element : 0.057"  # scripted group (container) (typed FeaturePython)
  n = 0.057
FEATURE [App::DocumentObjectGroupPython] O_element037  label="O_element : 0.646"  # scripted group (container) (typed FeaturePython)
  n = 0.646
FEATURE [App::DocumentObjectGroupPython] Na_element006  label="Na_element : 0.017"  # scripted group (container) (typed FeaturePython)
  n = 0.001
FEATURE [App::DocumentObjectGroupPython] P_element005  label="P_element : 0.104"  # scripted group (container) (typed FeaturePython)
  n = 0.001
FEATURE [App::DocumentObjectGroupPython] S_element010  label="S_element : 0.016"  # scripted group (container) (typed FeaturePython)
  n = 0.003
FEATURE [App::DocumentObjectGroupPython] Cl_element010  label="Cl_element : 0.005"  # scripted group (container) (typed FeaturePython)
  n = 0.001
FEATURE [App::DocumentObjectGroupPython] G4_EYE_LENS_ICRP  # scripted group (container) (typed FeaturePython)
  Dunit = g/cm3
  Dvalue = 1.07
  Group = -> [H_element039,C_element042,N_element016,O_element037,Na_element006,P_element005,S_element010,Cl_element010]
  conduct = 2
  density = 1
  expand = 3
  formula = G4_EYE_LENS_ICRP
  name = G4_EYE_LENS_ICRP
  specific = 4
FEATURE [App::DocumentObjectGroupPython] Fe_element003  label="Fe_element : 2"  # scripted group (container) (typed FeaturePython)
  n = 2
  ref = Fe_element
FEATURE [App::DocumentObjectGroupPython] O_element038  label="O_element : 019"  # scripted group (container) (typed FeaturePython)
  n = 3
  ref = O_element
FEATURE [App::DocumentObjectGroupPython] G4_FERRIC_OXIDE  # scripted group (container) (typed FeaturePython)
  Dunit = g/cm3
  Dvalue = 5.2
  Group = -> [Fe_element003,O_element038]
  conduct = 2
  density = 1
  expand = 3
  formula = G4_FERRIC_OXIDE
  name = G4_FERRIC_OXIDE
  specific = 4
FEATURE [App::DocumentObjectGroupPython] Fe_element004  label="Fe_element : 1"  # scripted group (container) (typed FeaturePython)
  n = 1
  ref = Fe_element
FEATURE [App::DocumentObjectGroupPython] B_element003  label="B_element : 1"  # scripted group (container) (typed FeaturePython)
  n = 1
  ref = B_element
FEATURE [App::DocumentObjectGroupPython] G4_FERROBORIDE  # scripted group (container) (typed FeaturePython)
  Dunit = g/cm3
  Dvalue = 7.15
  Group = -> [Fe_element004,B_element003]
  conduct = 2
  density = 1
  expand = 3
  formula = G4_FERROBORIDE
  name = G4_FERROBORIDE
  specific = 4
FEATURE [App::DocumentObjectGroupPython] Fe_element005  label="Fe_element : 003"  # scripted group (container) (typed FeaturePython)
  n = 1
  ref = Fe_element
FEATURE [App::DocumentObjectGroupPython] O_element039  label="O_element : 020"  # scripted group (container) (typed FeaturePython)
  n = 1
  ref = O_element
FEATURE [App::DocumentObjectGroupPython] G4_FERROUS_OXIDE  # scripted group (container) (typed FeaturePython)
  Dunit = g/cm3
  Dvalue = 5.7
  Group = -> [Fe_element005,O_element039]
  conduct = 2
  density = 1
  expand = 3
  formula = G4_FERROUS_OXIDE
  name = G4_FERROUS_OXIDE
  specific = 4
FEATURE [App::DocumentObjectGroupPython] H_element040  label="H_element : 0.115"  # scripted group (container) (typed FeaturePython)
  n = 0.108259
FEATURE [App::DocumentObjectGroupPython] N_element017  label="N_element : 0.000"  # scripted group (container) (typed FeaturePython)
  n = 2.7e-05
FEATURE [App::DocumentObjectGroupPython] O_element040  label="O_element : 0.879"  # scripted group (container) (typed FeaturePython)
  n = 0.878636
FEATURE [App::DocumentObjectGroupPython] Na_element007  label="Na_element : 0.000"  # scripted group (container) (typed FeaturePython)
  n = 2.2e-05
FEATURE [App::DocumentObjectGroupPython] S_element011  label="S_element : 0.013"  # scripted group (container) (typed FeaturePython)
  n = 0.012968
FEATURE [App::DocumentObjectGroupPython] Cl_element011  label="Cl_element : 0.000"  # scripted group (container) (typed FeaturePython)
  n = 3.4e-05
FEATURE [App::DocumentObjectGroupPython] Fe_element006  label="Fe_element : 0.000"  # scripted group (container) (typed FeaturePython)
  n = 5.4e-05
FEATURE [App::DocumentObjectGroupPython] G4_FERROUS_SULFATE  # scripted group (container) (typed FeaturePython)
  Dunit = g/cm3
  Dvalue = 1.024
  Group = -> [H_element040,N_element017,O_element040,Na_element007,S_element011,Cl_element011,Fe_element006]
  conduct = 2
  density = 1
  expand = 3
  formula = G4_FERROUS_SULFATE
  name = G4_FERROUS_SULFATE
  specific = 4
FEATURE [App::DocumentObjectGroupPython] C_element043  label="C_element : 0.099"  # scripted group (container) (typed FeaturePython)
  n = 0.099335
FEATURE [App::DocumentObjectGroupPython] F_element007  label="F_element : 0.314"  # scripted group (container) (typed FeaturePython)
  n = 0.314247
FEATURE [App::DocumentObjectGroupPython] Cl_element012  label="Cl_element : 0.586"  # scripted group (container) (typed FeaturePython)
  n = 0.586418
FEATURE [App::DocumentObjectGroupPython] G4_FREON_12  label="G4_FREON-12"  # scripted group (container) (typed FeaturePython)
  Dunit = g/cm3
  Dvalue = 1.12
  Group = -> [C_element043,F_element007,Cl_element012]
  conduct = 2
  density = 1
  expand = 3
  formula = G4_FREON-12
  name = G4_FREON-12
  specific = 4
FEATURE [App::DocumentObjectGroupPython] C_element044  label="C_element : 0.057"  # scripted group (container) (typed FeaturePython)
  n = 0.057245
FEATURE [App::DocumentObjectGroupPython] F_element008  label="F_element : 0.181"  # scripted group (container) (typed FeaturePython)
  n = 0.181096
FEATURE [App::DocumentObjectGroupPython] Br_element001  label="Br_element : 0.762"  # scripted group (container) (typed FeaturePython)
  n = 0.761659
FEATURE [App::DocumentObjectGroupPython] G4_FREON_12B2  label="G4_FREON-12B2"  # scripted group (container) (typed FeaturePython)
  Dunit = g/cm3
  Dvalue = 1.8
  Group = -> [C_element044,F_element008,Br_element001]
  conduct = 2
  density = 1
  expand = 3
  formula = G4_FREON-12B2
  name = G4_FREON-12B2
  specific = 4
FEATURE [App::DocumentObjectGroupPython] C_element045  label="C_element : 0.115"  # scripted group (container) (typed FeaturePython)
  n = 0.114983
FEATURE [App::DocumentObjectGroupPython] F_element009  label="F_element : 0.546"  # scripted group (container) (typed FeaturePython)
  n = 0.545621
FEATURE [App::DocumentObjectGroupPython] Cl_element013  label="Cl_element : 0.339"  # scripted group (container) (typed FeaturePython)
  n = 0.339396
FEATURE [App::DocumentObjectGroupPython] G4_FREON_13  label="G4_FREON-13"  # scripted group (container) (typed FeaturePython)
  Dunit = g/cm3
  Dvalue = 0.95
  Group = -> [C_element045,F_element009,Cl_element013]
  conduct = 2
  density = 1
  expand = 3
  formula = G4_FREON-13
  name = G4_FREON-13
  specific = 4
FEATURE [App::DocumentObjectGroupPython] C_element046  label="C_element : 025"  # scripted group (container) (typed FeaturePython)
  n = 1
  ref = C_element
FEATURE [App::DocumentObjectGroupPython] F_element010  label="F_element : 3"  # scripted group (container) (typed FeaturePython)
  n = 3
  ref = F_element
FEATURE [App::DocumentObjectGroupPython] Br_element002  label="Br_element : 1"  # scripted group (container) (typed FeaturePython)
  n = 1
  ref = Br_element
FEATURE [App::DocumentObjectGroupPython] G4_FREON_13B1  label="G4_FREON-13B1"  # scripted group (container) (typed FeaturePython)
  Dunit = g/cm3
  Dvalue = 1.5
  Group = -> [C_element046,F_element010,Br_element002]
  conduct = 2
  density = 1
  expand = 3
  formula = G4_FREON-13B1
  name = G4_FREON-13B1
  specific = 4
FEATURE [App::DocumentObjectGroupPython] C_element047  label="C_element : 0.061"  # scripted group (container) (typed FeaturePython)
  n = 0.061309
FEATURE [App::DocumentObjectGroupPython] F_element011  label="F_element : 0.291"  # scripted group (container) (typed FeaturePython)
  n = 0.290924
FEATURE [App::DocumentObjectGroupPython] I_element002  label="I_element : 0.648"  # scripted group (container) (typed FeaturePython)
  n = 0.647767
FEATURE [App::DocumentObjectGroupPython] G4_FREON_13I1  label="G4_FREON-13I1"  # scripted group (container) (typed FeaturePython)
  Dunit = g/cm3
  Dvalue = 1.8
  Group = -> [C_element047,F_element011,I_element002]
  conduct = 2
  density = 1
  expand = 3
  formula = G4_FREON-13I1
  name = G4_FREON-13I1
  specific = 4
FEATURE [App::DocumentObjectGroupPython] Gd_element001  label="Gd_element : 2"  # scripted group (container) (typed FeaturePython)
  n = 2
  ref = Gd_element
FEATURE [App::DocumentObjectGroupPython] O_element041  label="O_element : 021"  # scripted group (container) (typed FeaturePython)
  n = 2
  ref = O_element
FEATURE [App::DocumentObjectGroupPython] S_element012  label="S_element : 004"  # scripted group (container) (typed FeaturePython)
  n = 1
  ref = S_element
FEATURE [App::DocumentObjectGroupPython] G4_GADOLINIUM_OXYSULFIDE  # scripted group (container) (typed FeaturePython)
  Dunit = g/cm3
  Dvalue = 7.44
  Group = -> [Gd_element001,O_element041,S_element012]
  conduct = 2
  density = 1
  expand = 3
  formula = G4_GADOLINIUM_OXYSULFIDE
  name = G4_GADOLINIUM_OXYSULFIDE
  specific = 4
FEATURE [App::DocumentObjectGroupPython] Ga_element001  label="Ga_element : 1"  # scripted group (container) (typed FeaturePython)
  n = 1
  ref = Ga_element
FEATURE [App::DocumentObjectGroupPython] As_element001  label="As_element : 1"  # scripted group (container) (typed FeaturePython)
  n = 1
  ref = As_element
FEATURE [App::DocumentObjectGroupPython] G4_GALLIUM_ARSENIDE  # scripted group (container) (typed FeaturePython)
  Dunit = g/cm3
  Dvalue = 5.31
  Group = -> [Ga_element001,As_element001]
  conduct = 2
  density = 1
  expand = 3
  formula = G4_GALLIUM_ARSENIDE
  name = G4_GALLIUM_ARSENIDE
  specific = 4
FEATURE [App::DocumentObjectGroupPython] H_element041  label="H_element : 0.081"  # scripted group (container) (typed FeaturePython)
  n = 0.08118
FEATURE [App::DocumentObjectGroupPython] C_element048  label="C_element : 0.416"  # scripted group (container) (typed FeaturePython)
  n = 0.41606
FEATURE [App::DocumentObjectGroupPython] N_element018  label="N_element : 0.111"  # scripted group (container) (typed FeaturePython)
  n = 0.11124
FEATURE [App::DocumentObjectGroupPython] O_element042  label="O_element : 0.381"  # scripted group (container) (typed FeaturePython)
  n = 0.38064
FEATURE [App::DocumentObjectGroupPython] S_element013  label="S_element : 0.011"  # scripted group (container) (typed FeaturePython)
  n = 0.01088
FEATURE [App::DocumentObjectGroupPython] G4_GEL_PHOTO_EMULSION  # scripted group (container) (typed FeaturePython)
  Dunit = g/cm3
  Dvalue = 1.2914
  Group = -> [H_element041,C_element048,N_element018,O_element042,S_element013]
  conduct = 2
  density = 1
  expand = 3
  formula = G4_GEL_PHOTO_EMULSION
  name = G4_GEL_PHOTO_EMULSION
  specific = 4
FEATURE [App::DocumentObjectGroupPython] B_element004  label="B_element : 0.040"  # scripted group (container) (typed FeaturePython)
  n = 0.0400639
FEATURE [App::DocumentObjectGroupPython] O_element043  label="O_element : 0.540"  # scripted group (container) (typed FeaturePython)
  n = 0.539561
FEATURE [App::DocumentObjectGroupPython] Na_element008  label="Na_element : 0.028"  # scripted group (container) (typed FeaturePython)
  n = 0.0281909
FEATURE [App::DocumentObjectGroupPython] Al_element003  label="Al_element : 0.012"  # scripted group (container) (typed FeaturePython)
  n = 0.011644
FEATURE [App::DocumentObjectGroupPython] Si_element003  label="Si_element : 0.377"  # scripted group (container) (typed FeaturePython)
  n = 0.377219
FEATURE [App::DocumentObjectGroupPython] K_element004  label="K_element : 0.014"  # scripted group (container) (typed FeaturePython)
  n = 0.00332099
FEATURE [App::DocumentObjectGroupPython] G4_Pyrex_Glass  # scripted group (container) (typed FeaturePython)
  Dunit = g/cm3
  Dvalue = 2.23
  Group = -> [B_element004,O_element043,Na_element008,Al_element003,Si_element003,K_element004]
  conduct = 2
  density = 1
  expand = 3
  formula = G4_Pyrex_Glass
  name = G4_Pyrex_Glass
  specific = 4
FEATURE [App::DocumentObjectGroupPython] O_element044  label="O_element : 0.156"  # scripted group (container) (typed FeaturePython)
  n = 0.156453
FEATURE [App::DocumentObjectGroupPython] Si_element004  label="Si_element : 0.081"  # scripted group (container) (typed FeaturePython)
  n = 0.080866
FEATURE [App::DocumentObjectGroupPython] Ti_element001  label="Ti_element : 0.008"  # scripted group (container) (typed FeaturePython)
  n = 0.008092
FEATURE [App::DocumentObjectGroupPython] As_element002  label="As_element : 0.003"  # scripted group (container) (typed FeaturePython)
  n = 0.002651
FEATURE [App::DocumentObjectGroupPython] Pb_element001  label="Pb_element : 0.752"  # scripted group (container) (typed FeaturePython)
  n = 0.751938
FEATURE [App::DocumentObjectGroupPython] G4_GLASS_LEAD  # scripted group (container) (typed FeaturePython)
  Dunit = g/cm3
  Dvalue = 6.22
  Group = -> [O_element044,Si_element004,Ti_element001,As_element002,Pb_element001]
  conduct = 2
  density = 1
  expand = 3
  formula = G4_GLASS_LEAD
  name = G4_GLASS_LEAD
  specific = 4
FEATURE [App::DocumentObjectGroupPython] O_element045  label="O_element : 0.460"  # scripted group (container) (typed FeaturePython)
  n = 0.4598
FEATURE [App::DocumentObjectGroupPython] Na_element009  label="Na_element : 0.096"  # scripted group (container) (typed FeaturePython)
  n = 0.0964411
FEATURE [App::DocumentObjectGroupPython] Si_element005  label="Si_element : 0.378"  # scripted group (container) (typed FeaturePython)
  n = 0.336553
FEATURE [App::DocumentObjectGroupPython] Ca_element011  label="Ca_element : 0.107"  # scripted group (container) (typed FeaturePython)
  n = 0.107205
FEATURE [App::DocumentObjectGroupPython] G4_GLASS_PLATE  # scripted group (container) (typed FeaturePython)
  Dunit = g/cm3
  Dvalue = 2.4
  Group = -> [O_element045,Na_element009,Si_element005,Ca_element011]
  conduct = 2
  density = 1
  expand = 3
  formula = G4_GLASS_PLATE
  name = G4_GLASS_PLATE
  specific = 4
FEATURE [App::DocumentObjectGroupPython] C_element049  label="C_element : 026"  # scripted group (container) (typed FeaturePython)
  n = 5
  ref = C_element
FEATURE [App::DocumentObjectGroupPython] H_element042  label="H_element : 021"  # scripted group (container) (typed FeaturePython)
  n = 10
  ref = H_element
FEATURE [App::DocumentObjectGroupPython] N_element019  label="N_element : 2"  # scripted group (container) (typed FeaturePython)
  n = 2
  ref = N_element
FEATURE [App::DocumentObjectGroupPython] O_element046  label="O_element : 022"  # scripted group (container) (typed FeaturePython)
  n = 3
  ref = O_element
FEATURE [App::DocumentObjectGroupPython] G4_GLUTAMINE  # scripted group (container) (typed FeaturePython)
  Dunit = g/cm3
  Dvalue = 1.46
  Group = -> [C_element049,H_element042,N_element019,O_element046]
  conduct = 2
  density = 1
  expand = 3
  formula = G4_GLUTAMINE
  name = G4_GLUTAMINE
  specific = 4
FEATURE [App::DocumentObjectGroupPython] C_element050  label="C_element : 027"  # scripted group (container) (typed FeaturePython)
  n = 3
  ref = C_element
FEATURE [App::DocumentObjectGroupPython] H_element043  label="H_element : 022"  # scripted group (container) (typed FeaturePython)
  n = 8
  ref = H_element
FEATURE [App::DocumentObjectGroupPython] O_element047  label="O_element : 023"  # scripted group (container) (typed FeaturePython)
  n = 3
  ref = O_element
FEATURE [App::DocumentObjectGroupPython] G4_GLYCEROL  # scripted group (container) (typed FeaturePython)
  Dunit = g/cm3
  Dvalue = 1.2613
  Group = -> [C_element050,H_element043,O_element047]
  conduct = 2
  density = 1
  expand = 3
  formula = G4_GLYCEROL
  name = G4_GLYCEROL
  specific = 4
FEATURE [App::DocumentObjectGroupPython] C_element051  label="C_element : 028"  # scripted group (container) (typed FeaturePython)
  n = 5
  ref = C_element
FEATURE [App::DocumentObjectGroupPython] H_element044  label="H_element : 023"  # scripted group (container) (typed FeaturePython)
  n = 5
  ref = H_element
FEATURE [App::DocumentObjectGroupPython] N_element020  label="N_element : 009"  # scripted group (container) (typed FeaturePython)
  n = 5
  ref = N_element
FEATURE [App::DocumentObjectGroupPython] O_element048  label="O_element : 024"  # scripted group (container) (typed FeaturePython)
  n = 1
  ref = O_element
FEATURE [App::DocumentObjectGroupPython] G4_GUANINE  # scripted group (container) (typed FeaturePython)
  Dunit = g/cm3
  Dvalue = 2.2
  Group = -> [C_element051,H_element044,N_element020,O_element048]
  conduct = 2
  density = 1
  expand = 3
  formula = G4_GUANINE
  name = G4_GUANINE
  specific = 4
FEATURE [App::DocumentObjectGroupPython] Ca_element012  label="Ca_element : 006"  # scripted group (container) (typed FeaturePython)
  n = 1
  ref = Ca_element
FEATURE [App::DocumentObjectGroupPython] S_element014  label="S_element : 005"  # scripted group (container) (typed FeaturePython)
  n = 1
  ref = S_element
FEATURE [App::DocumentObjectGroupPython] O_element049  label="O_element : 6"  # scripted group (container) (typed FeaturePython)
  n = 6
  ref = O_element
FEATURE [App::DocumentObjectGroupPython] H_element045  label="H_element : 024"  # scripted group (container) (typed FeaturePython)
  n = 4
  ref = H_element
FEATURE [App::DocumentObjectGroupPython] G4_GYPSUM  # scripted group (container) (typed FeaturePython)
  Dunit = g/cm3
  Dvalue = 2.32
  Group = -> [Ca_element012,S_element014,O_element049,H_element045]
  conduct = 2
  density = 1
  expand = 3
  formula = G4_GYPSUM
  name = G4_GYPSUM
  specific = 4
FEATURE [App::DocumentObjectGroupPython] C_element052  label="C_element : 7"  # scripted group (container) (typed FeaturePython)
  n = 7
  ref = C_element
FEATURE [App::DocumentObjectGroupPython] H_element046  label="H_element : 16"  # scripted group (container) (typed FeaturePython)
  n = 16
  ref = H_element
FEATURE [App::DocumentObjectGroupPython] G4_N_HEPTANE  label="G4_N-HEPTANE"  # scripted group (container) (typed FeaturePython)
  Dunit = g/cm3
  Dvalue = 0.68376
  Group = -> [C_element052,H_element046]
  conduct = 2
  density = 1
  expand = 3
  formula = G4_N-HEPTANE
  name = G4_N-HEPTANE
  specific = 4
FEATURE [App::DocumentObjectGroupPython] C_element053  label="C_element : 029"  # scripted group (container) (typed FeaturePython)
  n = 6
  ref = C_element
FEATURE [App::DocumentObjectGroupPython] H_element047  label="H_element : 14"  # scripted group (container) (typed FeaturePython)
  n = 14
  ref = H_element
FEATURE [App::DocumentObjectGroupPython] G4_N_HEXANE  label="G4_N-HEXANE"  # scripted group (container) (typed FeaturePython)
  Dunit = g/cm3
  Dvalue = 0.6603
  Group = -> [C_element053,H_element047]
  conduct = 2
  density = 1
  expand = 3
  formula = G4_N-HEXANE
  name = G4_N-HEXANE
  specific = 4
FEATURE [App::DocumentObjectGroupPython] C_element054  label="C_element : 22"  # scripted group (container) (typed FeaturePython)
  n = 22
  ref = C_element
FEATURE [App::DocumentObjectGroupPython] H_element048  label="H_element : 025"  # scripted group (container) (typed FeaturePython)
  n = 10
  ref = H_element
FEATURE [App::DocumentObjectGroupPython] N_element021  label="N_element : 010"  # scripted group (container) (typed FeaturePython)
  n = 2
  ref = N_element
FEATURE [App::DocumentObjectGroupPython] O_element050  label="O_element : 025"  # scripted group (container) (typed FeaturePython)
  n = 5
  ref = O_element
FEATURE [App::DocumentObjectGroupPython] G4_KAPTON  # scripted group (container) (typed FeaturePython)
  Dunit = g/cm3
  Dvalue = 1.42
  Group = -> [C_element054,H_element048,N_element021,O_element050]
  conduct = 2
  density = 1
  expand = 3
  formula = G4_KAPTON
  name = G4_KAPTON
  specific = 4
FEATURE [App::DocumentObjectGroupPython] La_element001  label="La_element : 1"  # scripted group (container) (typed FeaturePython)
  n = 1
  ref = La_element
FEATURE [App::DocumentObjectGroupPython] Br_element003  label="Br_element : 002"  # scripted group (container) (typed FeaturePython)
  n = 1
  ref = Br_element
FEATURE [App::DocumentObjectGroupPython] O_element051  label="O_element : 026"  # scripted group (container) (typed FeaturePython)
  n = 1
  ref = O_element
FEATURE [App::DocumentObjectGroupPython] G4_LANTHANUM_OXYBROMIDE  # scripted group (container) (typed FeaturePython)
  Dunit = g/cm3
  Dvalue = 6.28
  Group = -> [La_element001,Br_element003,O_element051]
  conduct = 2
  density = 1
  expand = 3
  formula = G4_LANTHANUM_OXYBROMIDE
  name = G4_LANTHANUM_OXYBROMIDE
  specific = 4
FEATURE [App::DocumentObjectGroupPython] La_element002  label="La_element : 2"  # scripted group (container) (typed FeaturePython)
  n = 2
  ref = La_element
FEATURE [App::DocumentObjectGroupPython] O_element052  label="O_element : 027"  # scripted group (container) (typed FeaturePython)
  n = 2
  ref = O_element
FEATURE [App::DocumentObjectGroupPython] S_element015  label="S_element : 006"  # scripted group (container) (typed FeaturePython)
  n = 1
  ref = S_element
FEATURE [App::DocumentObjectGroupPython] G4_LANTHANUM_OXYSULFIDE  # scripted group (container) (typed FeaturePython)
  Dunit = g/cm3
  Dvalue = 5.86
  Group = -> [La_element002,O_element052,S_element015]
  conduct = 2
  density = 1
  expand = 3
  formula = G4_LANTHANUM_OXYSULFIDE
  name = G4_LANTHANUM_OXYSULFIDE
  specific = 4
FEATURE [App::DocumentObjectGroupPython] O_element053  label="O_element : 0.072"  # scripted group (container) (typed FeaturePython)
  n = 0.071682
FEATURE [App::DocumentObjectGroupPython] Pb_element002  label="Pb_element : 0.928"  # scripted group (container) (typed FeaturePython)
  n = 0.928318
FEATURE [App::DocumentObjectGroupPython] G4_LEAD_OXIDE  # scripted group (container) (typed FeaturePython)
  Dunit = g/cm3
  Dvalue = 9.53
  Group = -> [O_element053,Pb_element002]
  conduct = 2
  density = 1
  expand = 3
  formula = G4_LEAD_OXIDE
  name = G4_LEAD_OXIDE
  specific = 4
FEATURE [App::DocumentObjectGroupPython] Li_element001  label="Li_element : 1"  # scripted group (container) (typed FeaturePython)
  n = 1
  ref = Li_element
FEATURE [App::DocumentObjectGroupPython] N_element022  label="N_element : 011"  # scripted group (container) (typed FeaturePython)
  n = 1
  ref = N_element
FEATURE [App::DocumentObjectGroupPython] H_element049  label="H_element : 026"  # scripted group (container) (typed FeaturePython)
  n = 2
  ref = H_element
FEATURE [App::DocumentObjectGroupPython] G4_LITHIUM_AMIDE  # scripted group (container) (typed FeaturePython)
  Dunit = g/cm3
  Dvalue = 1.178
  Group = -> [Li_element001,N_element022,H_element049]
  conduct = 2
  density = 1
  expand = 3
  formula = G4_LITHIUM_AMIDE
  name = G4_LITHIUM_AMIDE
  specific = 4
FEATURE [App::DocumentObjectGroupPython] Li_element002  label="Li_element : 2"  # scripted group (container) (typed FeaturePython)
  n = 2
  ref = Li_element
FEATURE [App::DocumentObjectGroupPython] C_element055  label="C_element : 030"  # scripted group (container) (typed FeaturePython)
  n = 1
  ref = C_element
FEATURE [App::DocumentObjectGroupPython] O_element054  label="O_element : 028"  # scripted group (container) (typed FeaturePython)
  n = 3
  ref = O_element
FEATURE [App::DocumentObjectGroupPython] G4_LITHIUM_CARBONATE  # scripted group (container) (typed FeaturePython)
  Dunit = g/cm3
  Dvalue = 2.11
  Group = -> [Li_element002,C_element055,O_element054]
  conduct = 2
  density = 1
  expand = 3
  formula = G4_LITHIUM_CARBONATE
  name = G4_LITHIUM_CARBONATE
  specific = 4
FEATURE [App::DocumentObjectGroupPython] Li_element003  label="Li_element : 003"  # scripted group (container) (typed FeaturePython)
  n = 1
  ref = Li_element
FEATURE [App::DocumentObjectGroupPython] F_element012  label="F_element : 004"  # scripted group (container) (typed FeaturePython)
  n = 1
  ref = F_element
FEATURE [App::DocumentObjectGroupPython] G4_LITHIUM_FLUORIDE  # scripted group (container) (typed FeaturePython)
  Dunit = g/cm3
  Dvalue = 2.635
  Group = -> [Li_element003,F_element012]
  conduct = 2
  density = 1
  expand = 3
  formula = G4_LITHIUM_FLUORIDE
  name = G4_LITHIUM_FLUORIDE
  specific = 4
FEATURE [App::DocumentObjectGroupPython] Li_element004  label="Li_element : 004"  # scripted group (container) (typed FeaturePython)
  n = 1
  ref = Li_element
FEATURE [App::DocumentObjectGroupPython] H_element050  label="H_element : 027"  # scripted group (container) (typed FeaturePython)
  n = 1
  ref = H_element
FEATURE [App::DocumentObjectGroupPython] G4_LITHIUM_HYDRIDE  # scripted group (container) (typed FeaturePython)
  Dunit = g/cm3
  Dvalue = 0.82
  Group = -> [Li_element004,H_element050]
  conduct = 2
  density = 1
  expand = 3
  formula = G4_LITHIUM_HYDRIDE
  name = G4_LITHIUM_HYDRIDE
  specific = 4
FEATURE [App::DocumentObjectGroupPython] Li_element005  label="Li_element : 005"  # scripted group (container) (typed FeaturePython)
  n = 1
  ref = Li_element
FEATURE [App::DocumentObjectGroupPython] I_element003  label="I_element : 002"  # scripted group (container) (typed FeaturePython)
  n = 1
  ref = I_element
FEATURE [App::DocumentObjectGroupPython] G4_LITHIUM_IODIDE  # scripted group (container) (typed FeaturePython)
  Dunit = g/cm3
  Dvalue = 3.494
  Group = -> [Li_element005,I_element003]
  conduct = 2
  density = 1
  expand = 3
  formula = G4_LITHIUM_IODIDE
  name = G4_LITHIUM_IODIDE
  specific = 4
FEATURE [App::DocumentObjectGroupPython] Li_element006  label="Li_element : 006"  # scripted group (container) (typed FeaturePython)
  n = 2
  ref = Li_element
FEATURE [App::DocumentObjectGroupPython] O_element055  label="O_element : 029"  # scripted group (container) (typed FeaturePython)
  n = 1
  ref = O_element
FEATURE [App::DocumentObjectGroupPython] G4_LITHIUM_OXIDE  # scripted group (container) (typed FeaturePython)
  Dunit = g/cm3
  Dvalue = 2.013
  Group = -> [Li_element006,O_element055]
  conduct = 2
  density = 1
  expand = 3
  formula = G4_LITHIUM_OXIDE
  name = G4_LITHIUM_OXIDE
  specific = 4
FEATURE [App::DocumentObjectGroupPython] Li_element007  label="Li_element : 007"  # scripted group (container) (typed FeaturePython)
  n = 2
  ref = Li_element
FEATURE [App::DocumentObjectGroupPython] B_element005  label="B_element : 005"  # scripted group (container) (typed FeaturePython)
  n = 4
  ref = B_element
FEATURE [App::DocumentObjectGroupPython] O_element056  label="O_element : 7"  # scripted group (container) (typed FeaturePython)
  n = 7
  ref = O_element
FEATURE [App::DocumentObjectGroupPython] G4_LITHIUM_TETRABORATE  # scripted group (container) (typed FeaturePython)
  Dunit = g/cm3
  Dvalue = 2.44
  Group = -> [Li_element007,B_element005,O_element056]
  conduct = 2
  density = 1
  expand = 3
  formula = G4_LITHIUM_TETRABORATE
  name = G4_LITHIUM_TETRABORATE
  specific = 4
FEATURE [App::DocumentObjectGroupPython] H_element051  label="H_element : 0.105"  # scripted group (container) (typed FeaturePython)
  n = 0.105
FEATURE [App::DocumentObjectGroupPython] C_element056  label="C_element : 0.083"  # scripted group (container) (typed FeaturePython)
  n = 0.083
FEATURE [App::DocumentObjectGroupPython] N_element023  label="N_element : 0.023"  # scripted group (container) (typed FeaturePython)
  n = 0.023
FEATURE [App::DocumentObjectGroupPython] O_element057  label="O_element : 0.779"  # scripted group (container) (typed FeaturePython)
  n = 0.779
FEATURE [App::DocumentObjectGroupPython] Na_element010  label="Na_element : 0.097"  # scripted group (container) (typed FeaturePython)
  n = 0.002
FEATURE [App::DocumentObjectGroupPython] P_element006  label="P_element : 0.105"  # scripted group (container) (typed FeaturePython)
  n = 0.001
FEATURE [App::DocumentObjectGroupPython] S_element016  label="S_element : 0.017"  # scripted group (container) (typed FeaturePython)
  n = 0.002
FEATURE [App::DocumentObjectGroupPython] Cl_element014  label="Cl_element : 0.587"  # scripted group (container) (typed FeaturePython)
  n = 0.003
FEATURE [App::DocumentObjectGroupPython] K_element005  label="K_element : 0.015"  # scripted group (container) (typed FeaturePython)
  n = 0.002
FEATURE [App::DocumentObjectGroupPython] G4_LUNG_ICRP  # scripted group (container) (typed FeaturePython)
  Dunit = g/cm3
  Dvalue = 1.04
  Group = -> [H_element051,C_element056,N_element023,O_element057,Na_element010,P_element006,S_element016,Cl_element014,K_element005]
  conduct = 2
  density = 1
  expand = 3
  formula = G4_LUNG_ICRP
  name = G4_LUNG_ICRP
  specific = 4
FEATURE [App::DocumentObjectGroupPython] H_element052  label="H_element : 0.116"  # scripted group (container) (typed FeaturePython)
  n = 0.114318
FEATURE [App::DocumentObjectGroupPython] C_element057  label="C_element : 0.656"  # scripted group (container) (typed FeaturePython)
  n = 0.655824
FEATURE [App::DocumentObjectGroupPython] O_element058  label="O_element : 0.092"  # scripted group (container) (typed FeaturePython)
  n = 0.0921831
FEATURE [App::DocumentObjectGroupPython] Mg_element004  label="Mg_element : 0.135"  # scripted group (container) (typed FeaturePython)
  n = 0.134792
FEATURE [App::DocumentObjectGroupPython] Ca_element013  label="Ca_element : 0.003"  # scripted group (container) (typed FeaturePython)
  n = 0.002883
FEATURE [App::DocumentObjectGroupPython] G4_M3_WAX  # scripted group (container) (typed FeaturePython)
  Dunit = g/cm3
  Dvalue = 1.05
  Group = -> [H_element052,C_element057,O_element058,Mg_element004,Ca_element013]
  conduct = 2
  density = 1
  expand = 3
  formula = G4_M3_WAX
  name = G4_M3_WAX
  specific = 4
FEATURE [App::DocumentObjectGroupPython] Mg_element005  label="Mg_element : 1"  # scripted group (container) (typed FeaturePython)
  n = 1
  ref = Mg_element
FEATURE [App::DocumentObjectGroupPython] C_element058  label="C_element : 031"  # scripted group (container) (typed FeaturePython)
  n = 1
  ref = C_element
FEATURE [App::DocumentObjectGroupPython] O_element059  label="O_element : 030"  # scripted group (container) (typed FeaturePython)
  n = 3
  ref = O_element
FEATURE [App::DocumentObjectGroupPython] G4_MAGNESIUM_CARBONATE  # scripted group (container) (typed FeaturePython)
  Dunit = g/cm3
  Dvalue = 2.958
  Group = -> [Mg_element005,C_element058,O_element059]
  conduct = 2
  density = 1
  expand = 3
  formula = G4_MAGNESIUM_CARBONATE
  name = G4_MAGNESIUM_CARBONATE
  specific = 4
FEATURE [App::DocumentObjectGroupPython] Mg_element006  label="Mg_element : 002"  # scripted group (container) (typed FeaturePython)
  n = 1
  ref = Mg_element
FEATURE [App::DocumentObjectGroupPython] F_element013  label="F_element : 005"  # scripted group (container) (typed FeaturePython)
  n = 2
  ref = F_element
FEATURE [App::DocumentObjectGroupPython] G4_MAGNESIUM_FLUORIDE  # scripted group (container) (typed FeaturePython)
  Dunit = g/cm3
  Dvalue = 3
  Group = -> [Mg_element006,F_element013]
  conduct = 2
  density = 1
  expand = 3
  formula = G4_MAGNESIUM_FLUORIDE
  name = G4_MAGNESIUM_FLUORIDE
  specific = 4
FEATURE [App::DocumentObjectGroupPython] Mg_element007  label="Mg_element : 003"  # scripted group (container) (typed FeaturePython)
  n = 1
  ref = Mg_element
FEATURE [App::DocumentObjectGroupPython] O_element060  label="O_element : 031"  # scripted group (container) (typed FeaturePython)
  n = 1
  ref = O_element
FEATURE [App::DocumentObjectGroupPython] G4_MAGNESIUM_OXIDE  # scripted group (container) (typed FeaturePython)
  Dunit = g/cm3
  Dvalue = 3.58
  Group = -> [Mg_element007,O_element060]
  conduct = 2
  density = 1
  expand = 3
  formula = G4_MAGNESIUM_OXIDE
  name = G4_MAGNESIUM_OXIDE
  specific = 4
FEATURE [App::DocumentObjectGroupPython] Mg_element008  label="Mg_element : 004"  # scripted group (container) (typed FeaturePython)
  n = 1
  ref = Mg_element
FEATURE [App::DocumentObjectGroupPython] B_element006  label="B_element : 006"  # scripted group (container) (typed FeaturePython)
  n = 4
  ref = B_element
FEATURE [App::DocumentObjectGroupPython] O_element061  label="O_element : 032"  # scripted group (container) (typed FeaturePython)
  n = 7
  ref = O_element
FEATURE [App::DocumentObjectGroupPython] G4_MAGNESIUM_TETRABORATE  # scripted group (container) (typed FeaturePython)
  Dunit = g/cm3
  Dvalue = 2.53
  Group = -> [Mg_element008,B_element006,O_element061]
  conduct = 2
  density = 1
  expand = 3
  formula = G4_MAGNESIUM_TETRABORATE
  name = G4_MAGNESIUM_TETRABORATE
  specific = 4
FEATURE [App::DocumentObjectGroupPython] Hg_element001  label="Hg_element : 1"  # scripted group (container) (typed FeaturePython)
  n = 1
  ref = Hg_element
FEATURE [App::DocumentObjectGroupPython] I_element004  label="I_element : 2"  # scripted group (container) (typed FeaturePython)
  n = 2
  ref = I_element
FEATURE [App::DocumentObjectGroupPython] G4_MERCURIC_IODIDE  # scripted group (container) (typed FeaturePython)
  Dunit = g/cm3
  Dvalue = 6.36
  Group = -> [Hg_element001,I_element004]
  conduct = 2
  density = 1
  expand = 3
  formula = G4_MERCURIC_IODIDE
  name = G4_MERCURIC_IODIDE
  specific = 4
FEATURE [App::DocumentObjectGroupPython] C_element059  label="C_element : 032"  # scripted group (container) (typed FeaturePython)
  n = 1
  ref = C_element
FEATURE [App::DocumentObjectGroupPython] H_element053  label="H_element : 028"  # scripted group (container) (typed FeaturePython)
  n = 4
  ref = H_element
FEATURE [App::DocumentObjectGroupPython] G4_METHANE  # scripted group (container) (typed FeaturePython)
  Dunit = g/cm3
  Dvalue = 0.000667151
  Group = -> [C_element059,H_element053]
  conduct = 2
  density = 1
  expand = 3
  formula = G4_METHANE
  name = G4_METHANE
  specific = 4
FEATURE [App::DocumentObjectGroupPython] C_element060  label="C_element : 033"  # scripted group (container) (typed FeaturePython)
  n = 1
  ref = C_element
FEATURE [App::DocumentObjectGroupPython] H_element054  label="H_element : 029"  # scripted group (container) (typed FeaturePython)
  n = 4
  ref = H_element
FEATURE [App::DocumentObjectGroupPython] O_element062  label="O_element : 033"  # scripted group (container) (typed FeaturePython)
  n = 1
  ref = O_element
FEATURE [App::DocumentObjectGroupPython] G4_METHANOL  # scripted group (container) (typed FeaturePython)
  Dunit = g/cm3
  Dvalue = 0.7914
  Group = -> [C_element060,H_element054,O_element062]
  conduct = 2
  density = 1
  expand = 3
  formula = G4_METHANOL
  name = G4_METHANOL
  specific = 4
FEATURE [App::DocumentObjectGroupPython] H_element055  label="H_element : 0.134"  # scripted group (container) (typed FeaturePython)
  n = 0.13404
FEATURE [App::DocumentObjectGroupPython] C_element061  label="C_element : 0.778"  # scripted group (container) (typed FeaturePython)
  n = 0.77796
FEATURE [App::DocumentObjectGroupPython] O_element063  label="O_element : 0.035"  # scripted group (container) (typed FeaturePython)
  n = 0.03502
FEATURE [App::DocumentObjectGroupPython] Mg_element009  label="Mg_element : 0.039"  # scripted group (container) (typed FeaturePython)
  n = 0.038594
FEATURE [App::DocumentObjectGroupPython] Ti_element002  label="Ti_element : 0.014"  # scripted group (container) (typed FeaturePython)
  n = 0.014386
FEATURE [App::DocumentObjectGroupPython] G4_MIX_D_WAX  # scripted group (container) (typed FeaturePython)
  Dunit = g/cm3
  Dvalue = 0.99
  Group = -> [H_element055,C_element061,O_element063,Mg_element009,Ti_element002]
  conduct = 2
  density = 1
  expand = 3
  formula = G4_MIX_D_WAX
  name = G4_MIX_D_WAX
  specific = 4
FEATURE [App::DocumentObjectGroupPython] H_element056  label="H_element : 0.135"  # scripted group (container) (typed FeaturePython)
  n = 0.081192
FEATURE [App::DocumentObjectGroupPython] C_element062  label="C_element : 0.583"  # scripted group (container) (typed FeaturePython)
  n = 0.583442
FEATURE [App::DocumentObjectGroupPython] N_element024  label="N_element : 0.018"  # scripted group (container) (typed FeaturePython)
  n = 0.017798
FEATURE [App::DocumentObjectGroupPython] O_element064  label="O_element : 0.186"  # scripted group (container) (typed FeaturePython)
  n = 0.186381
FEATURE [App::DocumentObjectGroupPython] Mg_element010  label="Mg_element : 0.130"  # scripted group (container) (typed FeaturePython)
  n = 0.130287
FEATURE [App::DocumentObjectGroupPython] Cl_element015  label="Cl_element : 0.588"  # scripted group (container) (typed FeaturePython)
  n = 0.0009
FEATURE [App::DocumentObjectGroupPython] G4_MS20_TISSUE  # scripted group (container) (typed FeaturePython)
  Dunit = g/cm3
  Dvalue = 1
  Group = -> [H_element056,C_element062,N_element024,O_element064,Mg_element010,Cl_element015]
  conduct = 2
  density = 1
  expand = 3
  formula = G4_MS20_TISSUE
  name = G4_MS20_TISSUE
  specific = 4
FEATURE [App::DocumentObjectGroupPython] H_element057  label="H_element : 0.136"  # scripted group (container) (typed FeaturePython)
  n = 0.102
FEATURE [App::DocumentObjectGroupPython] C_element063  label="C_element : 0.143"  # scripted group (container) (typed FeaturePython)
  n = 0.143
FEATURE [App::DocumentObjectGroupPython] N_element025  label="N_element : 0.034"  # scripted group (container) (typed FeaturePython)
  n = 0.034
FEATURE [App::DocumentObjectGroupPython] O_element065  label="O_element : 0.710"  # scripted group (container) (typed FeaturePython)
  n = 0.71
FEATURE [App::DocumentObjectGroupPython] Na_element011  label="Na_element : 0.098"  # scripted group (container) (typed FeaturePython)
  n = 0.001
FEATURE [App::DocumentObjectGroupPython] P_element007  label="P_element : 0.002"  # scripted group (container) (typed FeaturePython)
  n = 0.002
FEATURE [App::DocumentObjectGroupPython] S_element017  label="S_element : 0.018"  # scripted group (container) (typed FeaturePython)
  n = 0.003
FEATURE [App::DocumentObjectGroupPython] Cl_element016  label="Cl_element : 0.589"  # scripted group (container) (typed FeaturePython)
  n = 0.001
FEATURE [App::DocumentObjectGroupPython] K_element006  label="K_element : 0.004"  # scripted group (container) (typed FeaturePython)
  n = 0.004
FEATURE [App::DocumentObjectGroupPython] G4_MUSCLE_SKELETAL_ICRP  # scripted group (container) (typed FeaturePython)
  Dunit = g/cm3
  Dvalue = 1.05
  Group = -> [H_element057,C_element063,N_element025,O_element065,Na_element011,P_element007,S_element017,Cl_element016,K_element006]
  conduct = 2
  density = 1
  expand = 3
  formula = G4_MUSCLE_SKELETAL_ICRP
  name = G4_MUSCLE_SKELETAL_ICRP
  specific = 4
FEATURE [App::DocumentObjectGroupPython] H_element058  label="H_element : 0.137"  # scripted group (container) (typed FeaturePython)
  n = 0.102102
FEATURE [App::DocumentObjectGroupPython] C_element064  label="C_element : 0.123"  # scripted group (container) (typed FeaturePython)
  n = 0.123123
FEATURE [App::DocumentObjectGroupPython] N_element026  label="N_element : 0.756"  # scripted group (container) (typed FeaturePython)
  n = 0.035035
FEATURE [App::DocumentObjectGroupPython] O_element066  label="O_element : 0.730"  # scripted group (container) (typed FeaturePython)
  n = 0.72973
FEATURE [App::DocumentObjectGroupPython] Na_element012  label="Na_element : 0.099"  # scripted group (container) (typed FeaturePython)
  n = 0.001001
FEATURE [App::DocumentObjectGroupPython] P_element008  label="P_element : 0.106"  # scripted group (container) (typed FeaturePython)
  n = 0.002002
FEATURE [App::DocumentObjectGroupPython] S_element018  label="S_element : 0.019"  # scripted group (container) (typed FeaturePython)
  n = 0.004004
FEATURE [App::DocumentObjectGroupPython] K_element007  label="K_element : 0.016"  # scripted group (container) (typed FeaturePython)
  n = 0.003003
FEATURE [App::DocumentObjectGroupPython] G4_MUSCLE_STRIATED_ICRU  # scripted group (container) (typed FeaturePython)
  Dunit = g/cm3
  Dvalue = 1.04
  Group = -> [H_element058,C_element064,N_element026,O_element066,Na_element012,P_element008,S_element018,K_element007]
  conduct = 2
  density = 1
  expand = 3
  formula = G4_MUSCLE_STRIATED_ICRU
  name = G4_MUSCLE_STRIATED_ICRU
  specific = 4
FEATURE [App::DocumentObjectGroupPython] H_element059  label="H_element : 0.098"  # scripted group (container) (typed FeaturePython)
  n = 0.0982341
FEATURE [App::DocumentObjectGroupPython] C_element065  label="C_element : 0.156"  # scripted group (container) (typed FeaturePython)
  n = 0.156214
FEATURE [App::DocumentObjectGroupPython] N_element027  label="N_element : 0.757"  # scripted group (container) (typed FeaturePython)
  n = 0.035451
FEATURE [App::DocumentObjectGroupPython] O_element067  label="O_element : 0.880"  # scripted group (container) (typed FeaturePython)
  n = 0.710101
FEATURE [App::DocumentObjectGroupPython] G4_MUSCLE_WITH_SUCROSE  # scripted group (container) (typed FeaturePython)
  Dunit = g/cm3
  Dvalue = 1.11
  Group = -> [H_element059,C_element065,N_element027,O_element067]
  conduct = 2
  density = 1
  expand = 3
  formula = G4_MUSCLE_WITH_SUCROSE
  name = G4_MUSCLE_WITH_SUCROSE
  specific = 4
FEATURE [App::DocumentObjectGroupPython] H_element060  label="H_element : 0.138"  # scripted group (container) (typed FeaturePython)
  n = 0.101969
FEATURE [App::DocumentObjectGroupPython] C_element066  label="C_element : 0.120"  # scripted group (container) (typed FeaturePython)
  n = 0.120058
FEATURE [App::DocumentObjectGroupPython] N_element028  label="N_element : 0.758"  # scripted group (container) (typed FeaturePython)
  n = 0.035451
FEATURE [App::DocumentObjectGroupPython] O_element068  label="O_element : 0.743"  # scripted group (container) (typed FeaturePython)
  n = 0.742522
FEATURE [App::DocumentObjectGroupPython] G4_MUSCLE_WITHOUT_SUCROSE  # scripted group (container) (typed FeaturePython)
  Dunit = g/cm3
  Dvalue = 1.07
  Group = -> [H_element060,C_element066,N_element028,O_element068]
  conduct = 2
  density = 1
  expand = 3
  formula = G4_MUSCLE_WITHOUT_SUCROSE
  name = G4_MUSCLE_WITHOUT_SUCROSE
  specific = 4
FEATURE [App::DocumentObjectGroupPython] C_element067  label="C_element : 10"  # scripted group (container) (typed FeaturePython)
  n = 10
  ref = C_element
FEATURE [App::DocumentObjectGroupPython] H_element061  label="H_element : 030"  # scripted group (container) (typed FeaturePython)
  n = 8
  ref = H_element
FEATURE [App::DocumentObjectGroupPython] G4_NAPHTHALENE  # scripted group (container) (typed FeaturePython)
  Dunit = g/cm3
  Dvalue = 1.145
  Group = -> [C_element067,H_element061]
  conduct = 2
  density = 1
  expand = 3
  formula = G4_NAPHTHALENE
  name = G4_NAPHTHALENE
  specific = 4
FEATURE [App::DocumentObjectGroupPython] C_element068  label="C_element : 034"  # scripted group (container) (typed FeaturePython)
  n = 6
  ref = C_element
FEATURE [App::DocumentObjectGroupPython] H_element062  label="H_element : 031"  # scripted group (container) (typed FeaturePython)
  n = 5
  ref = H_element
FEATURE [App::DocumentObjectGroupPython] N_element029  label="N_element : 012"  # scripted group (container) (typed FeaturePython)
  n = 1
  ref = N_element
FEATURE [App::DocumentObjectGroupPython] O_element069  label="O_element : 034"  # scripted group (container) (typed FeaturePython)
  n = 2
  ref = O_element
FEATURE [App::DocumentObjectGroupPython] G4_NITROBENZENE  # scripted group (container) (typed FeaturePython)
  Dunit = g/cm3
  Dvalue = 1.19867
  Group = -> [C_element068,H_element062,N_element029,O_element069]
  conduct = 2
  density = 1
  expand = 3
  formula = G4_NITROBENZENE
  name = G4_NITROBENZENE
  specific = 4
FEATURE [App::DocumentObjectGroupPython] N_element030  label="N_element : 013"  # scripted group (container) (typed FeaturePython)
  n = 2
  ref = N_element
FEATURE [App::DocumentObjectGroupPython] O_element070  label="O_element : 035"  # scripted group (container) (typed FeaturePython)
  n = 1
  ref = O_element
FEATURE [App::DocumentObjectGroupPython] G4_NITROUS_OXIDE  # scripted group (container) (typed FeaturePython)
  Dunit = g/cm3
  Dvalue = 0.00183094
  Group = -> [N_element030,O_element070]
  conduct = 2
  density = 1
  expand = 3
  formula = G4_NITROUS_OXIDE
  name = G4_NITROUS_OXIDE
  specific = 4
FEATURE [App::DocumentObjectGroupPython] H_element063  label="H_element : 0.104"  # scripted group (container) (typed FeaturePython)
  n = 0.103509
FEATURE [App::DocumentObjectGroupPython] C_element069  label="C_element : 0.648"  # scripted group (container) (typed FeaturePython)
  n = 0.648416
FEATURE [App::DocumentObjectGroupPython] N_element031  label="N_element : 0.100"  # scripted group (container) (typed FeaturePython)
  n = 0.0995361
FEATURE [App::DocumentObjectGroupPython] O_element071  label="O_element : 0.149"  # scripted group (container) (typed FeaturePython)
  n = 0.148539
FEATURE [App::DocumentObjectGroupPython] G4_NYLON_8062  label="G4_NYLON-8062"  # scripted group (container) (typed FeaturePython)
  Dunit = g/cm3
  Dvalue = 1.08
  Group = -> [H_element063,C_element069,N_element031,O_element071]
  conduct = 2
  density = 1
  expand = 3
  formula = G4_NYLON-8062
  name = G4_NYLON-8062
  specific = 4
FEATURE [App::DocumentObjectGroupPython] C_element070  label="C_element : 035"  # scripted group (container) (typed FeaturePython)
  n = 6
  ref = C_element
FEATURE [App::DocumentObjectGroupPython] H_element064  label="H_element : 11"  # scripted group (container) (typed FeaturePython)
  n = 11
  ref = H_element
FEATURE [App::DocumentObjectGroupPython] N_element032  label="N_element : 014"  # scripted group (container) (typed FeaturePython)
  n = 1
  ref = N_element
FEATURE [App::DocumentObjectGroupPython] O_element072  label="O_element : 036"  # scripted group (container) (typed FeaturePython)
  n = 1
  ref = O_element
FEATURE [App::DocumentObjectGroupPython] G4_NYLON_6_6  label="G4_NYLON-6-6"  # scripted group (container) (typed FeaturePython)
  Dunit = g/cm3
  Dvalue = 1.14
  Group = -> [C_element070,H_element064,N_element032,O_element072]
  conduct = 2
  density = 1
  expand = 3
  formula = G4_NYLON-6-6
  name = G4_NYLON-6-6
  specific = 4
FEATURE [App::DocumentObjectGroupPython] H_element065  label="H_element : 0.139"  # scripted group (container) (typed FeaturePython)
  n = 0.107062
FEATURE [App::DocumentObjectGroupPython] C_element071  label="C_element : 0.680"  # scripted group (container) (typed FeaturePython)
  n = 0.680449
FEATURE [App::DocumentObjectGroupPython] N_element033  label="N_element : 0.099"  # scripted group (container) (typed FeaturePython)
  n = 0.099189
FEATURE [App::DocumentObjectGroupPython] O_element073  label="O_element : 0.113"  # scripted group (container) (typed FeaturePython)
  n = 0.1133
FEATURE [App::DocumentObjectGroupPython] G4_NYLON_6_10  label="G4_NYLON-6-10"  # scripted group (container) (typed FeaturePython)
  Dunit = g/cm3
  Dvalue = 1.14
  Group = -> [H_element065,C_element071,N_element033,O_element073]
  conduct = 2
  density = 1
  expand = 3
  formula = G4_NYLON-6-10
  name = G4_NYLON-6-10
  specific = 4
FEATURE [App::DocumentObjectGroupPython] H_element066  label="H_element : 0.140"  # scripted group (container) (typed FeaturePython)
  n = 0.115476
FEATURE [App::DocumentObjectGroupPython] C_element072  label="C_element : 0.721"  # scripted group (container) (typed FeaturePython)
  n = 0.720818
FEATURE [App::DocumentObjectGroupPython] N_element034  label="N_element : 0.076"  # scripted group (container) (typed FeaturePython)
  n = 0.0764169
FEATURE [App::DocumentObjectGroupPython] O_element074  label="O_element : 0.087"  # scripted group (container) (typed FeaturePython)
  n = 0.0872889
FEATURE [App::DocumentObjectGroupPython] G4_NYLON_11_RILSAN  label="G4_NYLON-11_RILSAN"  # scripted group (container) (typed FeaturePython)
  Dunit = g/cm3
  Dvalue = 1.425
  Group = -> [H_element066,C_element072,N_element034,O_element074]
  conduct = 2
  density = 1
  expand = 3
  formula = G4_NYLON-11_RILSAN
  name = G4_NYLON-11_RILSAN
  specific = 4
FEATURE [App::DocumentObjectGroupPython] C_element073  label="C_element : 8"  # scripted group (container) (typed FeaturePython)
  n = 8
  ref = C_element
FEATURE [App::DocumentObjectGroupPython] H_element067  label="H_element : 18"  # scripted group (container) (typed FeaturePython)
  n = 18
  ref = H_element
FEATURE [App::DocumentObjectGroupPython] G4_OCTANE  # scripted group (container) (typed FeaturePython)
  Dunit = g/cm3
  Dvalue = 0.7026
  Group = -> [C_element073,H_element067]
  conduct = 2
  density = 1
  expand = 3
  formula = G4_OCTANE
  name = G4_OCTANE
  specific = 4
FEATURE [App::DocumentObjectGroupPython] C_element074  label="C_element : 25"  # scripted group (container) (typed FeaturePython)
  n = 25
  ref = C_element
FEATURE [App::DocumentObjectGroupPython] H_element068  label="H_element : 52"  # scripted group (container) (typed FeaturePython)
  n = 52
  ref = H_element
FEATURE [App::DocumentObjectGroupPython] G4_PARAFFIN  # scripted group (container) (typed FeaturePython)
  Dunit = g/cm3
  Dvalue = 0.93
  Group = -> [C_element074,H_element068]
  conduct = 2
  density = 1
  expand = 3
  formula = G4_PARAFFIN
  name = G4_PARAFFIN
  specific = 4
FEATURE [App::DocumentObjectGroupPython] C_element075  label="C_element : 036"  # scripted group (container) (typed FeaturePython)
  n = 5
  ref = C_element
FEATURE [App::DocumentObjectGroupPython] H_element069  label="H_element : 032"  # scripted group (container) (typed FeaturePython)
  n = 12
  ref = H_element
FEATURE [App::DocumentObjectGroupPython] G4_N_PENTANE  label="G4_N-PENTANE"  # scripted group (container) (typed FeaturePython)
  Dunit = g/cm3
  Dvalue = 0.6262
  Group = -> [C_element075,H_element069]
  conduct = 2
  density = 1
  expand = 3
  formula = G4_N-PENTANE
  name = G4_N-PENTANE
  specific = 4
FEATURE [App::DocumentObjectGroupPython] H_element070  label="H_element : 0.014"  # scripted group (container) (typed FeaturePython)
  n = 0.0141
FEATURE [App::DocumentObjectGroupPython] C_element076  label="C_element : 0.072"  # scripted group (container) (typed FeaturePython)
  n = 0.072261
FEATURE [App::DocumentObjectGroupPython] N_element035  label="N_element : 0.019"  # scripted group (container) (typed FeaturePython)
  n = 0.01932
FEATURE [App::DocumentObjectGroupPython] O_element075  label="O_element : 0.066"  # scripted group (container) (typed FeaturePython)
  n = 0.066101
FEATURE [App::DocumentObjectGroupPython] S_element019  label="S_element : 0.020"  # scripted group (container) (typed FeaturePython)
  n = 0.00189
FEATURE [App::DocumentObjectGroupPython] Br_element004  label="Br_element : 0.349"  # scripted group (container) (typed FeaturePython)
  n = 0.349103
FEATURE [App::DocumentObjectGroupPython] Ag_element001  label="Ag_element : 0.474"  # scripted group (container) (typed FeaturePython)
  n = 0.474105
FEATURE [App::DocumentObjectGroupPython] I_element005  label="I_element : 0.003"  # scripted group (container) (typed FeaturePython)
  n = 0.00312
FEATURE [App::DocumentObjectGroupPython] G4_PHOTO_EMULSION  # scripted group (container) (typed FeaturePython)
  Dunit = g/cm3
  Dvalue = 3.815
  Group = -> [H_element070,C_element076,N_element035,O_element075,S_element019,Br_element004,Ag_element001,I_element005]
  conduct = 2
  density = 1
  expand = 3
  formula = G4_PHOTO_EMULSION
  name = G4_PHOTO_EMULSION
  specific = 4
FEATURE [App::DocumentObjectGroupPython] C_element077  label="C_element : 9"  # scripted group (container) (typed FeaturePython)
  n = 9
  ref = C_element
FEATURE [App::DocumentObjectGroupPython] H_element071  label="H_element : 033"  # scripted group (container) (typed FeaturePython)
  n = 10
  ref = H_element
FEATURE [App::DocumentObjectGroupPython] G4_PLASTIC_SC_VINYLTOLUENE  # scripted group (container) (typed FeaturePython)
  Dunit = g/cm3
  Dvalue = 1.032
  Group = -> [C_element077,H_element071]
  conduct = 2
  density = 1
  expand = 3
  formula = G4_PLASTIC_SC_VINYLTOLUENE
  name = G4_PLASTIC_SC_VINYLTOLUENE
  specific = 4
FEATURE [App::DocumentObjectGroupPython] Pu_element001  label="Pu_element : 1"  # scripted group (container) (typed FeaturePython)
  n = 1
  ref = Pu_element
FEATURE [App::DocumentObjectGroupPython] O_element076  label="O_element : 037"  # scripted group (container) (typed FeaturePython)
  n = 2
  ref = O_element
FEATURE [App::DocumentObjectGroupPython] G4_PLUTONIUM_DIOXIDE  # scripted group (container) (typed FeaturePython)
  Dunit = g/cm3
  Dvalue = 11.46
  Group = -> [Pu_element001,O_element076]
  conduct = 2
  density = 1
  expand = 3
  formula = G4_PLUTONIUM_DIOXIDE
  name = G4_PLUTONIUM_DIOXIDE
  specific = 4
FEATURE [App::DocumentObjectGroupPython] C_element078  label="C_element : 037"  # scripted group (container) (typed FeaturePython)
  n = 3
  ref = C_element
FEATURE [App::DocumentObjectGroupPython] H_element072  label="H_element : 034"  # scripted group (container) (typed FeaturePython)
  n = 3
  ref = H_element
FEATURE [App::DocumentObjectGroupPython] N_element036  label="N_element : 015"  # scripted group (container) (typed FeaturePython)
  n = 1
  ref = N_element
FEATURE [App::DocumentObjectGroupPython] G4_POLYACRYLONITRILE  # scripted group (container) (typed FeaturePython)
  Dunit = g/cm3
  Dvalue = 1.17
  Group = -> [C_element078,H_element072,N_element036]
  conduct = 2
  density = 1
  expand = 3
  formula = G4_POLYACRYLONITRILE
  name = G4_POLYACRYLONITRILE
  specific = 4
FEATURE [App::DocumentObjectGroupPython] C_element079  label="C_element : 16"  # scripted group (container) (typed FeaturePython)
  n = 16
  ref = C_element
FEATURE [App::DocumentObjectGroupPython] H_element073  label="H_element : 035"  # scripted group (container) (typed FeaturePython)
  n = 14
  ref = H_element
FEATURE [App::DocumentObjectGroupPython] O_element077  label="O_element : 038"  # scripted group (container) (typed FeaturePython)
  n = 3
  ref = O_element
FEATURE [App::DocumentObjectGroupPython] G4_POLYCARBONATE  # scripted group (container) (typed FeaturePython)
  Dunit = g/cm3
  Dvalue = 1.2
  Group = -> [C_element079,H_element073,O_element077]
  conduct = 2
  density = 1
  expand = 3
  formula = G4_POLYCARBONATE
  name = G4_POLYCARBONATE
  specific = 4
FEATURE [App::DocumentObjectGroupPython] C_element080  label="C_element : 038"  # scripted group (container) (typed FeaturePython)
  n = 8
  ref = C_element
FEATURE [App::DocumentObjectGroupPython] H_element074  label="H_element : 036"  # scripted group (container) (typed FeaturePython)
  n = 7
  ref = H_element
FEATURE [App::DocumentObjectGroupPython] Cl_element017  label="Cl_element : 007"  # scripted group (container) (typed FeaturePython)
  n = 1
  ref = Cl_element
FEATURE [App::DocumentObjectGroupPython] G4_POLYCHLOROSTYRENE  # scripted group (container) (typed FeaturePython)
  Dunit = g/cm3
  Dvalue = 1.3
  Group = -> [C_element080,H_element074,Cl_element017]
  conduct = 2
  density = 1
  expand = 3
  formula = G4_POLYCHLOROSTYRENE
  name = G4_POLYCHLOROSTYRENE
  specific = 4
FEATURE [App::DocumentObjectGroupPython] C_element081  label="C_element : 039"  # scripted group (container) (typed FeaturePython)
  n = 1
  ref = C_element
FEATURE [App::DocumentObjectGroupPython] H_element075  label="H_element : 037"  # scripted group (container) (typed FeaturePython)
  n = 2
  ref = H_element
FEATURE [App::DocumentObjectGroupPython] G4_POLYETHYLENE  # scripted group (container) (typed FeaturePython)
  Dunit = g/cm3
  Dvalue = 0.94
  Group = -> [C_element081,H_element075]
  conduct = 2
  density = 1
  expand = 3
  formula = G4_POLYETHYLENE
  name = G4_POLYETHYLENE
  specific = 4
FEATURE [App::DocumentObjectGroupPython] C_element082  label="C_element : 040"  # scripted group (container) (typed FeaturePython)
  n = 10
  ref = C_element
FEATURE [App::DocumentObjectGroupPython] H_element076  label="H_element : 038"  # scripted group (container) (typed FeaturePython)
  n = 8
  ref = H_element
FEATURE [App::DocumentObjectGroupPython] O_element078  label="O_element : 039"  # scripted group (container) (typed FeaturePython)
  n = 4
  ref = O_element
FEATURE [App::DocumentObjectGroupPython] G4_MYLAR  # scripted group (container) (typed FeaturePython)
  Dunit = g/cm3
  Dvalue = 1.4
  Group = -> [C_element082,H_element076,O_element078]
  conduct = 2
  density = 1
  expand = 3
  formula = G4_MYLAR
  name = G4_MYLAR
  specific = 4
FEATURE [App::DocumentObjectGroupPython] C_element083  label="C_element : 041"  # scripted group (container) (typed FeaturePython)
  n = 5
  ref = C_element
FEATURE [App::DocumentObjectGroupPython] H_element077  label="H_element : 039"  # scripted group (container) (typed FeaturePython)
  n = 8
  ref = H_element
FEATURE [App::DocumentObjectGroupPython] O_element079  label="O_element : 040"  # scripted group (container) (typed FeaturePython)
  n = 2
  ref = O_element
FEATURE [App::DocumentObjectGroupPython] G4_PLEXIGLASS  # scripted group (container) (typed FeaturePython)
  Dunit = g/cm3
  Dvalue = 1.19
  Group = -> [C_element083,H_element077,O_element079]
  conduct = 2
  density = 1
  expand = 3
  formula = G4_PLEXIGLASS
  name = G4_PLEXIGLASS
  specific = 4
FEATURE [App::DocumentObjectGroupPython] C_element084  label="C_element : 042"  # scripted group (container) (typed FeaturePython)
  n = 1
  ref = C_element
FEATURE [App::DocumentObjectGroupPython] H_element078  label="H_element : 040"  # scripted group (container) (typed FeaturePython)
  n = 2
  ref = H_element
FEATURE [App::DocumentObjectGroupPython] O_element080  label="O_element : 041"  # scripted group (container) (typed FeaturePython)
  n = 1
  ref = O_element
FEATURE [App::DocumentObjectGroupPython] G4_POLYOXYMETHYLENE  # scripted group (container) (typed FeaturePython)
  Dunit = g/cm3
  Dvalue = 1.425
  Group = -> [C_element084,H_element078,O_element080]
  conduct = 2
  density = 1
  expand = 3
  formula = G4_POLYOXYMETHYLENE
  name = G4_POLYOXYMETHYLENE
  specific = 4
FEATURE [App::DocumentObjectGroupPython] C_element085  label="C_element : 043"  # scripted group (container) (typed FeaturePython)
  n = 2
  ref = C_element
FEATURE [App::DocumentObjectGroupPython] H_element079  label="H_element : 041"  # scripted group (container) (typed FeaturePython)
  n = 4
  ref = H_element
FEATURE [App::DocumentObjectGroupPython] G4_POLYPROPYLENE  # scripted group (container) (typed FeaturePython)
  Dunit = g/cm3
  Dvalue = 0.9
  Group = -> [C_element085,H_element079]
  conduct = 2
  density = 1
  expand = 3
  formula = G4_POLYPROPYLENE
  name = G4_POLYPROPYLENE
  specific = 4
FEATURE [App::DocumentObjectGroupPython] C_element086  label="C_element : 044"  # scripted group (container) (typed FeaturePython)
  n = 8
  ref = C_element
FEATURE [App::DocumentObjectGroupPython] H_element080  label="H_element : 042"  # scripted group (container) (typed FeaturePython)
  n = 8
  ref = H_element
FEATURE [App::DocumentObjectGroupPython] G4_POLYSTYRENE  # scripted group (container) (typed FeaturePython)
  Dunit = g/cm3
  Dvalue = 1.06
  Group = -> [C_element086,H_element080]
  conduct = 2
  density = 1
  expand = 3
  formula = G4_POLYSTYRENE
  name = G4_POLYSTYRENE
  specific = 4
FEATURE [App::DocumentObjectGroupPython] C_element087  label="C_element : 045"  # scripted group (container) (typed FeaturePython)
  n = 2
  ref = C_element
FEATURE [App::DocumentObjectGroupPython] F_element014  label="F_element : 4"  # scripted group (container) (typed FeaturePython)
  n = 4
  ref = F_element
FEATURE [App::DocumentObjectGroupPython] G4_TEFLON  # scripted group (container) (typed FeaturePython)
  Dunit = g/cm3
  Dvalue = 2.2
  Group = -> [C_element087,F_element014]
  conduct = 2
  density = 1
  expand = 3
  formula = G4_TEFLON
  name = G4_TEFLON
  specific = 4
FEATURE [App::DocumentObjectGroupPython] C_element088  label="C_element : 046"  # scripted group (container) (typed FeaturePython)
  n = 2
  ref = C_element
FEATURE [App::DocumentObjectGroupPython] F_element015  label="F_element : 006"  # scripted group (container) (typed FeaturePython)
  n = 3
  ref = F_element
FEATURE [App::DocumentObjectGroupPython] Cl_element018  label="Cl_element : 008"  # scripted group (container) (typed FeaturePython)
  n = 1
  ref = Cl_element
FEATURE [App::DocumentObjectGroupPython] G4_POLYTRIFLUOROCHLOROETHYLENE  # scripted group (container) (typed FeaturePython)
  Dunit = g/cm3
  Dvalue = 2.1
  Group = -> [C_element088,F_element015,Cl_element018]
  conduct = 2
  density = 1
  expand = 3
  formula = G4_POLYTRIFLUOROCHLOROETHYLENE
  name = G4_POLYTRIFLUOROCHLOROETHYLENE
  specific = 4
FEATURE [App::DocumentObjectGroupPython] C_element089  label="C_element : 047"  # scripted group (container) (typed FeaturePython)
  n = 4
  ref = C_element
FEATURE [App::DocumentObjectGroupPython] H_element081  label="H_element : 043"  # scripted group (container) (typed FeaturePython)
  n = 6
  ref = H_element
FEATURE [App::DocumentObjectGroupPython] O_element081  label="O_element : 042"  # scripted group (container) (typed FeaturePython)
  n = 2
  ref = O_element
FEATURE [App::DocumentObjectGroupPython] G4_POLYVINYL_ACETATE  # scripted group (container) (typed FeaturePython)
  Dunit = g/cm3
  Dvalue = 1.19
  Group = -> [C_element089,H_element081,O_element081]
  conduct = 2
  density = 1
  expand = 3
  formula = G4_POLYVINYL_ACETATE
  name = G4_POLYVINYL_ACETATE
  specific = 4
FEATURE [App::DocumentObjectGroupPython] C_element090  label="C_element : 048"  # scripted group (container) (typed FeaturePython)
  n = 2
  ref = C_element
FEATURE [App::DocumentObjectGroupPython] H_element082  label="H_element : 044"  # scripted group (container) (typed FeaturePython)
  n = 4
  ref = H_element
FEATURE [App::DocumentObjectGroupPython] O_element082  label="O_element : 043"  # scripted group (container) (typed FeaturePython)
  n = 1
  ref = O_element
FEATURE [App::DocumentObjectGroupPython] G4_POLYVINYL_ALCOHOL  # scripted group (container) (typed FeaturePython)
  Dunit = g/cm3
  Dvalue = 1.3
  Group = -> [C_element090,H_element082,O_element082]
  conduct = 2
  density = 1
  expand = 3
  formula = G4_POLYVINYL_ALCOHOL
  name = G4_POLYVINYL_ALCOHOL
  specific = 4
FEATURE [App::DocumentObjectGroupPython] C_element091  label="C_element : 049"  # scripted group (container) (typed FeaturePython)
  n = 8
  ref = C_element
FEATURE [App::DocumentObjectGroupPython] H_element083  label="H_element : 045"  # scripted group (container) (typed FeaturePython)
  n = 14
  ref = H_element
FEATURE [App::DocumentObjectGroupPython] O_element083  label="O_element : 044"  # scripted group (container) (typed FeaturePython)
  n = 2
  ref = O_element
FEATURE [App::DocumentObjectGroupPython] G4_POLYVINYL_BUTYRAL  # scripted group (container) (typed FeaturePython)
  Dunit = g/cm3
  Dvalue = 1.12
  Group = -> [C_element091,H_element083,O_element083]
  conduct = 2
  density = 1
  expand = 3
  formula = G4_POLYVINYL_BUTYRAL
  name = G4_POLYVINYL_BUTYRAL
  specific = 4
FEATURE [App::DocumentObjectGroupPython] C_element092  label="C_element : 050"  # scripted group (container) (typed FeaturePython)
  n = 2
  ref = C_element
FEATURE [App::DocumentObjectGroupPython] H_element084  label="H_element : 046"  # scripted group (container) (typed FeaturePython)
  n = 3
  ref = H_element
FEATURE [App::DocumentObjectGroupPython] Cl_element019  label="Cl_element : 009"  # scripted group (container) (typed FeaturePython)
  n = 1
  ref = Cl_element
FEATURE [App::DocumentObjectGroupPython] G4_POLYVINYL_CHLORIDE  # scripted group (container) (typed FeaturePython)
  Dunit = g/cm3
  Dvalue = 1.3
  Group = -> [C_element092,H_element084,Cl_element019]
  conduct = 2
  density = 1
  expand = 3
  formula = G4_POLYVINYL_CHLORIDE
  name = G4_POLYVINYL_CHLORIDE
  specific = 4
FEATURE [App::DocumentObjectGroupPython] C_element093  label="C_element : 051"  # scripted group (container) (typed FeaturePython)
  n = 2
  ref = C_element
FEATURE [App::DocumentObjectGroupPython] H_element085  label="H_element : 047"  # scripted group (container) (typed FeaturePython)
  n = 2
  ref = H_element
FEATURE [App::DocumentObjectGroupPython] Cl_element020  label="Cl_element : 010"  # scripted group (container) (typed FeaturePython)
  n = 2
  ref = Cl_element
FEATURE [App::DocumentObjectGroupPython] G4_POLYVINYLIDENE_CHLORIDE  # scripted group (container) (typed FeaturePython)
  Dunit = g/cm3
  Dvalue = 1.7
  Group = -> [C_element093,H_element085,Cl_element020]
  conduct = 2
  density = 1
  expand = 3
  formula = G4_POLYVINYLIDENE_CHLORIDE
  name = G4_POLYVINYLIDENE_CHLORIDE
  specific = 4
FEATURE [App::DocumentObjectGroupPython] C_element094  label="C_element : 052"  # scripted group (container) (typed FeaturePython)
  n = 2
  ref = C_element
FEATURE [App::DocumentObjectGroupPython] H_element086  label="H_element : 048"  # scripted group (container) (typed FeaturePython)
  n = 2
  ref = H_element
FEATURE [App::DocumentObjectGroupPython] F_element016  label="F_element : 007"  # scripted group (container) (typed FeaturePython)
  n = 2
  ref = F_element
FEATURE [App::DocumentObjectGroupPython] G4_POLYVINYLIDENE_FLUORIDE  # scripted group (container) (typed FeaturePython)
  Dunit = g/cm3
  Dvalue = 1.76
  Group = -> [C_element094,H_element086,F_element016]
  conduct = 2
  density = 1
  expand = 3
  formula = G4_POLYVINYLIDENE_FLUORIDE
  name = G4_POLYVINYLIDENE_FLUORIDE
  specific = 4
FEATURE [App::DocumentObjectGroupPython] C_element095  label="C_element : 053"  # scripted group (container) (typed FeaturePython)
  n = 6
  ref = C_element
FEATURE [App::DocumentObjectGroupPython] H_element087  label="H_element : 9"  # scripted group (container) (typed FeaturePython)
  n = 9
  ref = H_element
FEATURE [App::DocumentObjectGroupPython] N_element037  label="N_element : 016"  # scripted group (container) (typed FeaturePython)
  n = 1
  ref = N_element
FEATURE [App::DocumentObjectGroupPython] O_element084  label="O_element : 045"  # scripted group (container) (typed FeaturePython)
  n = 1
  ref = O_element
FEATURE [App::DocumentObjectGroupPython] G4_POLYVINYL_PYRROLIDONE  # scripted group (container) (typed FeaturePython)
  Dunit = g/cm3
  Dvalue = 1.25
  Group = -> [C_element095,H_element087,N_element037,O_element084]
  conduct = 2
  density = 1
  expand = 3
  formula = G4_POLYVINYL_PYRROLIDONE
  name = G4_POLYVINYL_PYRROLIDONE
  specific = 4
FEATURE [App::DocumentObjectGroupPython] K_element008  label="K_element : 1"  # scripted group (container) (typed FeaturePython)
  n = 1
  ref = K_element
FEATURE [App::DocumentObjectGroupPython] I_element006  label="I_element : 003"  # scripted group (container) (typed FeaturePython)
  n = 1
  ref = I_element
FEATURE [App::DocumentObjectGroupPython] G4_POTASSIUM_IODIDE  # scripted group (container) (typed FeaturePython)
  Dunit = g/cm3
  Dvalue = 3.13
  Group = -> [K_element008,I_element006]
  conduct = 2
  density = 1
  expand = 3
  formula = G4_POTASSIUM_IODIDE
  name = G4_POTASSIUM_IODIDE
  specific = 4
FEATURE [App::DocumentObjectGroupPython] K_element009  label="K_element : 2"  # scripted group (container) (typed FeaturePython)
  n = 2
  ref = K_element
FEATURE [App::DocumentObjectGroupPython] O_element085  label="O_element : 046"  # scripted group (container) (typed FeaturePython)
  n = 1
  ref = O_element
FEATURE [App::DocumentObjectGroupPython] G4_POTASSIUM_OXIDE  # scripted group (container) (typed FeaturePython)
  Dunit = g/cm3
  Dvalue = 2.32
  Group = -> [K_element009,O_element085]
  conduct = 2
  density = 1
  expand = 3
  formula = G4_POTASSIUM_OXIDE
  name = G4_POTASSIUM_OXIDE
  specific = 4
FEATURE [App::DocumentObjectGroupPython] C_element096  label="C_element : 054"  # scripted group (container) (typed FeaturePython)
  n = 3
  ref = C_element
FEATURE [App::DocumentObjectGroupPython] H_element088  label="H_element : 049"  # scripted group (container) (typed FeaturePython)
  n = 8
  ref = H_element
FEATURE [App::DocumentObjectGroupPython] G4_PROPANE  # scripted group (container) (typed FeaturePython)
  Dunit = g/cm3
  Dvalue = 0.00187939
  Group = -> [C_element096,H_element088]
  conduct = 2
  density = 1
  expand = 3
  formula = G4_PROPANE
  name = G4_PROPANE
  specific = 4
FEATURE [App::DocumentObjectGroupPython] C_element097  label="C_element : 055"  # scripted group (container) (typed FeaturePython)
  n = 3
  ref = C_element
FEATURE [App::DocumentObjectGroupPython] H_element089  label="H_element : 050"  # scripted group (container) (typed FeaturePython)
  n = 8
  ref = H_element
FEATURE [App::DocumentObjectGroupPython] G4_lPROPANE  # scripted group (container) (typed FeaturePython)
  Dunit = g/cm3
  Dvalue = 0.43
  Group = -> [C_element097,H_element089]
  conduct = 2
  density = 1
  expand = 3
  formula = G4_lPROPANE
  name = G4_lPROPANE
  specific = 4
FEATURE [App::DocumentObjectGroupPython] C_element098  label="C_element : 056"  # scripted group (container) (typed FeaturePython)
  n = 3
  ref = C_element
FEATURE [App::DocumentObjectGroupPython] H_element090  label="H_element : 051"  # scripted group (container) (typed FeaturePython)
  n = 8
  ref = H_element
FEATURE [App::DocumentObjectGroupPython] O_element086  label="O_element : 047"  # scripted group (container) (typed FeaturePython)
  n = 1
  ref = O_element
FEATURE [App::DocumentObjectGroupPython] G4_N_PROPYL_ALCOHOL  label="G4_N-PROPYL_ALCOHOL"  # scripted group (container) (typed FeaturePython)
  Dunit = g/cm3
  Dvalue = 0.8035
  Group = -> [C_element098,H_element090,O_element086]
  conduct = 2
  density = 1
  expand = 3
  formula = G4_N-PROPYL_ALCOHOL
  name = G4_N-PROPYL_ALCOHOL
  specific = 4
FEATURE [App::DocumentObjectGroupPython] C_element099  label="C_element : 057"  # scripted group (container) (typed FeaturePython)
  n = 5
  ref = C_element
FEATURE [App::DocumentObjectGroupPython] H_element091  label="H_element : 052"  # scripted group (container) (typed FeaturePython)
  n = 5
  ref = H_element
FEATURE [App::DocumentObjectGroupPython] N_element038  label="N_element : 017"  # scripted group (container) (typed FeaturePython)
  n = 1
  ref = N_element
FEATURE [App::DocumentObjectGroupPython] G4_PYRIDINE  # scripted group (container) (typed FeaturePython)
  Dunit = g/cm3
  Dvalue = 0.9819
  Group = -> [C_element099,H_element091,N_element038]
  conduct = 2
  density = 1
  expand = 3
  formula = G4_PYRIDINE
  name = G4_PYRIDINE
  specific = 4
FEATURE [App::DocumentObjectGroupPython] H_element092  label="H_element : 0.144"  # scripted group (container) (typed FeaturePython)
  n = 0.143711
FEATURE [App::DocumentObjectGroupPython] C_element100  label="C_element : 0.856"  # scripted group (container) (typed FeaturePython)
  n = 0.856289
FEATURE [App::DocumentObjectGroupPython] G4_RUBBER_BUTYL  # scripted group (container) (typed FeaturePython)
  Dunit = g/cm3
  Dvalue = 0.92
  Group = -> [H_element092,C_element100]
  conduct = 2
  density = 1
  expand = 3
  formula = G4_RUBBER_BUTYL
  name = G4_RUBBER_BUTYL
  specific = 4
FEATURE [App::DocumentObjectGroupPython] H_element093  label="H_element : 0.118"  # scripted group (container) (typed FeaturePython)
  n = 0.118371
FEATURE [App::DocumentObjectGroupPython] C_element101  label="C_element : 0.882"  # scripted group (container) (typed FeaturePython)
  n = 0.881629
FEATURE [App::DocumentObjectGroupPython] G4_RUBBER_NATURAL  # scripted group (container) (typed FeaturePython)
  Dunit = g/cm3
  Dvalue = 0.92
  Group = -> [H_element093,C_element101]
  conduct = 2
  density = 1
  expand = 3
  formula = G4_RUBBER_NATURAL
  name = G4_RUBBER_NATURAL
  specific = 4
FEATURE [App::DocumentObjectGroupPython] H_element094  label="H_element : 0.145"  # scripted group (container) (typed FeaturePython)
  n = 0.05692
FEATURE [App::DocumentObjectGroupPython] C_element102  label="C_element : 0.543"  # scripted group (container) (typed FeaturePython)
  n = 0.542646
FEATURE [App::DocumentObjectGroupPython] Cl_element021  label="Cl_element : 0.400"  # scripted group (container) (typed FeaturePython)
  n = 0.400434
FEATURE [App::DocumentObjectGroupPython] G4_RUBBER_NEOPRENE  # scripted group (container) (typed FeaturePython)
  Dunit = g/cm3
  Dvalue = 1.23
  Group = -> [H_element094,C_element102,Cl_element021]
  conduct = 2
  density = 1
  expand = 3
  formula = G4_RUBBER_NEOPRENE
  name = G4_RUBBER_NEOPRENE
  specific = 4
FEATURE [App::DocumentObjectGroupPython] Si_element006  label="Si_element : 1"  # scripted group (container) (typed FeaturePython)
  n = 1
  ref = Si_element
FEATURE [App::DocumentObjectGroupPython] O_element087  label="O_element : 048"  # scripted group (container) (typed FeaturePython)
  n = 2
  ref = O_element
FEATURE [App::DocumentObjectGroupPython] G4_SILICON_DIOXIDE  # scripted group (container) (typed FeaturePython)
  Dunit = g/cm3
  Dvalue = 2.32
  Group = -> [Si_element006,O_element087]
  conduct = 2
  density = 1
  expand = 3
  formula = G4_SILICON_DIOXIDE
  name = G4_SILICON_DIOXIDE
  specific = 4
FEATURE [App::DocumentObjectGroupPython] Ag_element002  label="Ag_element : 1"  # scripted group (container) (typed FeaturePython)
  n = 1
  ref = Ag_element
FEATURE [App::DocumentObjectGroupPython] Br_element005  label="Br_element : 003"  # scripted group (container) (typed FeaturePython)
  n = 1
  ref = Br_element
FEATURE [App::DocumentObjectGroupPython] G4_SILVER_BROMIDE  # scripted group (container) (typed FeaturePython)
  Dunit = g/cm3
  Dvalue = 6.473
  Group = -> [Ag_element002,Br_element005]
  conduct = 2
  density = 1
  expand = 3
  formula = G4_SILVER_BROMIDE
  name = G4_SILVER_BROMIDE
  specific = 4
FEATURE [App::DocumentObjectGroupPython] Ag_element003  label="Ag_element : 002"  # scripted group (container) (typed FeaturePython)
  n = 1
  ref = Ag_element
FEATURE [App::DocumentObjectGroupPython] Cl_element022  label="Cl_element : 011"  # scripted group (container) (typed FeaturePython)
  n = 1
  ref = Cl_element
FEATURE [App::DocumentObjectGroupPython] G4_SILVER_CHLORIDE  # scripted group (container) (typed FeaturePython)
  Dunit = g/cm3
  Dvalue = 5.56
  Group = -> [Ag_element003,Cl_element022]
  conduct = 2
  density = 1
  expand = 3
  formula = G4_SILVER_CHLORIDE
  name = G4_SILVER_CHLORIDE
  specific = 4
FEATURE [App::DocumentObjectGroupPython] Br_element006  label="Br_element : 0.423"  # scripted group (container) (typed FeaturePython)
  n = 0.422895
FEATURE [App::DocumentObjectGroupPython] Ag_element004  label="Ag_element : 0.574"  # scripted group (container) (typed FeaturePython)
  n = 0.573748
FEATURE [App::DocumentObjectGroupPython] I_element007  label="I_element : 0.649"  # scripted group (container) (typed FeaturePython)
  n = 0.003357
FEATURE [App::DocumentObjectGroupPython] G4_SILVER_HALIDES  # scripted group (container) (typed FeaturePython)
  Dunit = g/cm3
  Dvalue = 6.47
  Group = -> [Br_element006,Ag_element004,I_element007]
  conduct = 2
  density = 1
  expand = 3
  formula = G4_SILVER_HALIDES
  name = G4_SILVER_HALIDES
  specific = 4
FEATURE [App::DocumentObjectGroupPython] Ag_element005  label="Ag_element : 003"  # scripted group (container) (typed FeaturePython)
  n = 1
  ref = Ag_element
FEATURE [App::DocumentObjectGroupPython] I_element008  label="I_element : 004"  # scripted group (container) (typed FeaturePython)
  n = 1
  ref = I_element
FEATURE [App::DocumentObjectGroupPython] G4_SILVER_IODIDE  # scripted group (container) (typed FeaturePython)
  Dunit = g/cm3
  Dvalue = 6.01
  Group = -> [Ag_element005,I_element008]
  conduct = 2
  density = 1
  expand = 3
  formula = G4_SILVER_IODIDE
  name = G4_SILVER_IODIDE
  specific = 4
FEATURE [App::DocumentObjectGroupPython] H_element095  label="H_element : 0.100"  # scripted group (container) (typed FeaturePython)
  n = 0.1
FEATURE [App::DocumentObjectGroupPython] C_element103  label="C_element : 0.204"  # scripted group (container) (typed FeaturePython)
  n = 0.204
FEATURE [App::DocumentObjectGroupPython] N_element039  label="N_element : 0.759"  # scripted group (container) (typed FeaturePython)
  n = 0.042
FEATURE [App::DocumentObjectGroupPython] O_element088  label="O_element : 0.645"  # scripted group (container) (typed FeaturePython)
  n = 0.645
FEATURE [App::DocumentObjectGroupPython] Na_element013  label="Na_element : 0.100"  # scripted group (container) (typed FeaturePython)
  n = 0.002
FEATURE [App::DocumentObjectGroupPython] P_element009  label="P_element : 0.107"  # scripted group (container) (typed FeaturePython)
  n = 0.001
FEATURE [App::DocumentObjectGroupPython] S_element020  label="S_element : 0.021"  # scripted group (container) (typed FeaturePython)
  n = 0.002
FEATURE [App::DocumentObjectGroupPython] Cl_element023  label="Cl_element : 0.590"  # scripted group (container) (typed FeaturePython)
  n = 0.003
FEATURE [App::DocumentObjectGroupPython] K_element010  label="K_element : 0.001"  # scripted group (container) (typed FeaturePython)
  n = 0.001
FEATURE [App::DocumentObjectGroupPython] G4_SKIN_ICRP  # scripted group (container) (typed FeaturePython)
  Dunit = g/cm3
  Dvalue = 1.09
  Group = -> [H_element095,C_element103,N_element039,O_element088,Na_element013,P_element009,S_element020,Cl_element023,K_element010]
  conduct = 2
  density = 1
  expand = 3
  formula = G4_SKIN_ICRP
  name = G4_SKIN_ICRP
  specific = 4
FEATURE [App::DocumentObjectGroupPython] Na_element014  label="Na_element : 2"  # scripted group (container) (typed FeaturePython)
  n = 2
  ref = Na_element
FEATURE [App::DocumentObjectGroupPython] C_element104  label="C_element : 058"  # scripted group (container) (typed FeaturePython)
  n = 1
  ref = C_element
FEATURE [App::DocumentObjectGroupPython] O_element089  label="O_element : 049"  # scripted group (container) (typed FeaturePython)
  n = 3
  ref = O_element
FEATURE [App::DocumentObjectGroupPython] G4_SODIUM_CARBONATE  # scripted group (container) (typed FeaturePython)
  Dunit = g/cm3
  Dvalue = 2.532
  Group = -> [Na_element014,C_element104,O_element089]
  conduct = 2
  density = 1
  expand = 3
  formula = G4_SODIUM_CARBONATE
  name = G4_SODIUM_CARBONATE
  specific = 4
FEATURE [App::DocumentObjectGroupPython] Na_element015  label="Na_element : 1"  # scripted group (container) (typed FeaturePython)
  n = 1
  ref = Na_element
FEATURE [App::DocumentObjectGroupPython] I_element009  label="I_element : 005"  # scripted group (container) (typed FeaturePython)
  n = 1
  ref = I_element
FEATURE [App::DocumentObjectGroupPython] G4_SODIUM_IODIDE  # scripted group (container) (typed FeaturePython)
  Dunit = g/cm3
  Dvalue = 3.667
  Group = -> [Na_element015,I_element009]
  conduct = 2
  density = 1
  expand = 3
  formula = G4_SODIUM_IODIDE
  name = G4_SODIUM_IODIDE
  specific = 4
FEATURE [App::DocumentObjectGroupPython] Na_element016  label="Na_element : 003"  # scripted group (container) (typed FeaturePython)
  n = 2
  ref = Na_element
FEATURE [App::DocumentObjectGroupPython] O_element090  label="O_element : 050"  # scripted group (container) (typed FeaturePython)
  n = 1
  ref = O_element
FEATURE [App::DocumentObjectGroupPython] G4_SODIUM_MONOXIDE  # scripted group (container) (typed FeaturePython)
  Dunit = g/cm3
  Dvalue = 2.27
  Group = -> [Na_element016,O_element090]
  conduct = 2
  density = 1
  expand = 3
  formula = G4_SODIUM_MONOXIDE
  name = G4_SODIUM_MONOXIDE
  specific = 4
FEATURE [App::DocumentObjectGroupPython] Na_element017  label="Na_element : 004"  # scripted group (container) (typed FeaturePython)
  n = 1
  ref = Na_element
FEATURE [App::DocumentObjectGroupPython] N_element040  label="N_element : 018"  # scripted group (container) (typed FeaturePython)
  n = 1
  ref = N_element
FEATURE [App::DocumentObjectGroupPython] O_element091  label="O_element : 051"  # scripted group (container) (typed FeaturePython)
  n = 3
  ref = O_element
FEATURE [App::DocumentObjectGroupPython] G4_SODIUM_NITRATE  # scripted group (container) (typed FeaturePython)
  Dunit = g/cm3
  Dvalue = 2.261
  Group = -> [Na_element017,N_element040,O_element091]
  conduct = 2
  density = 1
  expand = 3
  formula = G4_SODIUM_NITRATE
  name = G4_SODIUM_NITRATE
  specific = 4
FEATURE [App::DocumentObjectGroupPython] C_element105  label="C_element : 059"  # scripted group (container) (typed FeaturePython)
  n = 14
  ref = C_element
FEATURE [App::DocumentObjectGroupPython] H_element096  label="H_element : 053"  # scripted group (container) (typed FeaturePython)
  n = 12
  ref = H_element
FEATURE [App::DocumentObjectGroupPython] G4_STILBENE  # scripted group (container) (typed FeaturePython)
  Dunit = g/cm3
  Dvalue = 0.9707
  Group = -> [C_element105,H_element096]
  conduct = 2
  density = 1
  expand = 3
  formula = G4_STILBENE
  name = G4_STILBENE
  specific = 4
FEATURE [App::DocumentObjectGroupPython] C_element106  label="C_element : 12"  # scripted group (container) (typed FeaturePython)
  n = 12
  ref = C_element
FEATURE [App::DocumentObjectGroupPython] H_element097  label="H_element : 22"  # scripted group (container) (typed FeaturePython)
  n = 22
  ref = H_element
FEATURE [App::DocumentObjectGroupPython] O_element092  label="O_element : 11"  # scripted group (container) (typed FeaturePython)
  n = 11
  ref = O_element
FEATURE [App::DocumentObjectGroupPython] G4_SUCROSE  # scripted group (container) (typed FeaturePython)
  Dunit = g/cm3
  Dvalue = 1.5805
  Group = -> [C_element106,H_element097,O_element092]
  conduct = 2
  density = 1
  expand = 3
  formula = G4_SUCROSE
  name = G4_SUCROSE
  specific = 4
FEATURE [App::DocumentObjectGroupPython] C_element107  label="C_element : 18"  # scripted group (container) (typed FeaturePython)
  n = 18
  ref = C_element
FEATURE [App::DocumentObjectGroupPython] H_element098  label="H_element : 054"  # scripted group (container) (typed FeaturePython)
  n = 14
  ref = H_element
FEATURE [App::DocumentObjectGroupPython] G4_TERPHENYL  # scripted group (container) (typed FeaturePython)
  Dunit = g/cm3
  Dvalue = 1.24
  Group = -> [C_element107,H_element098]
  conduct = 2
  density = 1
  expand = 3
  formula = G4_TERPHENYL
  name = G4_TERPHENYL
  specific = 4
FEATURE [App::DocumentObjectGroupPython] H_element099  label="H_element : 0.146"  # scripted group (container) (typed FeaturePython)
  n = 0.106
FEATURE [App::DocumentObjectGroupPython] C_element108  label="C_element : 0.883"  # scripted group (container) (typed FeaturePython)
  n = 0.099
FEATURE [App::DocumentObjectGroupPython] N_element041  label="N_element : 0.020"  # scripted group (container) (typed FeaturePython)
  n = 0.02
FEATURE [App::DocumentObjectGroupPython] O_element093  label="O_element : 0.766"  # scripted group (container) (typed FeaturePython)
  n = 0.766
FEATURE [App::DocumentObjectGroupPython] Na_element018  label="Na_element : 0.101"  # scripted group (container) (typed FeaturePython)
  n = 0.002
FEATURE [App::DocumentObjectGroupPython] P_element010  label="P_element : 0.108"  # scripted group (container) (typed FeaturePython)
  n = 0.001
FEATURE [App::DocumentObjectGroupPython] S_element021  label="S_element : 0.022"  # scripted group (container) (typed FeaturePython)
  n = 0.002
FEATURE [App::DocumentObjectGroupPython] Cl_element024  label="Cl_element : 0.002"  # scripted group (container) (typed FeaturePython)
  n = 0.002
FEATURE [App::DocumentObjectGroupPython] K_element011  label="K_element : 0.017"  # scripted group (container) (typed FeaturePython)
  n = 0.002
FEATURE [App::DocumentObjectGroupPython] G4_TESTIS_ICRP  # scripted group (container) (typed FeaturePython)
  Dunit = g/cm3
  Dvalue = 1.04
  Group = -> [H_element099,C_element108,N_element041,O_element093,Na_element018,P_element010,S_element021,Cl_element024,K_element011]
  conduct = 2
  density = 1
  expand = 3
  formula = G4_TESTIS_ICRP
  name = G4_TESTIS_ICRP
  specific = 4
FEATURE [App::DocumentObjectGroupPython] C_element109  label="C_element : 060"  # scripted group (container) (typed FeaturePython)
  n = 2
  ref = C_element
FEATURE [App::DocumentObjectGroupPython] Cl_element025  label="Cl_element : 012"  # scripted group (container) (typed FeaturePython)
  n = 4
  ref = Cl_element
FEATURE [App::DocumentObjectGroupPython] G4_TETRACHLOROETHYLENE  # scripted group (container) (typed FeaturePython)
  Dunit = g/cm3
  Dvalue = 1.625
  Group = -> [C_element109,Cl_element025]
  conduct = 2
  density = 1
  expand = 3
  formula = G4_TETRACHLOROETHYLENE
  name = G4_TETRACHLOROETHYLENE
  specific = 4
FEATURE [App::DocumentObjectGroupPython] Tl_element001  label="Tl_element : 1"  # scripted group (container) (typed FeaturePython)
  n = 1
  ref = Tl_element
FEATURE [App::DocumentObjectGroupPython] Cl_element026  label="Cl_element : 013"  # scripted group (container) (typed FeaturePython)
  n = 1
  ref = Cl_element
FEATURE [App::DocumentObjectGroupPython] G4_THALLIUM_CHLORIDE  # scripted group (container) (typed FeaturePython)
  Dunit = g/cm3
  Dvalue = 7.004
  Group = -> [Tl_element001,Cl_element026]
  conduct = 2
  density = 1
  expand = 3
  formula = G4_THALLIUM_CHLORIDE
  name = G4_THALLIUM_CHLORIDE
  specific = 4
FEATURE [App::DocumentObjectGroupPython] H_element100  label="H_element : 0.147"  # scripted group (container) (typed FeaturePython)
  n = 0.105
FEATURE [App::DocumentObjectGroupPython] C_element110  label="C_element : 0.256"  # scripted group (container) (typed FeaturePython)
  n = 0.256
FEATURE [App::DocumentObjectGroupPython] N_element042  label="N_element : 0.760"  # scripted group (container) (typed FeaturePython)
  n = 0.027
FEATURE [App::DocumentObjectGroupPython] O_element094  label="O_element : 0.602"  # scripted group (container) (typed FeaturePython)
  n = 0.602
FEATURE [App::DocumentObjectGroupPython] Na_element019  label="Na_element : 0.102"  # scripted group (container) (typed FeaturePython)
  n = 0.001
FEATURE [App::DocumentObjectGroupPython] P_element011  label="P_element : 0.109"  # scripted group (container) (typed FeaturePython)
  n = 0.002
FEATURE [App::DocumentObjectGroupPython] S_element022  label="S_element : 0.023"  # scripted group (container) (typed FeaturePython)
  n = 0.003
FEATURE [App::DocumentObjectGroupPython] Cl_element027  label="Cl_element : 0.591"  # scripted group (container) (typed FeaturePython)
  n = 0.002
FEATURE [App::DocumentObjectGroupPython] K_element012  label="K_element : 0.018"  # scripted group (container) (typed FeaturePython)
  n = 0.002
FEATURE [App::DocumentObjectGroupPython] G4_TISSUE_SOFT_ICRP  # scripted group (container) (typed FeaturePython)
  Dunit = g/cm3
  Dvalue = 1.03
  Group = -> [H_element100,C_element110,N_element042,O_element094,Na_element019,P_element011,S_element022,Cl_element027,K_element012]
  conduct = 2
  density = 1
  expand = 3
  formula = G4_TISSUE_SOFT_ICRP
  name = G4_TISSUE_SOFT_ICRP
  specific = 4
FEATURE [App::DocumentObjectGroupPython] H_element101  label="H_element : 0.148"  # scripted group (container) (typed FeaturePython)
  n = 0.101
FEATURE [App::DocumentObjectGroupPython] C_element111  label="C_element : 0.111"  # scripted group (container) (typed FeaturePython)
  n = 0.111
FEATURE [App::DocumentObjectGroupPython] N_element043  label="N_element : 0.026"  # scripted group (container) (typed FeaturePython)
  n = 0.026
FEATURE [App::DocumentObjectGroupPython] O_element095  label="O_element : 0.762"  # scripted group (container) (typed FeaturePython)
  n = 0.762
FEATURE [App::DocumentObjectGroupPython] G4_TISSUE_SOFT_ICRU_4  label="G4_TISSUE_SOFT_ICRU-4"  # scripted group (container) (typed FeaturePython)
  Dunit = g/cm3
  Dvalue = 1
  Group = -> [H_element101,C_element111,N_element043,O_element095]
  conduct = 2
  density = 1
  expand = 3
  formula = G4_TISSUE_SOFT_ICRU-4
  name = G4_TISSUE_SOFT_ICRU-4
  specific = 4
FEATURE [App::DocumentObjectGroupPython] H_element102  label="H_element : 0.149"  # scripted group (container) (typed FeaturePython)
  n = 0.101869
FEATURE [App::DocumentObjectGroupPython] C_element112  label="C_element : 0.456"  # scripted group (container) (typed FeaturePython)
  n = 0.456179
FEATURE [App::DocumentObjectGroupPython] N_element044  label="N_element : 0.761"  # scripted group (container) (typed FeaturePython)
  n = 0.035172
FEATURE [App::DocumentObjectGroupPython] O_element096  label="O_element : 0.407"  # scripted group (container) (typed FeaturePython)
  n = 0.40678
FEATURE [App::DocumentObjectGroupPython] G4_TISSUE_METHANE  label="G4_TISSUE-METHANE"  # scripted group (container) (typed FeaturePython)
  Dunit = g/cm3
  Dvalue = 0.00106409
  Group = -> [H_element102,C_element112,N_element044,O_element096]
  conduct = 2
  density = 1
  expand = 3
  formula = G4_TISSUE-METHANE
  name = G4_TISSUE-METHANE
  specific = 4
FEATURE [App::DocumentObjectGroupPython] H_element103  label="H_element : 0.103"  # scripted group (container) (typed FeaturePython)
  n = 0.102672
FEATURE [App::DocumentObjectGroupPython] C_element113  label="C_element : 0.569"  # scripted group (container) (typed FeaturePython)
  n = 0.56894
FEATURE [App::DocumentObjectGroupPython] N_element045  label="N_element : 0.762"  # scripted group (container) (typed FeaturePython)
  n = 0.035022
FEATURE [App::DocumentObjectGroupPython] O_element097  label="O_element : 0.293"  # scripted group (container) (typed FeaturePython)
  n = 0.293366
FEATURE [App::DocumentObjectGroupPython] G4_TISSUE_PROPANE  label="G4_TISSUE-PROPANE"  # scripted group (container) (typed FeaturePython)
  Dunit = g/cm3
  Dvalue = 0.00182628
  Group = -> [H_element103,C_element113,N_element045,O_element097]
  conduct = 2
  density = 1
  expand = 3
  formula = G4_TISSUE-PROPANE
  name = G4_TISSUE-PROPANE
  specific = 4
FEATURE [App::DocumentObjectGroupPython] Ti_element003  label="Ti_element : 1"  # scripted group (container) (typed FeaturePython)
  n = 1
  ref = Ti_element
FEATURE [App::DocumentObjectGroupPython] O_element098  label="O_element : 052"  # scripted group (container) (typed FeaturePython)
  n = 2
  ref = O_element
FEATURE [App::DocumentObjectGroupPython] G4_TITANIUM_DIOXIDE  # scripted group (container) (typed FeaturePython)
  Dunit = g/cm3
  Dvalue = 4.26
  Group = -> [Ti_element003,O_element098]
  conduct = 2
  density = 1
  expand = 3
  formula = G4_TITANIUM_DIOXIDE
  name = G4_TITANIUM_DIOXIDE
  specific = 4
FEATURE [App::DocumentObjectGroupPython] C_element114  label="C_element : 061"  # scripted group (container) (typed FeaturePython)
  n = 7
  ref = C_element
FEATURE [App::DocumentObjectGroupPython] H_element104  label="H_element : 055"  # scripted group (container) (typed FeaturePython)
  n = 8
  ref = H_element
FEATURE [App::DocumentObjectGroupPython] G4_TOLUENE  # scripted group (container) (typed FeaturePython)
  Dunit = g/cm3
  Dvalue = 0.8669
  Group = -> [C_element114,H_element104]
  conduct = 2
  density = 1
  expand = 3
  formula = G4_TOLUENE
  name = G4_TOLUENE
  specific = 4
FEATURE [App::DocumentObjectGroupPython] C_element115  label="C_element : 062"  # scripted group (container) (typed FeaturePython)
  n = 2
  ref = C_element
FEATURE [App::DocumentObjectGroupPython] H_element105  label="H_element : 056"  # scripted group (container) (typed FeaturePython)
  n = 1
  ref = H_element
FEATURE [App::DocumentObjectGroupPython] Cl_element028  label="Cl_element : 014"  # scripted group (container) (typed FeaturePython)
  n = 3
  ref = Cl_element
FEATURE [App::DocumentObjectGroupPython] G4_TRICHLOROETHYLENE  # scripted group (container) (typed FeaturePython)
  Dunit = g/cm3
  Dvalue = 1.46
  Group = -> [C_element115,H_element105,Cl_element028]
  conduct = 2
  density = 1
  expand = 3
  formula = G4_TRICHLOROETHYLENE
  name = G4_TRICHLOROETHYLENE
  specific = 4
FEATURE [App::DocumentObjectGroupPython] C_element116  label="C_element : 063"  # scripted group (container) (typed FeaturePython)
  n = 6
  ref = C_element
FEATURE [App::DocumentObjectGroupPython] H_element106  label="H_element : 15"  # scripted group (container) (typed FeaturePython)
  n = 15
  ref = H_element
FEATURE [App::DocumentObjectGroupPython] O_element099  label="O_element : 053"  # scripted group (container) (typed FeaturePython)
  n = 4
  ref = O_element
FEATURE [App::DocumentObjectGroupPython] P_element012  label="P_element : 1"  # scripted group (container) (typed FeaturePython)
  n = 1
  ref = P_element
FEATURE [App::DocumentObjectGroupPython] G4_TRIETHYL_PHOSPHATE  # scripted group (container) (typed FeaturePython)
  Dunit = g/cm3
  Dvalue = 1.07
  Group = -> [C_element116,H_element106,O_element099,P_element012]
  conduct = 2
  density = 1
  expand = 3
  formula = G4_TRIETHYL_PHOSPHATE
  name = G4_TRIETHYL_PHOSPHATE
  specific = 4
FEATURE [App::DocumentObjectGroupPython] W_element003  label="W_element : 003"  # scripted group (container) (typed FeaturePython)
  n = 1
  ref = W_element
FEATURE [App::DocumentObjectGroupPython] F_element017  label="F_element : 6"  # scripted group (container) (typed FeaturePython)
  n = 6
  ref = F_element
FEATURE [App::DocumentObjectGroupPython] G4_TUNGSTEN_HEXAFLUORIDE  # scripted group (container) (typed FeaturePython)
  Dunit = g/cm3
  Dvalue = 2.4
  Group = -> [W_element003,F_element017]
  conduct = 2
  density = 1
  expand = 3
  formula = G4_TUNGSTEN_HEXAFLUORIDE
  name = G4_TUNGSTEN_HEXAFLUORIDE
  specific = 4
FEATURE [App::DocumentObjectGroupPython] U_element001  label="U_element : 1"  # scripted group (container) (typed FeaturePython)
  n = 1
  ref = U_element
FEATURE [App::DocumentObjectGroupPython] C_element117  label="C_element : 064"  # scripted group (container) (typed FeaturePython)
  n = 2
  ref = C_element
FEATURE [App::DocumentObjectGroupPython] G4_URANIUM_DICARBIDE  # scripted group (container) (typed FeaturePython)
  Dunit = g/cm3
  Dvalue = 11.28
  Group = -> [U_element001,C_element117]
  conduct = 2
  density = 1
  expand = 3
  formula = G4_URANIUM_DICARBIDE
  name = G4_URANIUM_DICARBIDE
  specific = 4
FEATURE [App::DocumentObjectGroupPython] U_element002  label="U_element : 002"  # scripted group (container) (typed FeaturePython)
  n = 1
  ref = U_element
FEATURE [App::DocumentObjectGroupPython] C_element118  label="C_element : 065"  # scripted group (container) (typed FeaturePython)
  n = 1
  ref = C_element
FEATURE [App::DocumentObjectGroupPython] G4_URANIUM_MONOCARBIDE  # scripted group (container) (typed FeaturePython)
  Dunit = g/cm3
  Dvalue = 13.63
  Group = -> [U_element002,C_element118]
  conduct = 2
  density = 1
  expand = 3
  formula = G4_URANIUM_MONOCARBIDE
  name = G4_URANIUM_MONOCARBIDE
  specific = 4
FEATURE [App::DocumentObjectGroupPython] U_element003  label="U_element : 003"  # scripted group (container) (typed FeaturePython)
  n = 1
  ref = U_element
FEATURE [App::DocumentObjectGroupPython] O_element100  label="O_element : 054"  # scripted group (container) (typed FeaturePython)
  n = 2
  ref = O_element
FEATURE [App::DocumentObjectGroupPython] G4_URANIUM_OXIDE  # scripted group (container) (typed FeaturePython)
  Dunit = g/cm3
  Dvalue = 10.96
  Group = -> [U_element003,O_element100]
  conduct = 2
  density = 1
  expand = 3
  formula = G4_URANIUM_OXIDE
  name = G4_URANIUM_OXIDE
  specific = 4
FEATURE [App::DocumentObjectGroupPython] C_element119  label="C_element : 066"  # scripted group (container) (typed FeaturePython)
  n = 1
  ref = C_element
FEATURE [App::DocumentObjectGroupPython] H_element107  label="H_element : 057"  # scripted group (container) (typed FeaturePython)
  n = 4
  ref = H_element
FEATURE [App::DocumentObjectGroupPython] N_element046  label="N_element : 019"  # scripted group (container) (typed FeaturePython)
  n = 2
  ref = N_element
FEATURE [App::DocumentObjectGroupPython] O_element101  label="O_element : 055"  # scripted group (container) (typed FeaturePython)
  n = 1
  ref = O_element
FEATURE [App::DocumentObjectGroupPython] G4_UREA  # scripted group (container) (typed FeaturePython)
  Dunit = g/cm3
  Dvalue = 1.323
  Group = -> [C_element119,H_element107,N_element046,O_element101]
  conduct = 2
  density = 1
  expand = 3
  formula = G4_UREA
  name = G4_UREA
  specific = 4
FEATURE [App::DocumentObjectGroupPython] C_element120  label="C_element : 067"  # scripted group (container) (typed FeaturePython)
  n = 5
  ref = C_element
FEATURE [App::DocumentObjectGroupPython] H_element108  label="H_element : 058"  # scripted group (container) (typed FeaturePython)
  n = 11
  ref = H_element
FEATURE [App::DocumentObjectGroupPython] N_element047  label="N_element : 020"  # scripted group (container) (typed FeaturePython)
  n = 1
  ref = N_element
FEATURE [App::DocumentObjectGroupPython] O_element102  label="O_element : 056"  # scripted group (container) (typed FeaturePython)
  n = 2
  ref = O_element
FEATURE [App::DocumentObjectGroupPython] G4_VALINE  # scripted group (container) (typed FeaturePython)
  Dunit = g/cm3
  Dvalue = 1.23
  Group = -> [C_element120,H_element108,N_element047,O_element102]
  conduct = 2
  density = 1
  expand = 3
  formula = G4_VALINE
  name = G4_VALINE
  specific = 4
FEATURE [App::DocumentObjectGroupPython] H_element109  label="H_element : 0.009"  # scripted group (container) (typed FeaturePython)
  n = 0.009417
FEATURE [App::DocumentObjectGroupPython] C_element121  label="C_element : 0.281"  # scripted group (container) (typed FeaturePython)
  n = 0.280555
FEATURE [App::DocumentObjectGroupPython] F_element018  label="F_element : 0.710"  # scripted group (container) (typed FeaturePython)
  n = 0.710028
FEATURE [App::DocumentObjectGroupPython] G4_VITON  # scripted group (container) (typed FeaturePython)
  Dunit = g/cm3
  Dvalue = 1.8
  Group = -> [H_element109,C_element121,F_element018]
  conduct = 2
  density = 1
  expand = 3
  formula = G4_VITON
  name = G4_VITON
  specific = 4
FEATURE [App::DocumentObjectGroupPython] H_element110  label="H_element : 059"  # scripted group (container) (typed FeaturePython)
  n = 2
  ref = H_element
FEATURE [App::DocumentObjectGroupPython] O_element103  label="O_element : 057"  # scripted group (container) (typed FeaturePython)
  n = 1
  ref = O_element
FEATURE [App::DocumentObjectGroupPython] G4_WATER  # scripted group (container) (typed FeaturePython)
  Dunit = g/cm3
  Dvalue = 1
  Group = -> [H_element110,O_element103]
  conduct = 2
  density = 1
  expand = 3
  formula = G4_WATER
  name = G4_WATER
  specific = 4
FEATURE [App::DocumentObjectGroupPython] H_element111  label="H_element : 060"  # scripted group (container) (typed FeaturePython)
  n = 2
  ref = H_element
FEATURE [App::DocumentObjectGroupPython] O_element104  label="O_element : 058"  # scripted group (container) (typed FeaturePython)
  n = 1
  ref = O_element
FEATURE [App::DocumentObjectGroupPython] G4_WATER_VAPOR  # scripted group (container) (typed FeaturePython)
  Dunit = g/cm3
  Dvalue = 0.000756182
  Group = -> [H_element111,O_element104]
  conduct = 2
  density = 1
  expand = 3
  formula = G4_WATER_VAPOR
  name = G4_WATER_VAPOR
  specific = 4
FEATURE [App::DocumentObjectGroupPython] C_element122  label="C_element : 068"  # scripted group (container) (typed FeaturePython)
  n = 8
  ref = C_element
FEATURE [App::DocumentObjectGroupPython] H_element112  label="H_element : 061"  # scripted group (container) (typed FeaturePython)
  n = 10
  ref = H_element
FEATURE [App::DocumentObjectGroupPython] G4_XYLENE  # scripted group (container) (typed FeaturePython)
  Dunit = g/cm3
  Dvalue = 0.87
  Group = -> [C_element122,H_element112]
  conduct = 2
  density = 1
  expand = 3
  formula = G4_XYLENE
  name = G4_XYLENE
  specific = 4
FEATURE [App::DocumentObjectGroupPython] C_element123  label="C_element : 069"  # scripted group (container) (typed FeaturePython)
  n = 1
  ref = C_element
FEATURE [App::DocumentObjectGroupPython] G4_GRAPHITE  # scripted group (container) (typed FeaturePython)
  Dunit = g/cm3
  Dvalue = 2.21
  Group = -> [C_element123]
  conduct = 2
  density = 1
  expand = 3
  formula = G4_GRAPHITE
  name = G4_GRAPHITE
  specific = 4
FEATURE [App::DocumentObjectGroupPython] NIST  # scripted group (container) (typed FeaturePython)
  Group = -> [G4_A_150_TISSUE,G4_ACETONE,G4_ACETYLENE,G4_ADENINE,G4_ADIPOSE_TISSUE_ICRP,G4_AIR,G4_ALANINE,G4_ALUMINUM_OXIDE,G4_AMBER,G4_AMMONIA,G4_ANILINE,G4_ANTHRACENE,G4_B_100_BONE,G4_BAKELITE,G4_BARIUM_FLUORIDE,G4_BARIUM_SULFATE,G4_BENZENE,G4_BERYLLIUM_OXIDE,G4_BGO,G4_BLOOD_ICRP,G4_BONE_COMPACT_ICRU,G4_BONE_CORTICAL_ICRP,G4_BORON_CARBIDE,G4_BORON_OXIDE,G4_BRAIN_ICRP,G4_BUTANE,G4_N_BUTYL_ALCOHOL,G4_C_552,+152 more]
FEATURE [App::DocumentObjectGroupPython] H_element113  label="H_element : 062"  # scripted group (container) (typed FeaturePython)
  n = 1
  ref = H_element
FEATURE [App::DocumentObjectGroupPython] G4_H  # scripted group (container) (typed FeaturePython)
  Dunit = g/cm3
  Dvalue = 8.3748e-05
  Group = -> [H_element113]
  conduct = 2
  density = 1
  expand = 3
  formula = H
  name = G4_H
  specific = 4
FEATURE [App::DocumentObjectGroupPython] He_element001  label="He_element : 1"  # scripted group (container) (typed FeaturePython)
  n = 1
  ref = He_element
FEATURE [App::DocumentObjectGroupPython] G4_He  # scripted group (container) (typed FeaturePython)
  Dunit = g/cm3
  Dvalue = 0.000166322
  Group = -> [He_element001]
  conduct = 2
  density = 1
  expand = 3
  formula = He
  name = G4_He
  specific = 4
FEATURE [App::DocumentObjectGroupPython] Li_element008  label="Li_element : 008"  # scripted group (container) (typed FeaturePython)
  n = 1
  ref = Li_element
FEATURE [App::DocumentObjectGroupPython] G4_Li  # scripted group (container) (typed FeaturePython)
  Dunit = g/cm3
  Dvalue = 0.534
  Group = -> [Li_element008]
  conduct = 2
  density = 1
  expand = 3
  formula = Li
  name = G4_Li
  specific = 4
FEATURE [App::DocumentObjectGroupPython] Be_element002  label="Be_element : 002"  # scripted group (container) (typed FeaturePython)
  n = 1
  ref = Be_element
FEATURE [App::DocumentObjectGroupPython] G4_Be  # scripted group (container) (typed FeaturePython)
  Dunit = g/cm3
  Dvalue = 1.848
  Group = -> [Be_element002]
  conduct = 2
  density = 1
  expand = 3
  formula = Be
  name = G4_Be
  specific = 4
FEATURE [App::DocumentObjectGroupPython] B_element007  label="B_element : 007"  # scripted group (container) (typed FeaturePython)
  n = 1
  ref = B_element
FEATURE [App::DocumentObjectGroupPython] G4_B  # scripted group (container) (typed FeaturePython)
  Dunit = g/cm3
  Dvalue = 2.37
  Group = -> [B_element007]
  conduct = 2
  density = 1
  expand = 3
  formula = B
  name = G4_B
  specific = 4
FEATURE [App::DocumentObjectGroupPython] C_element124  label="C_element : 070"  # scripted group (container) (typed FeaturePython)
  n = 1
  ref = C_element
FEATURE [App::DocumentObjectGroupPython] G4_C  # scripted group (container) (typed FeaturePython)
  Dunit = g/cm3
  Dvalue = 2
  Group = -> [C_element124]
  conduct = 2
  density = 1
  expand = 3
  formula = C
  name = G4_C
  specific = 4
FEATURE [App::DocumentObjectGroupPython] N_element048  label="N_element : 021"  # scripted group (container) (typed FeaturePython)
  n = 1
  ref = N_element
FEATURE [App::DocumentObjectGroupPython] G4_N  # scripted group (container) (typed FeaturePython)
  Dunit = g/cm3
  Dvalue = 0.0011652
  Group = -> [N_element048]
  conduct = 2
  density = 1
  expand = 3
  formula = N
  name = G4_N
  specific = 4
FEATURE [App::DocumentObjectGroupPython] O_element105  label="O_element : 059"  # scripted group (container) (typed FeaturePython)
  n = 1
  ref = O_element
FEATURE [App::DocumentObjectGroupPython] G4_O  # scripted group (container) (typed FeaturePython)
  Dunit = g/cm3
  Dvalue = 0.00133151
  Group = -> [O_element105]
  conduct = 2
  density = 1
  expand = 3
  formula = O
  name = G4_O
  specific = 4
FEATURE [App::DocumentObjectGroupPython] F_element019  label="F_element : 008"  # scripted group (container) (typed FeaturePython)
  n = 1
  ref = F_element
FEATURE [App::DocumentObjectGroupPython] G4_F  # scripted group (container) (typed FeaturePython)
  Dunit = g/cm3
  Dvalue = 0.00158029
  Group = -> [F_element019]
  conduct = 2
  density = 1
  expand = 3
  formula = F
  name = G4_F
  specific = 4
FEATURE [App::DocumentObjectGroupPython] Ne_element001  label="Ne_element : 1"  # scripted group (container) (typed FeaturePython)
  n = 1
  ref = Ne_element
FEATURE [App::DocumentObjectGroupPython] G4_Ne  # scripted group (container) (typed FeaturePython)
  Dunit = g/cm3
  Dvalue = 0.000838505
  Group = -> [Ne_element001]
  conduct = 2
  density = 1
  expand = 3
  formula = Ne
  name = G4_Ne
  specific = 4
FEATURE [App::DocumentObjectGroupPython] Na_element020  label="Na_element : 005"  # scripted group (container) (typed FeaturePython)
  n = 1
  ref = Na_element
FEATURE [App::DocumentObjectGroupPython] G4_Na  # scripted group (container) (typed FeaturePython)
  Dunit = g/cm3
  Dvalue = 0.971
  Group = -> [Na_element020]
  conduct = 2
  density = 1
  expand = 3
  formula = Na
  name = G4_Na
  specific = 4
FEATURE [App::DocumentObjectGroupPython] Mg_element011  label="Mg_element : 005"  # scripted group (container) (typed FeaturePython)
  n = 1
  ref = Mg_element
FEATURE [App::DocumentObjectGroupPython] G4_Mg  # scripted group (container) (typed FeaturePython)
  Dunit = g/cm3
  Dvalue = 1.74
  Group = -> [Mg_element011]
  conduct = 2
  density = 1
  expand = 3
  formula = Mg
  name = G4_Mg
  specific = 4
FEATURE [App::DocumentObjectGroupPython] Al_element004  label="Al_element : 1"  # scripted group (container) (typed FeaturePython)
  n = 1
  ref = Al_element
FEATURE [App::DocumentObjectGroupPython] G4_Al  # scripted group (container) (typed FeaturePython)
  Dunit = g/cm3
  Dvalue = 2.699
  Group = -> [Al_element004]
  conduct = 2
  density = 1
  expand = 3
  formula = Al
  name = G4_Al
  specific = 4
FEATURE [App::DocumentObjectGroupPython] Si_element007  label="Si_element : 002"  # scripted group (container) (typed FeaturePython)
  n = 1
  ref = Si_element
FEATURE [App::DocumentObjectGroupPython] G4_Si  # scripted group (container) (typed FeaturePython)
  Dunit = g/cm3
  Dvalue = 2.33
  Group = -> [Si_element007]
  conduct = 2
  density = 1
  expand = 3
  formula = Si
  name = G4_Si
  specific = 4
FEATURE [App::DocumentObjectGroupPython] P_element013  label="P_element : 002"  # scripted group (container) (typed FeaturePython)
  n = 1
  ref = P_element
FEATURE [App::DocumentObjectGroupPython] G4_P  # scripted group (container) (typed FeaturePython)
  Dunit = g/cm3
  Dvalue = 2.2
  Group = -> [P_element013]
  conduct = 2
  density = 1
  expand = 3
  formula = P
  name = G4_P
  specific = 4
FEATURE [App::DocumentObjectGroupPython] S_element023  label="S_element : 007"  # scripted group (container) (typed FeaturePython)
  n = 1
  ref = S_element
FEATURE [App::DocumentObjectGroupPython] G4_S  # scripted group (container) (typed FeaturePython)
  Dunit = g/cm3
  Dvalue = 2
  Group = -> [S_element023]
  conduct = 2
  density = 1
  expand = 3
  formula = S
  name = G4_S
  specific = 4
FEATURE [App::DocumentObjectGroupPython] Cl_element029  label="Cl_element : 015"  # scripted group (container) (typed FeaturePython)
  n = 1
  ref = Cl_element
FEATURE [App::DocumentObjectGroupPython] G4_Cl  # scripted group (container) (typed FeaturePython)
  Dunit = g/cm3
  Dvalue = 0.00299473
  Group = -> [Cl_element029]
  conduct = 2
  density = 1
  expand = 3
  formula = Cl
  name = G4_Cl
  specific = 4
FEATURE [App::DocumentObjectGroupPython] Ar_element002  label="Ar_element : 1"  # scripted group (container) (typed FeaturePython)
  n = 1
  ref = Ar_element
FEATURE [App::DocumentObjectGroupPython] G4_Ar  # scripted group (container) (typed FeaturePython)
  Dunit = g/cm3
  Dvalue = 0.00166201
  Group = -> [Ar_element002]
  conduct = 2
  density = 1
  expand = 3
  formula = Ar
  name = G4_Ar
  specific = 4
FEATURE [App::DocumentObjectGroupPython] K_element013  label="K_element : 003"  # scripted group (container) (typed FeaturePython)
  n = 1
  ref = K_element
FEATURE [App::DocumentObjectGroupPython] G4_K  # scripted group (container) (typed FeaturePython)
  Dunit = g/cm3
  Dvalue = 0.862
  Group = -> [K_element013]
  conduct = 2
  density = 1
  expand = 3
  formula = K
  name = G4_K
  specific = 4
FEATURE [App::DocumentObjectGroupPython] Ca_element014  label="Ca_element : 007"  # scripted group (container) (typed FeaturePython)
  n = 1
  ref = Ca_element
FEATURE [App::DocumentObjectGroupPython] G4_Ca  # scripted group (container) (typed FeaturePython)
  Dunit = g/cm3
  Dvalue = 1.55
  Group = -> [Ca_element014]
  conduct = 2
  density = 1
  expand = 3
  formula = Ca
  name = G4_Ca
  specific = 4
FEATURE [App::DocumentObjectGroupPython] Sc_element001  label="Sc_element : 1"  # scripted group (container) (typed FeaturePython)
  n = 1
  ref = Sc_element
FEATURE [App::DocumentObjectGroupPython] G4_Sc  # scripted group (container) (typed FeaturePython)
  Dunit = g/cm3
  Dvalue = 2.989
  Group = -> [Sc_element001]
  conduct = 2
  density = 1
  expand = 3
  formula = Sc
  name = G4_Sc
  specific = 4
FEATURE [App::DocumentObjectGroupPython] Ti_element004  label="Ti_element : 002"  # scripted group (container) (typed FeaturePython)
  n = 1
  ref = Ti_element
FEATURE [App::DocumentObjectGroupPython] G4_Ti  # scripted group (container) (typed FeaturePython)
  Dunit = g/cm3
  Dvalue = 4.54
  Group = -> [Ti_element004]
  conduct = 2
  density = 1
  expand = 3
  formula = Ti
  name = G4_Ti
  specific = 4
FEATURE [App::DocumentObjectGroupPython] V_element001  label="V_element : 1"  # scripted group (container) (typed FeaturePython)
  n = 1
  ref = V_element
FEATURE [App::DocumentObjectGroupPython] G4_V  # scripted group (container) (typed FeaturePython)
  Dunit = g/cm3
  Dvalue = 6.11
  Group = -> [V_element001]
  conduct = 2
  density = 1
  expand = 3
  formula = V
  name = G4_V
  specific = 4
FEATURE [App::DocumentObjectGroupPython] Cr_element001  label="Cr_element : 1"  # scripted group (container) (typed FeaturePython)
  n = 1
  ref = Cr_element
FEATURE [App::DocumentObjectGroupPython] G4_Cr  # scripted group (container) (typed FeaturePython)
  Dunit = g/cm3
  Dvalue = 7.18
  Group = -> [Cr_element001]
  conduct = 2
  density = 1
  expand = 3
  formula = Cr
  name = G4_Cr
  specific = 4
FEATURE [App::DocumentObjectGroupPython] Mn_element001  label="Mn_element : 1"  # scripted group (container) (typed FeaturePython)
  n = 1
  ref = Mn_element
FEATURE [App::DocumentObjectGroupPython] G4_Mn  # scripted group (container) (typed FeaturePython)
  Dunit = g/cm3
  Dvalue = 7.44
  Group = -> [Mn_element001]
  conduct = 2
  density = 1
  expand = 3
  formula = Mn
  name = G4_Mn
  specific = 4
FEATURE [App::DocumentObjectGroupPython] Fe_element007  label="Fe_element : 004"  # scripted group (container) (typed FeaturePython)
  n = 1
  ref = Fe_element
FEATURE [App::DocumentObjectGroupPython] G4_Fe  # scripted group (container) (typed FeaturePython)
  Dunit = g/cm3
  Dvalue = 7.874
  Group = -> [Fe_element007]
  conduct = 2
  density = 1
  expand = 3
  formula = Fe
  name = G4_Fe
  specific = 4
FEATURE [App::DocumentObjectGroupPython] Co_element001  label="Co_element : 1"  # scripted group (container) (typed FeaturePython)
  n = 1
  ref = Co_element
FEATURE [App::DocumentObjectGroupPython] G4_Co  # scripted group (container) (typed FeaturePython)
  Dunit = g/cm3
  Dvalue = 8.9
  Group = -> [Co_element001]
  conduct = 2
  density = 1
  expand = 3
  formula = Co
  name = G4_Co
  specific = 4
FEATURE [App::DocumentObjectGroupPython] Ni_element001  label="Ni_element : 1"  # scripted group (container) (typed FeaturePython)
  n = 1
  ref = Ni_element
FEATURE [App::DocumentObjectGroupPython] G4_Ni  # scripted group (container) (typed FeaturePython)
  Dunit = g/cm3
  Dvalue = 8.902
  Group = -> [Ni_element001]
  conduct = 2
  density = 1
  expand = 3
  formula = Ni
  name = G4_Ni
  specific = 4
FEATURE [App::DocumentObjectGroupPython] Cu_element001  label="Cu_element : 1"  # scripted group (container) (typed FeaturePython)
  n = 1
  ref = Cu_element
FEATURE [App::DocumentObjectGroupPython] G4_Cu  # scripted group (container) (typed FeaturePython)
  Dunit = g/cm3
  Dvalue = 8.96
  Group = -> [Cu_element001]
  conduct = 2
  density = 1
  expand = 3
  formula = Cu
  name = G4_Cu
  specific = 4
FEATURE [App::DocumentObjectGroupPython] Zn_element001  label="Zn_element : 1"  # scripted group (container) (typed FeaturePython)
  n = 1
  ref = Zn_element
FEATURE [App::DocumentObjectGroupPython] G4_Zn  # scripted group (container) (typed FeaturePython)
  Dunit = g/cm3
  Dvalue = 7.133
  Group = -> [Zn_element001]
  conduct = 2
  density = 1
  expand = 3
  formula = Zn
  name = G4_Zn
  specific = 4
FEATURE [App::DocumentObjectGroupPython] Ga_element002  label="Ga_element : 002"  # scripted group (container) (typed FeaturePython)
  n = 1
  ref = Ga_element
FEATURE [App::DocumentObjectGroupPython] G4_Ga  # scripted group (container) (typed FeaturePython)
  Dunit = g/cm3
  Dvalue = 5.904
  Group = -> [Ga_element002]
  conduct = 2
  density = 1
  expand = 3
  formula = Ga
  name = G4_Ga
  specific = 4
FEATURE [App::DocumentObjectGroupPython] Ge_element002  label="Ge_element : 1"  # scripted group (container) (typed FeaturePython)
  n = 1
  ref = Ge_element
FEATURE [App::DocumentObjectGroupPython] G4_Ge  # scripted group (container) (typed FeaturePython)
  Dunit = g/cm3
  Dvalue = 5.323
  Group = -> [Ge_element002]
  conduct = 2
  density = 1
  expand = 3
  formula = Ge
  name = G4_Ge
  specific = 4
FEATURE [App::DocumentObjectGroupPython] As_element003  label="As_element : 002"  # scripted group (container) (typed FeaturePython)
  n = 1
  ref = As_element
FEATURE [App::DocumentObjectGroupPython] G4_As  # scripted group (container) (typed FeaturePython)
  Dunit = g/cm3
  Dvalue = 5.73
  Group = -> [As_element003]
  conduct = 2
  density = 1
  expand = 3
  formula = As
  name = G4_As
  specific = 4
FEATURE [App::DocumentObjectGroupPython] Se_element001  label="Se_element : 1"  # scripted group (container) (typed FeaturePython)
  n = 1
  ref = Se_element
FEATURE [App::DocumentObjectGroupPython] G4_Se  # scripted group (container) (typed FeaturePython)
  Dunit = g/cm3
  Dvalue = 4.5
  Group = -> [Se_element001]
  conduct = 2
  density = 1
  expand = 3
  formula = Se
  name = G4_Se
  specific = 4
FEATURE [App::DocumentObjectGroupPython] Br_element007  label="Br_element : 004"  # scripted group (container) (typed FeaturePython)
  n = 1
  ref = Br_element
FEATURE [App::DocumentObjectGroupPython] G4_Br  # scripted group (container) (typed FeaturePython)
  Dunit = g/cm3
  Dvalue = 0.0070721
  Group = -> [Br_element007]
  conduct = 2
  density = 1
  expand = 3
  formula = Br
  name = G4_Br
  specific = 4
FEATURE [App::DocumentObjectGroupPython] Kr_element001  label="Kr_element : 1"  # scripted group (container) (typed FeaturePython)
  n = 1
  ref = Kr_element
FEATURE [App::DocumentObjectGroupPython] G4_Kr  # scripted group (container) (typed FeaturePython)
  Dunit = g/cm3
  Dvalue = 0.00347832
  Group = -> [Kr_element001]
  conduct = 2
  density = 1
  expand = 3
  formula = Kr
  name = G4_Kr
  specific = 4
FEATURE [App::DocumentObjectGroupPython] Rb_element001  label="Rb_element : 1"  # scripted group (container) (typed FeaturePython)
  n = 1
  ref = Rb_element
FEATURE [App::DocumentObjectGroupPython] G4_Rb  # scripted group (container) (typed FeaturePython)
  Dunit = g/cm3
  Dvalue = 1.532
  Group = -> [Rb_element001]
  conduct = 2
  density = 1
  expand = 3
  formula = Rb
  name = G4_Rb
  specific = 4
FEATURE [App::DocumentObjectGroupPython] Sr_element001  label="Sr_element : 1"  # scripted group (container) (typed FeaturePython)
  n = 1
  ref = Sr_element
FEATURE [App::DocumentObjectGroupPython] G4_Sr  # scripted group (container) (typed FeaturePython)
  Dunit = g/cm3
  Dvalue = 2.54
  Group = -> [Sr_element001]
  conduct = 2
  density = 1
  expand = 3
  formula = Sr
  name = G4_Sr
  specific = 4
FEATURE [App::DocumentObjectGroupPython] Y_element001  label="Y_element : 1"  # scripted group (container) (typed FeaturePython)
  n = 1
  ref = Y_element
FEATURE [App::DocumentObjectGroupPython] G4_Y  # scripted group (container) (typed FeaturePython)
  Dunit = g/cm3
  Dvalue = 4.469
  Group = -> [Y_element001]
  conduct = 2
  density = 1
  expand = 3
  formula = Y
  name = G4_Y
  specific = 4
FEATURE [App::DocumentObjectGroupPython] Zr_element001  label="Zr_element : 1"  # scripted group (container) (typed FeaturePython)
  n = 1
  ref = Zr_element
FEATURE [App::DocumentObjectGroupPython] G4_Zr  # scripted group (container) (typed FeaturePython)
  Dunit = g/cm3
  Dvalue = 6.506
  Group = -> [Zr_element001]
  conduct = 2
  density = 1
  expand = 3
  formula = Zr
  name = G4_Zr
  specific = 4
FEATURE [App::DocumentObjectGroupPython] Nb_element001  label="Nb_element : 1"  # scripted group (container) (typed FeaturePython)
  n = 1
  ref = Nb_element
FEATURE [App::DocumentObjectGroupPython] G4_Nb  # scripted group (container) (typed FeaturePython)
  Dunit = g/cm3
  Dvalue = 8.57
  Group = -> [Nb_element001]
  conduct = 2
  density = 1
  expand = 3
  formula = Nb
  name = G4_Nb
  specific = 4
FEATURE [App::DocumentObjectGroupPython] Mo_element001  label="Mo_element : 1"  # scripted group (container) (typed FeaturePython)
  n = 1
  ref = Mo_element
FEATURE [App::DocumentObjectGroupPython] G4_Mo  # scripted group (container) (typed FeaturePython)
  Dunit = g/cm3
  Dvalue = 10.22
  Group = -> [Mo_element001]
  conduct = 2
  density = 1
  expand = 3
  formula = Mo
  name = G4_Mo
  specific = 4
FEATURE [App::DocumentObjectGroupPython] Tc_element001  label="Tc_element : 1"  # scripted group (container) (typed FeaturePython)
  n = 1
  ref = Tc_element
FEATURE [App::DocumentObjectGroupPython] G4_Tc  # scripted group (container) (typed FeaturePython)
  Dunit = g/cm3
  Dvalue = 11.5
  Group = -> [Tc_element001]
  conduct = 2
  density = 1
  expand = 3
  formula = Tc
  name = G4_Tc
  specific = 4
FEATURE [App::DocumentObjectGroupPython] Ru_element001  label="Ru_element : 1"  # scripted group (container) (typed FeaturePython)
  n = 1
  ref = Ru_element
FEATURE [App::DocumentObjectGroupPython] G4_Ru  # scripted group (container) (typed FeaturePython)
  Dunit = g/cm3
  Dvalue = 12.41
  Group = -> [Ru_element001]
  conduct = 2
  density = 1
  expand = 3
  formula = Ru
  name = G4_Ru
  specific = 4
FEATURE [App::DocumentObjectGroupPython] Rh_element001  label="Rh_element : 1"  # scripted group (container) (typed FeaturePython)
  n = 1
  ref = Rh_element
FEATURE [App::DocumentObjectGroupPython] G4_Rh  # scripted group (container) (typed FeaturePython)
  Dunit = g/cm3
  Dvalue = 12.41
  Group = -> [Rh_element001]
  conduct = 2
  density = 1
  expand = 3
  formula = Rh
  name = G4_Rh
  specific = 4
FEATURE [App::DocumentObjectGroupPython] Pd_element001  label="Pd_element : 1"  # scripted group (container) (typed FeaturePython)
  n = 1
  ref = Pd_element
FEATURE [App::DocumentObjectGroupPython] G4_Pd  # scripted group (container) (typed FeaturePython)
  Dunit = g/cm3
  Dvalue = 12.02
  Group = -> [Pd_element001]
  conduct = 2
  density = 1
  expand = 3
  formula = Pd
  name = G4_Pd
  specific = 4
FEATURE [App::DocumentObjectGroupPython] Ag_element006  label="Ag_element : 004"  # scripted group (container) (typed FeaturePython)
  n = 1
  ref = Ag_element
FEATURE [App::DocumentObjectGroupPython] G4_Ag  # scripted group (container) (typed FeaturePython)
  Dunit = g/cm3
  Dvalue = 10.5
  Group = -> [Ag_element006]
  conduct = 2
  density = 1
  expand = 3
  formula = Ag
  name = G4_Ag
  specific = 4
FEATURE [App::DocumentObjectGroupPython] Cd_element003  label="Cd_element : 003"  # scripted group (container) (typed FeaturePython)
  n = 1
  ref = Cd_element
FEATURE [App::DocumentObjectGroupPython] G4_Cd  # scripted group (container) (typed FeaturePython)
  Dunit = g/cm3
  Dvalue = 8.65
  Group = -> [Cd_element003]
  conduct = 2
  density = 1
  expand = 3
  formula = Cd
  name = G4_Cd
  specific = 4
FEATURE [App::DocumentObjectGroupPython] In_element001  label="In_element : 1"  # scripted group (container) (typed FeaturePython)
  n = 1
  ref = In_element
FEATURE [App::DocumentObjectGroupPython] G4_In  # scripted group (container) (typed FeaturePython)
  Dunit = g/cm3
  Dvalue = 7.31
  Group = -> [In_element001]
  conduct = 2
  density = 1
  expand = 3
  formula = In
  name = G4_In
  specific = 4
FEATURE [App::DocumentObjectGroupPython] Sn_element001  label="Sn_element : 1"  # scripted group (container) (typed FeaturePython)
  n = 1
  ref = Sn_element
FEATURE [App::DocumentObjectGroupPython] G4_Sn  # scripted group (container) (typed FeaturePython)
  Dunit = g/cm3
  Dvalue = 7.31
  Group = -> [Sn_element001]
  conduct = 2
  density = 1
  expand = 3
  formula = Sn
  name = G4_Sn
  specific = 4
FEATURE [App::DocumentObjectGroupPython] Sb_element001  label="Sb_element : 1"  # scripted group (container) (typed FeaturePython)
  n = 1
  ref = Sb_element
FEATURE [App::DocumentObjectGroupPython] G4_Sb  # scripted group (container) (typed FeaturePython)
  Dunit = g/cm3
  Dvalue = 6.691
  Group = -> [Sb_element001]
  conduct = 2
  density = 1
  expand = 3
  formula = Sb
  name = G4_Sb
  specific = 4
FEATURE [App::DocumentObjectGroupPython] Te_element002  label="Te_element : 002"  # scripted group (container) (typed FeaturePython)
  n = 1
  ref = Te_element
FEATURE [App::DocumentObjectGroupPython] G4_Te  # scripted group (container) (typed FeaturePython)
  Dunit = g/cm3
  Dvalue = 6.24
  Group = -> [Te_element002]
  conduct = 2
  density = 1
  expand = 3
  formula = Te
  name = G4_Te
  specific = 4
FEATURE [App::DocumentObjectGroupPython] I_element010  label="I_element : 006"  # scripted group (container) (typed FeaturePython)
  n = 1
  ref = I_element
FEATURE [App::DocumentObjectGroupPython] G4_I  # scripted group (container) (typed FeaturePython)
  Dunit = g/cm3
  Dvalue = 4.93
  Group = -> [I_element010]
  conduct = 2
  density = 1
  expand = 3
  formula = I
  name = G4_I
  specific = 4
FEATURE [App::DocumentObjectGroupPython] Xe_element001  label="Xe_element : 1"  # scripted group (container) (typed FeaturePython)
  n = 1
  ref = Xe_element
FEATURE [App::DocumentObjectGroupPython] G4_Xe  # scripted group (container) (typed FeaturePython)
  Dunit = g/cm3
  Dvalue = 0.00548536
  Group = -> [Xe_element001]
  conduct = 2
  density = 1
  expand = 3
  formula = Xe
  name = G4_Xe
  specific = 4
FEATURE [App::DocumentObjectGroupPython] Cs_element003  label="Cs_element : 003"  # scripted group (container) (typed FeaturePython)
  n = 1
  ref = Cs_element
FEATURE [App::DocumentObjectGroupPython] G4_Cs  # scripted group (container) (typed FeaturePython)
  Dunit = g/cm3
  Dvalue = 1.873
  Group = -> [Cs_element003]
  conduct = 2
  density = 1
  expand = 3
  formula = Cs
  name = G4_Cs
  specific = 4
FEATURE [App::DocumentObjectGroupPython] Ba_element003  label="Ba_element : 003"  # scripted group (container) (typed FeaturePython)
  n = 1
  ref = Ba_element
FEATURE [App::DocumentObjectGroupPython] G4_Ba  # scripted group (container) (typed FeaturePython)
  Dunit = g/cm3
  Dvalue = 3.5
  Group = -> [Ba_element003]
  conduct = 2
  density = 1
  expand = 3
  formula = Ba
  name = G4_Ba
  specific = 4
FEATURE [App::DocumentObjectGroupPython] La_element003  label="La_element : 003"  # scripted group (container) (typed FeaturePython)
  n = 1
  ref = La_element
FEATURE [App::DocumentObjectGroupPython] G4_La  # scripted group (container) (typed FeaturePython)
  Dunit = g/cm3
  Dvalue = 6.154
  Group = -> [La_element003]
  conduct = 2
  density = 1
  expand = 3
  formula = La
  name = G4_La
  specific = 4
FEATURE [App::DocumentObjectGroupPython] Ce_element002  label="Ce_element : 1"  # scripted group (container) (typed FeaturePython)
  n = 1
  ref = Ce_element
FEATURE [App::DocumentObjectGroupPython] G4_Ce  # scripted group (container) (typed FeaturePython)
  Dunit = g/cm3
  Dvalue = 6.657
  Group = -> [Ce_element002]
  conduct = 2
  density = 1
  expand = 3
  formula = Ce
  name = G4_Ce
  specific = 4
FEATURE [App::DocumentObjectGroupPython] Pr_element001  label="Pr_element : 1"  # scripted group (container) (typed FeaturePython)
  n = 1
  ref = Pr_element
FEATURE [App::DocumentObjectGroupPython] G4_Pr  # scripted group (container) (typed FeaturePython)
  Dunit = g/cm3
  Dvalue = 6.71
  Group = -> [Pr_element001]
  conduct = 2
  density = 1
  expand = 3
  formula = Pr
  name = G4_Pr
  specific = 4
FEATURE [App::DocumentObjectGroupPython] Nd_element001  label="Nd_element : 1"  # scripted group (container) (typed FeaturePython)
  n = 1
  ref = Nd_element
FEATURE [App::DocumentObjectGroupPython] G4_Nd  # scripted group (container) (typed FeaturePython)
  Dunit = g/cm3
  Dvalue = 6.9
  Group = -> [Nd_element001]
  conduct = 2
  density = 1
  expand = 3
  formula = Nd
  name = G4_Nd
  specific = 4
FEATURE [App::DocumentObjectGroupPython] Pm_element001  label="Pm_element : 1"  # scripted group (container) (typed FeaturePython)
  n = 1
  ref = Pm_element
FEATURE [App::DocumentObjectGroupPython] G4_Pm  # scripted group (container) (typed FeaturePython)
  Dunit = g/cm3
  Dvalue = 7.22
  Group = -> [Pm_element001]
  conduct = 2
  density = 1
  expand = 3
  formula = Pm
  name = G4_Pm
  specific = 4
FEATURE [App::DocumentObjectGroupPython] Sm_element001  label="Sm_element : 1"  # scripted group (container) (typed FeaturePython)
  n = 1
  ref = Sm_element
FEATURE [App::DocumentObjectGroupPython] G4_Sm  # scripted group (container) (typed FeaturePython)
  Dunit = g/cm3
  Dvalue = 7.46
  Group = -> [Sm_element001]
  conduct = 2
  density = 1
  expand = 3
  formula = Sm
  name = G4_Sm
  specific = 4
FEATURE [App::DocumentObjectGroupPython] Eu_element001  label="Eu_element : 1"  # scripted group (container) (typed FeaturePython)
  n = 1
  ref = Eu_element
FEATURE [App::DocumentObjectGroupPython] G4_Eu  # scripted group (container) (typed FeaturePython)
  Dunit = g/cm3
  Dvalue = 5.243
  Group = -> [Eu_element001]
  conduct = 2
  density = 1
  expand = 3
  formula = Eu
  name = G4_Eu
  specific = 4
FEATURE [App::DocumentObjectGroupPython] Gd_element002  label="Gd_element : 1"  # scripted group (container) (typed FeaturePython)
  n = 1
  ref = Gd_element
FEATURE [App::DocumentObjectGroupPython] G4_Gd  # scripted group (container) (typed FeaturePython)
  Dunit = g/cm3
  Dvalue = 7.9004
  Group = -> [Gd_element002]
  conduct = 2
  density = 1
  expand = 3
  formula = Gd
  name = G4_Gd
  specific = 4
FEATURE [App::DocumentObjectGroupPython] Tb_element001  label="Tb_element : 1"  # scripted group (container) (typed FeaturePython)
  n = 1
  ref = Tb_element
FEATURE [App::DocumentObjectGroupPython] G4_Tb  # scripted group (container) (typed FeaturePython)
  Dunit = g/cm3
  Dvalue = 8.229
  Group = -> [Tb_element001]
  conduct = 2
  density = 1
  expand = 3
  formula = Tb
  name = G4_Tb
  specific = 4
FEATURE [App::DocumentObjectGroupPython] Dy_element001  label="Dy_element : 1"  # scripted group (container) (typed FeaturePython)
  n = 1
  ref = Dy_element
FEATURE [App::DocumentObjectGroupPython] G4_Dy  # scripted group (container) (typed FeaturePython)
  Dunit = g/cm3
  Dvalue = 8.55
  Group = -> [Dy_element001]
  conduct = 2
  density = 1
  expand = 3
  formula = Dy
  name = G4_Dy
  specific = 4
FEATURE [App::DocumentObjectGroupPython] Ho_element001  label="Ho_element : 1"  # scripted group (container) (typed FeaturePython)
  n = 1
  ref = Ho_element
FEATURE [App::DocumentObjectGroupPython] G4_Ho  # scripted group (container) (typed FeaturePython)
  Dunit = g/cm3
  Dvalue = 8.795
  Group = -> [Ho_element001]
  conduct = 2
  density = 1
  expand = 3
  formula = Ho
  name = G4_Ho
  specific = 4
FEATURE [App::DocumentObjectGroupPython] Er_element001  label="Er_element : 1"  # scripted group (container) (typed FeaturePython)
  n = 1
  ref = Er_element
FEATURE [App::DocumentObjectGroupPython] G4_Er  # scripted group (container) (typed FeaturePython)
  Dunit = g/cm3
  Dvalue = 9.066
  Group = -> [Er_element001]
  conduct = 2
  density = 1
  expand = 3
  formula = Er
  name = G4_Er
  specific = 4
FEATURE [App::DocumentObjectGroupPython] Tm_element001  label="Tm_element : 1"  # scripted group (container) (typed FeaturePython)
  n = 1
  ref = Tm_element
FEATURE [App::DocumentObjectGroupPython] G4_Tm  # scripted group (container) (typed FeaturePython)
  Dunit = g/cm3
  Dvalue = 9.321
  Group = -> [Tm_element001]
  conduct = 2
  density = 1
  expand = 3
  formula = Tm
  name = G4_Tm
  specific = 4
FEATURE [App::DocumentObjectGroupPython] Yb_element001  label="Yb_element : 1"  # scripted group (container) (typed FeaturePython)
  n = 1
  ref = Yb_element
FEATURE [App::DocumentObjectGroupPython] G4_Yb  # scripted group (container) (typed FeaturePython)
  Dunit = g/cm3
  Dvalue = 6.73
  Group = -> [Yb_element001]
  conduct = 2
  density = 1
  expand = 3
  formula = Yb
  name = G4_Yb
  specific = 4
FEATURE [App::DocumentObjectGroupPython] Lu_element001  label="Lu_element : 1"  # scripted group (container) (typed FeaturePython)
  n = 1
  ref = Lu_element
FEATURE [App::DocumentObjectGroupPython] G4_Lu  # scripted group (container) (typed FeaturePython)
  Dunit = g/cm3
  Dvalue = 9.84
  Group = -> [Lu_element001]
  conduct = 2
  density = 1
  expand = 3
  formula = Lu
  name = G4_Lu
  specific = 4
FEATURE [App::DocumentObjectGroupPython] Hf_element001  label="Hf_element : 1"  # scripted group (container) (typed FeaturePython)
  n = 1
  ref = Hf_element
FEATURE [App::DocumentObjectGroupPython] G4_Hf  # scripted group (container) (typed FeaturePython)
  Dunit = g/cm3
  Dvalue = 13.31
  Group = -> [Hf_element001]
  conduct = 2
  density = 1
  expand = 3
  formula = Hf
  name = G4_Hf
  specific = 4
FEATURE [App::DocumentObjectGroupPython] Ta_element001  label="Ta_element : 1"  # scripted group (container) (typed FeaturePython)
  n = 1
  ref = Ta_element
FEATURE [App::DocumentObjectGroupPython] G4_Ta  # scripted group (container) (typed FeaturePython)
  Dunit = g/cm3
  Dvalue = 16.654
  Group = -> [Ta_element001]
  conduct = 2
  density = 1
  expand = 3
  formula = Ta
  name = G4_Ta
  specific = 4
FEATURE [App::DocumentObjectGroupPython] W_element004  label="W_element : 004"  # scripted group (container) (typed FeaturePython)
  n = 1
  ref = W_element
FEATURE [App::DocumentObjectGroupPython] G4_W  # scripted group (container) (typed FeaturePython)
  Dunit = g/cm3
  Dvalue = 19.3
  Group = -> [W_element004]
  conduct = 2
  density = 1
  expand = 3
  formula = W
  name = G4_W
  specific = 4
FEATURE [App::DocumentObjectGroupPython] Re_element001  label="Re_element : 1"  # scripted group (container) (typed FeaturePython)
  n = 1
  ref = Re_element
FEATURE [App::DocumentObjectGroupPython] G4_Re  # scripted group (container) (typed FeaturePython)
  Dunit = g/cm3
  Dvalue = 21.02
  Group = -> [Re_element001]
  conduct = 2
  density = 1
  expand = 3
  formula = Re
  name = G4_Re
  specific = 4
FEATURE [App::DocumentObjectGroupPython] Os_element001  label="Os_element : 1"  # scripted group (container) (typed FeaturePython)
  n = 1
  ref = Os_element
FEATURE [App::DocumentObjectGroupPython] G4_Os  # scripted group (container) (typed FeaturePython)
  Dunit = g/cm3
  Dvalue = 22.57
  Group = -> [Os_element001]
  conduct = 2
  density = 1
  expand = 3
  formula = Os
  name = G4_Os
  specific = 4
FEATURE [App::DocumentObjectGroupPython] Ir_element001  label="Ir_element : 1"  # scripted group (container) (typed FeaturePython)
  n = 1
  ref = Ir_element
FEATURE [App::DocumentObjectGroupPython] G4_Ir  # scripted group (container) (typed FeaturePython)
  Dunit = g/cm3
  Dvalue = 22.42
  Group = -> [Ir_element001]
  conduct = 2
  density = 1
  expand = 3
  formula = Ir
  name = G4_Ir
  specific = 4
FEATURE [App::DocumentObjectGroupPython] Pt_element001  label="Pt_element : 1"  # scripted group (container) (typed FeaturePython)
  n = 1
  ref = Pt_element
FEATURE [App::DocumentObjectGroupPython] G4_Pt  # scripted group (container) (typed FeaturePython)
  Dunit = g/cm3
  Dvalue = 21.45
  Group = -> [Pt_element001]
  conduct = 2
  density = 1
  expand = 3
  formula = Pt
  name = G4_Pt
  specific = 4
FEATURE [App::DocumentObjectGroupPython] Au_element001  label="Au_element : 1"  # scripted group (container) (typed FeaturePython)
  n = 1
  ref = Au_element
FEATURE [App::DocumentObjectGroupPython] G4_Au  # scripted group (container) (typed FeaturePython)
  Dunit = g/cm3
  Dvalue = 19.32
  Group = -> [Au_element001]
  conduct = 2
  density = 1
  expand = 3
  formula = Au
  name = G4_Au
  specific = 4
FEATURE [App::DocumentObjectGroupPython] Hg_element002  label="Hg_element : 002"  # scripted group (container) (typed FeaturePython)
  n = 1
  ref = Hg_element
FEATURE [App::DocumentObjectGroupPython] G4_Hg  # scripted group (container) (typed FeaturePython)
  Dunit = g/cm3
  Dvalue = 13.546
  Group = -> [Hg_element002]
  conduct = 2
  density = 1
  expand = 3
  formula = Hg
  name = G4_Hg
  specific = 4
FEATURE [App::DocumentObjectGroupPython] Tl_element002  label="Tl_element : 002"  # scripted group (container) (typed FeaturePython)
  n = 1
  ref = Tl_element
FEATURE [App::DocumentObjectGroupPython] G4_Tl  # scripted group (container) (typed FeaturePython)
  Dunit = g/cm3
  Dvalue = 11.72
  Group = -> [Tl_element002]
  conduct = 2
  density = 1
  expand = 3
  formula = Tl
  name = G4_Tl
  specific = 4
FEATURE [App::DocumentObjectGroupPython] Pb_element003  label="Pb_element : 1"  # scripted group (container) (typed FeaturePython)
  n = 1
  ref = Pb_element
FEATURE [App::DocumentObjectGroupPython] G4_Pb  # scripted group (container) (typed FeaturePython)
  Dunit = g/cm3
  Dvalue = 11.35
  Group = -> [Pb_element003]
  conduct = 2
  density = 1
  expand = 3
  formula = Pb
  name = G4_Pb
  specific = 4
FEATURE [App::DocumentObjectGroupPython] Bi_element002  label="Bi_element : 1"  # scripted group (container) (typed FeaturePython)
  n = 1
  ref = Bi_element
FEATURE [App::DocumentObjectGroupPython] G4_Bi  # scripted group (container) (typed FeaturePython)
  Dunit = g/cm3
  Dvalue = 9.747
  Group = -> [Bi_element002]
  conduct = 2
  density = 1
  expand = 3
  formula = Bi
  name = G4_Bi
  specific = 4
FEATURE [App::DocumentObjectGroupPython] Po_element001  label="Po_element : 1"  # scripted group (container) (typed FeaturePython)
  n = 1
  ref = Po_element
FEATURE [App::DocumentObjectGroupPython] G4_Po  # scripted group (container) (typed FeaturePython)
  Dunit = g/cm3
  Dvalue = 9.32
  Group = -> [Po_element001]
  conduct = 2
  density = 1
  expand = 3
  formula = Po
  name = G4_Po
  specific = 4
FEATURE [App::DocumentObjectGroupPython] At_element001  label="At_element : 1"  # scripted group (container) (typed FeaturePython)
  n = 1
  ref = At_element
FEATURE [App::DocumentObjectGroupPython] G4_At  # scripted group (container) (typed FeaturePython)
  Dunit = g/cm3
  Dvalue = 9.32
  Group = -> [At_element001]
  conduct = 2
  density = 1
  expand = 3
  formula = At
  name = G4_At
  specific = 4
FEATURE [App::DocumentObjectGroupPython] Rn_element001  label="Rn_element : 1"  # scripted group (container) (typed FeaturePython)
  n = 1
  ref = Rn_element
FEATURE [App::DocumentObjectGroupPython] G4_Rn  # scripted group (container) (typed FeaturePython)
  Dunit = g/cm3
  Dvalue = 0.00900662
  Group = -> [Rn_element001]
  conduct = 2
  density = 1
  expand = 3
  formula = Rn
  name = G4_Rn
  specific = 4
FEATURE [App::DocumentObjectGroupPython] Fr_element001  label="Fr_element : 1"  # scripted group (container) (typed FeaturePython)
  n = 1
  ref = Fr_element
FEATURE [App::DocumentObjectGroupPython] G4_Fr  # scripted group (container) (typed FeaturePython)
  Dunit = g/cm3
  Dvalue = 1
  Group = -> [Fr_element001]
  conduct = 2
  density = 1
  expand = 3
  formula = Fr
  name = G4_Fr
  specific = 4
FEATURE [App::DocumentObjectGroupPython] Ra_element001  label="Ra_element : 1"  # scripted group (container) (typed FeaturePython)
  n = 1
  ref = Ra_element
FEATURE [App::DocumentObjectGroupPython] G4_Ra  # scripted group (container) (typed FeaturePython)
  Dunit = g/cm3
  Dvalue = 5
  Group = -> [Ra_element001]
  conduct = 2
  density = 1
  expand = 3
  formula = Ra
  name = G4_Ra
  specific = 4
FEATURE [App::DocumentObjectGroupPython] Ac_element001  label="Ac_element : 1"  # scripted group (container) (typed FeaturePython)
  n = 1
  ref = Ac_element
FEATURE [App::DocumentObjectGroupPython] G4_Ac  # scripted group (container) (typed FeaturePython)
  Dunit = g/cm3
  Dvalue = 10.07
  Group = -> [Ac_element001]
  conduct = 2
  density = 1
  expand = 3
  formula = Ac
  name = G4_Ac
  specific = 4
FEATURE [App::DocumentObjectGroupPython] Th_element001  label="Th_element : 1"  # scripted group (container) (typed FeaturePython)
  n = 1
  ref = Th_element
FEATURE [App::DocumentObjectGroupPython] G4_Th  # scripted group (container) (typed FeaturePython)
  Dunit = g/cm3
  Dvalue = 11.72
  Group = -> [Th_element001]
  conduct = 2
  density = 1
  expand = 3
  formula = Th
  name = G4_Th
  specific = 4
FEATURE [App::DocumentObjectGroupPython] Pa_element001  label="Pa_element : 1"  # scripted group (container) (typed FeaturePython)
  n = 1
  ref = Pa_element
FEATURE [App::DocumentObjectGroupPython] G4_Pa  # scripted group (container) (typed FeaturePython)
  Dunit = g/cm3
  Dvalue = 15.37
  Group = -> [Pa_element001]
  conduct = 2
  density = 1
  expand = 3
  formula = Pa
  name = G4_Pa
  specific = 4
FEATURE [App::DocumentObjectGroupPython] U_element004  label="U_element : 004"  # scripted group (container) (typed FeaturePython)
  n = 1
  ref = U_element
FEATURE [App::DocumentObjectGroupPython] G4_U  # scripted group (container) (typed FeaturePython)
  Dunit = g/cm3
  Dvalue = 18.95
  Group = -> [U_element004]
  conduct = 2
  density = 1
  expand = 3
  formula = U
  name = G4_U
  specific = 4
FEATURE [App::DocumentObjectGroupPython] Np_element001  label="Np_element : 1"  # scripted group (container) (typed FeaturePython)
  n = 1
  ref = Np_element
FEATURE [App::DocumentObjectGroupPython] G4_Np  # scripted group (container) (typed FeaturePython)
  Dunit = g/cm3
  Dvalue = 20.25
  Group = -> [Np_element001]
  conduct = 2
  density = 1
  expand = 3
  formula = Np
  name = G4_Np
  specific = 4
FEATURE [App::DocumentObjectGroupPython] Pu_element002  label="Pu_element : 002"  # scripted group (container) (typed FeaturePython)
  n = 1
  ref = Pu_element
FEATURE [App::DocumentObjectGroupPython] G4_Pu  # scripted group (container) (typed FeaturePython)
  Dunit = g/cm3
  Dvalue = 19.84
  Group = -> [Pu_element002]
  conduct = 2
  density = 1
  expand = 3
  formula = Pu
  name = G4_Pu
  specific = 4
FEATURE [App::DocumentObjectGroupPython] Am_element001  label="Am_element : 1"  # scripted group (container) (typed FeaturePython)
  n = 1
  ref = Am_element
FEATURE [App::DocumentObjectGroupPython] G4_Am  # scripted group (container) (typed FeaturePython)
  Dunit = g/cm3
  Dvalue = 13.67
  Group = -> [Am_element001]
  conduct = 2
  density = 1
  expand = 3
  formula = Am
  name = G4_Am
  specific = 4
FEATURE [App::DocumentObjectGroupPython] Cm_element001  label="Cm_element : 1"  # scripted group (container) (typed FeaturePython)
  n = 1
  ref = Cm_element
FEATURE [App::DocumentObjectGroupPython] G4_Cm  # scripted group (container) (typed FeaturePython)
  Dunit = g/cm3
  Dvalue = 13.51
  Group = -> [Cm_element001]
  conduct = 2
  density = 1
  expand = 3
  formula = Cm
  name = G4_Cm
  specific = 4
FEATURE [App::DocumentObjectGroupPython] Bk_element001  label="Bk_element : 1"  # scripted group (container) (typed FeaturePython)
  n = 1
  ref = Bk_element
FEATURE [App::DocumentObjectGroupPython] G4_Bk  # scripted group (container) (typed FeaturePython)
  Dunit = g/cm3
  Dvalue = 14
  Group = -> [Bk_element001]
  conduct = 2
  density = 1
  expand = 3
  formula = Bk
  name = G4_Bk
  specific = 4
FEATURE [App::DocumentObjectGroupPython] Cf_element001  label="Cf_element : 1"  # scripted group (container) (typed FeaturePython)
  n = 1
  ref = Cf_element
FEATURE [App::DocumentObjectGroupPython] G4_Cf  # scripted group (container) (typed FeaturePython)
  Dunit = g/cm3
  Dvalue = 10
  Group = -> [Cf_element001]
  conduct = 2
  density = 1
  expand = 3
  formula = Cf
  name = G4_Cf
  specific = 4
FEATURE [App::DocumentObjectGroupPython] Element  # scripted group (container) (typed FeaturePython)
  Group = -> [G4_H,G4_He,G4_Li,G4_Be,G4_B,G4_C,G4_N,G4_O,G4_F,G4_Ne,G4_Na,G4_Mg,G4_Al,G4_Si,G4_P,G4_S,G4_Cl,G4_Ar,G4_K,G4_Ca,G4_Sc,G4_Ti,G4_V,G4_Cr,G4_Mn,G4_Fe,G4_Co,G4_Ni,G4_Cu,G4_Zn,G4_Ga,G4_Ge,G4_As,G4_Se,G4_Br,G4_Kr,G4_Rb,G4_Sr,G4_Y,G4_Zr,G4_Nb,G4_Mo,G4_Tc,G4_Ru,G4_Rh,G4_Pd,G4_Ag,G4_Cd,G4_In,G4_Sn,G4_Sb,G4_Te,G4_I,G4_Xe,G4_Cs,G4_Ba,G4_La,G4_Ce,G4_Pr,G4_Nd,G4_Pm,G4_Sm,G4_Eu,G4_Gd,G4_Tb,G4_Dy,G4_Ho,G4_Er,+30 more]
FEATURE [App::DocumentObjectGroupPython] H_element114  label="H_element : 063"  # scripted group (container) (typed FeaturePython)
  n = 2
  ref = H_element
FEATURE [App::DocumentObjectGroupPython] G4_lH2  # scripted group (container) (typed FeaturePython)
  Dunit = g/cm3
  Dvalue = 0.0708
  Group = -> [H_element114]
  conduct = 2
  density = 1
  expand = 3
  formula = G4_lH2
  name = G4_lH2
  specific = 4
FEATURE [App::DocumentObjectGroupPython] N_element049  label="N_element : 022"  # scripted group (container) (typed FeaturePython)
  n = 2
  ref = N_element
FEATURE [App::DocumentObjectGroupPython] G4_lN2  # scripted group (container) (typed FeaturePython)
  Dunit = g/cm3
  Dvalue = 0.807
  Group = -> [N_element049]
  conduct = 2
  density = 1
  expand = 3
  formula = G4_lN2
  name = G4_lN2
  specific = 4
FEATURE [App::DocumentObjectGroupPython] O_element106  label="O_element : 060"  # scripted group (container) (typed FeaturePython)
  n = 2
  ref = O_element
FEATURE [App::DocumentObjectGroupPython] G4_lO2  # scripted group (container) (typed FeaturePython)
  Dunit = g/cm3
  Dvalue = 1.141
  Group = -> [O_element106]
  conduct = 2
  density = 1
  expand = 3
  formula = G4_lO2
  name = G4_lO2
  specific = 4
FEATURE [App::DocumentObjectGroupPython] Ar  label="Ar : 1"  # scripted group (container) (typed FeaturePython)
  n = 1
  ref = Ar
FEATURE [App::DocumentObjectGroupPython] G4_lAr  # scripted group (container) (typed FeaturePython)
  Dunit = g/cm3
  Dvalue = 1.396
  Group = -> [Ar]
  conduct = 2
  density = 1
  expand = 3
  formula = G4_lAr
  name = G4_lAr
  specific = 4
FEATURE [App::DocumentObjectGroupPython] Br  label="Br : 1"  # scripted group (container) (typed FeaturePython)
  n = 1
  ref = Br
FEATURE [App::DocumentObjectGroupPython] G4_lBr  # scripted group (container) (typed FeaturePython)
  Dunit = g/cm3
  Dvalue = 3.1028
  Group = -> [Br]
  conduct = 2
  density = 1
  expand = 3
  formula = G4_lBr
  name = G4_lBr
  specific = 4
FEATURE [App::DocumentObjectGroupPython] Kr  label="Kr : 1"  # scripted group (container) (typed FeaturePython)
  n = 1
  ref = Kr
FEATURE [App::DocumentObjectGroupPython] G4_lKr  # scripted group (container) (typed FeaturePython)
  Dunit = g/cm3
  Dvalue = 2.418
  Group = -> [Kr]
  conduct = 2
  density = 1
  expand = 3
  formula = G4_lKr
  name = G4_lKr
  specific = 4
FEATURE [App::DocumentObjectGroupPython] Xe  label="Xe : 1"  # scripted group (container) (typed FeaturePython)
  n = 1
  ref = Xe
FEATURE [App::DocumentObjectGroupPython] G4_lXe  # scripted group (container) (typed FeaturePython)
  Dunit = g/cm3
  Dvalue = 2.953
  Group = -> [Xe]
  conduct = 2
  density = 1
  expand = 3
  formula = G4_lXe
  name = G4_lXe
  specific = 4
FEATURE [App::DocumentObjectGroupPython] O_element107  label="O_element : 061"  # scripted group (container) (typed FeaturePython)
  n = 4
  ref = O_element
FEATURE [App::DocumentObjectGroupPython] Pb_element004  label="Pb_element : 002"  # scripted group (container) (typed FeaturePython)
  n = 1
  ref = Pb_element
FEATURE [App::DocumentObjectGroupPython] W_element005  label="W_element : 005"  # scripted group (container) (typed FeaturePython)
  n = 1
  ref = W_element
FEATURE [App::DocumentObjectGroupPython] G4_PbWO4  # scripted group (container) (typed FeaturePython)
  Dunit = g/cm3
  Dvalue = 8.28
  Group = -> [O_element107,Pb_element004,W_element005]
  conduct = 2
  density = 1
  expand = 3
  formula = G4_PbWO4
  name = G4_PbWO4
  specific = 4
FEATURE [App::DocumentObjectGroupPython] alactic  label="alactic : 1"  # scripted group (container) (typed FeaturePython)
  n = 1
  ref = alactic
FEATURE [App::DocumentObjectGroupPython] G4_Galactic  # scripted group (container) (typed FeaturePython)
  Dunit = g/cm3
  Dvalue = 0
  Group = -> [alactic]
  conduct = 2
  density = 1
  expand = 3
  formula = G4_Galactic
  name = G4_Galactic
  specific = 4
FEATURE [App::DocumentObjectGroupPython] RAPHITE_POROUS  label="RAPHITE_POROUS : 1"  # scripted group (container) (typed FeaturePython)
  n = 1
  ref = RAPHITE_POROUS
FEATURE [App::DocumentObjectGroupPython] G4_GRAPHITE_POROUS  # scripted group (container) (typed FeaturePython)
  Dunit = g/cm3
  Dvalue = 1.7
  Group = -> [RAPHITE_POROUS]
  conduct = 2
  density = 1
  expand = 3
  formula = G4_GRAPHITE_POROUS
  name = G4_GRAPHITE_POROUS
  specific = 4
FEATURE [App::DocumentObjectGroupPython] H_element115  label="H_element : 0.150"  # scripted group (container) (typed FeaturePython)
  n = 0.080538
FEATURE [App::DocumentObjectGroupPython] C_element125  label="C_element : 0.600"  # scripted group (container) (typed FeaturePython)
  n = 0.599848
FEATURE [App::DocumentObjectGroupPython] O_element108  label="O_element : 0.320"  # scripted group (container) (typed FeaturePython)
  n = 0.319614
FEATURE [App::DocumentObjectGroupPython] G4_LUCITE  # scripted group (container) (typed FeaturePython)
  Dunit = g/cm3
  Dvalue = 1.19
  Group = -> [H_element115,C_element125,O_element108]
  conduct = 2
  density = 1
  expand = 3
  formula = G4_LUCITE
  name = G4_LUCITE
  specific = 4
FEATURE [App::DocumentObjectGroupPython] Cu_element002  label="Cu_element : 62"  # scripted group (container) (typed FeaturePython)
  n = 62
  ref = Cu_element
FEATURE [App::DocumentObjectGroupPython] Zn_element002  label="Zn_element : 35"  # scripted group (container) (typed FeaturePython)
  n = 35
  ref = Zn_element
FEATURE [App::DocumentObjectGroupPython] Pb_element005  label="Pb_element : 3"  # scripted group (container) (typed FeaturePython)
  n = 3
  ref = Pb_element
FEATURE [App::DocumentObjectGroupPython] G4_BRASS  # scripted group (container) (typed FeaturePython)
  Dunit = g/cm3
  Dvalue = 8.52
  Group = -> [Cu_element002,Zn_element002,Pb_element005]
  conduct = 2
  density = 1
  expand = 3
  formula = G4_BRASS
  name = G4_BRASS
  specific = 4
FEATURE [App::DocumentObjectGroupPython] Cu_element003  label="Cu_element : 89"  # scripted group (container) (typed FeaturePython)
  n = 89
  ref = Cu_element
FEATURE [App::DocumentObjectGroupPython] Zn_element003  label="Zn_element : 9"  # scripted group (container) (typed FeaturePython)
  n = 9
  ref = Zn_element
FEATURE [App::DocumentObjectGroupPython] Pb_element006  label="Pb_element : 2"  # scripted group (container) (typed FeaturePython)
  n = 2
  ref = Pb_element
FEATURE [App::DocumentObjectGroupPython] G4_BRONZE  # scripted group (container) (typed FeaturePython)
  Dunit = g/cm3
  Dvalue = 8.82
  Group = -> [Cu_element003,Zn_element003,Pb_element006]
  conduct = 2
  density = 1
  expand = 3
  formula = G4_BRONZE
  name = G4_BRONZE
  specific = 4
FEATURE [App::DocumentObjectGroupPython] Fe_element008  label="Fe_element : 74"  # scripted group (container) (typed FeaturePython)
  n = 74
  ref = Fe_element
FEATURE [App::DocumentObjectGroupPython] Cr_element002  label="Cr_element : 18"  # scripted group (container) (typed FeaturePython)
  n = 18
  ref = Cr_element
FEATURE [App::DocumentObjectGroupPython] Ni_element002  label="Ni_element : 8"  # scripted group (container) (typed FeaturePython)
  n = 8
  ref = Ni_element
FEATURE [App::DocumentObjectGroupPython] G4_STAINLESS_STEEL  label="G4_STAINLESS-STEEL"  # scripted group (container) (typed FeaturePython)
  Dunit = g/cm3
  Dvalue = 8
  Group = -> [Fe_element008,Cr_element002,Ni_element002]
  conduct = 2
  density = 1
  expand = 3
  formula = G4_STAINLESS-STEEL
  name = G4_STAINLESS-STEEL
  specific = 4
FEATURE [App::DocumentObjectGroupPython] H_element116  label="H_element : 064"  # scripted group (container) (typed FeaturePython)
  n = 18
  ref = H_element
FEATURE [App::DocumentObjectGroupPython] C_element126  label="C_element : 071"  # scripted group (container) (typed FeaturePython)
  n = 12
  ref = C_element
FEATURE [App::DocumentObjectGroupPython] O_element109  label="O_element : 062"  # scripted group (container) (typed FeaturePython)
  n = 7
  ref = O_element
FEATURE [App::DocumentObjectGroupPython] G4_CR39  # scripted group (container) (typed FeaturePython)
  Dunit = g/cm3
  Dvalue = 1.32
  Group = -> [H_element116,C_element126,O_element109]
  conduct = 2
  density = 1
  expand = 3
  formula = G4_CR39
  name = G4_CR39
  specific = 4
FEATURE [App::DocumentObjectGroupPython] H_element117  label="H_element : 38"  # scripted group (container) (typed FeaturePython)
  n = 38
  ref = H_element
FEATURE [App::DocumentObjectGroupPython] C_element127  label="C_element : 072"  # scripted group (container) (typed FeaturePython)
  n = 18
  ref = C_element
FEATURE [App::DocumentObjectGroupPython] O_element110  label="O_element : 063"  # scripted group (container) (typed FeaturePython)
  n = 1
  ref = O_element
FEATURE [App::DocumentObjectGroupPython] G4_OCTADECANOL  # scripted group (container) (typed FeaturePython)
  Dunit = g/cm3
  Dvalue = 0.812
  Group = -> [H_element117,C_element127,O_element110]
  conduct = 2
  density = 1
  expand = 3
  formula = G4_OCTADECANOL
  name = G4_OCTADECANOL
  specific = 4
FEATURE [App::DocumentObjectGroupPython] HEP  # scripted group (container) (typed FeaturePython)
  Group = -> [G4_lH2,G4_lN2,G4_lO2,G4_lAr,G4_lBr,G4_lKr,G4_lXe,G4_PbWO4,G4_Galactic,G4_GRAPHITE_POROUS,G4_LUCITE,G4_BRASS,G4_BRONZE,G4_STAINLESS_STEEL,G4_CR39,G4_OCTADECANOL]
FEATURE [App::DocumentObjectGroupPython] C_element128  label="C_element : 073"  # scripted group (container) (typed FeaturePython)
  n = 14
  ref = C_element
FEATURE [App::DocumentObjectGroupPython] H_element118  label="H_element : 065"  # scripted group (container) (typed FeaturePython)
  n = 10
  ref = H_element
FEATURE [App::DocumentObjectGroupPython] O_element111  label="O_element : 064"  # scripted group (container) (typed FeaturePython)
  n = 2
  ref = O_element
FEATURE [App::DocumentObjectGroupPython] N_element050  label="N_element : 023"  # scripted group (container) (typed FeaturePython)
  n = 2
  ref = N_element
FEATURE [App::DocumentObjectGroupPython] G4_KEVLAR  # scripted group (container) (typed FeaturePython)
  Dunit = g/cm3
  Dvalue = 1.44
  Group = -> [C_element128,H_element118,O_element111,N_element050]
  conduct = 2
  density = 1
  expand = 3
  formula = G4_KEVLAR
  name = G4_KEVLAR
  specific = 4
FEATURE [App::DocumentObjectGroupPython] C_element129  label="C_element : 074"  # scripted group (container) (typed FeaturePython)
  n = 10
  ref = C_element
FEATURE [App::DocumentObjectGroupPython] H_element119  label="H_element : 066"  # scripted group (container) (typed FeaturePython)
  n = 8
  ref = H_element
FEATURE [App::DocumentObjectGroupPython] O_element112  label="O_element : 065"  # scripted group (container) (typed FeaturePython)
  n = 4
  ref = O_element
FEATURE [App::DocumentObjectGroupPython] G4_DACRON  # scripted group (container) (typed FeaturePython)
  Dunit = g/cm3
  Dvalue = 1.4
  Group = -> [C_element129,H_element119,O_element112]
  conduct = 2
  density = 1
  expand = 3
  formula = G4_DACRON
  name = G4_DACRON
  specific = 4
FEATURE [App::DocumentObjectGroupPython] C_element130  label="C_element : 075"  # scripted group (container) (typed FeaturePython)
  n = 4
  ref = C_element
FEATURE [App::DocumentObjectGroupPython] H_element120  label="H_element : 067"  # scripted group (container) (typed FeaturePython)
  n = 5
  ref = H_element
FEATURE [App::DocumentObjectGroupPython] Cl_element030  label="Cl_element : 016"  # scripted group (container) (typed FeaturePython)
  n = 1
  ref = Cl_element
FEATURE [App::DocumentObjectGroupPython] G4_NEOPRENE  # scripted group (container) (typed FeaturePython)
  Dunit = g/cm3
  Dvalue = 1.23
  Group = -> [C_element130,H_element120,Cl_element030]
  conduct = 2
  density = 1
  expand = 3
  formula = G4_NEOPRENE
  name = G4_NEOPRENE
  specific = 4
FEATURE [App::DocumentObjectGroupPython] Space  # scripted group (container) (typed FeaturePython)
  Group = -> [G4_KEVLAR,G4_DACRON,G4_NEOPRENE]
FEATURE [App::DocumentObjectGroupPython] H_element121  label="H_element : 068"  # scripted group (container) (typed FeaturePython)
  n = 5
  ref = H_element
FEATURE [App::DocumentObjectGroupPython] C_element131  label="C_element : 076"  # scripted group (container) (typed FeaturePython)
  n = 4
  ref = C_element
FEATURE [App::DocumentObjectGroupPython] N_element051  label="N_element : 3"  # scripted group (container) (typed FeaturePython)
  n = 3
  ref = N_element
FEATURE [App::DocumentObjectGroupPython] O_element113  label="O_element : 066"  # scripted group (container) (typed FeaturePython)
  n = 1
  ref = O_element
FEATURE [App::DocumentObjectGroupPython] G4_CYTOSINE  # scripted group (container) (typed FeaturePython)
  Dunit = g/cm3
  Dvalue = 1.55
  Group = -> [H_element121,C_element131,N_element051,O_element113]
  conduct = 2
  density = 1
  expand = 3
  formula = G4_CYTOSINE
  name = G4_CYTOSINE
  specific = 4
FEATURE [App::DocumentObjectGroupPython] H_element122  label="H_element : 069"  # scripted group (container) (typed FeaturePython)
  n = 6
  ref = H_element
FEATURE [App::DocumentObjectGroupPython] C_element132  label="C_element : 077"  # scripted group (container) (typed FeaturePython)
  n = 5
  ref = C_element
FEATURE [App::DocumentObjectGroupPython] N_element052  label="N_element : 024"  # scripted group (container) (typed FeaturePython)
  n = 2
  ref = N_element
FEATURE [App::DocumentObjectGroupPython] O_element114  label="O_element : 067"  # scripted group (container) (typed FeaturePython)
  n = 2
  ref = O_element
FEATURE [App::DocumentObjectGroupPython] G4_THYMINE  # scripted group (container) (typed FeaturePython)
  Dunit = g/cm3
  Dvalue = 1.23
  Group = -> [H_element122,C_element132,N_element052,O_element114]
  conduct = 2
  density = 1
  expand = 3
  formula = G4_THYMINE
  name = G4_THYMINE
  specific = 4
FEATURE [App::DocumentObjectGroupPython] H_element123  label="H_element : 070"  # scripted group (container) (typed FeaturePython)
  n = 4
  ref = H_element
FEATURE [App::DocumentObjectGroupPython] C_element133  label="C_element : 078"  # scripted group (container) (typed FeaturePython)
  n = 4
  ref = C_element
FEATURE [App::DocumentObjectGroupPython] N_element053  label="N_element : 025"  # scripted group (container) (typed FeaturePython)
  n = 2
  ref = N_element
FEATURE [App::DocumentObjectGroupPython] O_element115  label="O_element : 068"  # scripted group (container) (typed FeaturePython)
  n = 2
  ref = O_element
FEATURE [App::DocumentObjectGroupPython] G4_URACIL  # scripted group (container) (typed FeaturePython)
  Dunit = g/cm3
  Dvalue = 1.32
  Group = -> [H_element123,C_element133,N_element053,O_element115]
  conduct = 2
  density = 1
  expand = 3
  formula = G4_URACIL
  name = G4_URACIL
  specific = 4
FEATURE [App::DocumentObjectGroupPython] H_element124  label="H_element : 071"  # scripted group (container) (typed FeaturePython)
  n = 4
  ref = H_element
FEATURE [App::DocumentObjectGroupPython] C_element134  label="C_element : 079"  # scripted group (container) (typed FeaturePython)
  n = 5
  ref = C_element
FEATURE [App::DocumentObjectGroupPython] N_element054  label="N_element : 026"  # scripted group (container) (typed FeaturePython)
  n = 5
  ref = N_element
FEATURE [App::DocumentObjectGroupPython] G4_DNA_ADENINE  # scripted group (container) (typed FeaturePython)
  Dunit = g/cm3
  Dvalue = 1
  Group = -> [H_element124,C_element134,N_element054]
  conduct = 2
  density = 1
  expand = 3
  formula = G4_DNA_ADENINE
  name = G4_DNA_ADENINE
  specific = 4
FEATURE [App::DocumentObjectGroupPython] H_element125  label="H_element : 072"  # scripted group (container) (typed FeaturePython)
  n = 4
  ref = H_element
FEATURE [App::DocumentObjectGroupPython] C_element135  label="C_element : 080"  # scripted group (container) (typed FeaturePython)
  n = 5
  ref = C_element
FEATURE [App::DocumentObjectGroupPython] N_element055  label="N_element : 027"  # scripted group (container) (typed FeaturePython)
  n = 5
  ref = N_element
FEATURE [App::DocumentObjectGroupPython] O_element116  label="O_element : 069"  # scripted group (container) (typed FeaturePython)
  n = 1
  ref = O_element
FEATURE [App::DocumentObjectGroupPython] G4_DNA_GUANINE  # scripted group (container) (typed FeaturePython)
  Dunit = g/cm3
  Dvalue = 1
  Group = -> [H_element125,C_element135,N_element055,O_element116]
  conduct = 2
  density = 1
  expand = 3
  formula = G4_DNA_GUANINE
  name = G4_DNA_GUANINE
  specific = 4
FEATURE [App::DocumentObjectGroupPython] H_element126  label="H_element : 073"  # scripted group (container) (typed FeaturePython)
  n = 4
  ref = H_element
FEATURE [App::DocumentObjectGroupPython] C_element136  label="C_element : 081"  # scripted group (container) (typed FeaturePython)
  n = 4
  ref = C_element
FEATURE [App::DocumentObjectGroupPython] N_element056  label="N_element : 028"  # scripted group (container) (typed FeaturePython)
  n = 3
  ref = N_element
FEATURE [App::DocumentObjectGroupPython] O_element117  label="O_element : 070"  # scripted group (container) (typed FeaturePython)
  n = 1
  ref = O_element
FEATURE [App::DocumentObjectGroupPython] G4_DNA_CYTOSINE  # scripted group (container) (typed FeaturePython)
  Dunit = g/cm3
  Dvalue = 1
  Group = -> [H_element126,C_element136,N_element056,O_element117]
  conduct = 2
  density = 1
  expand = 3
  formula = G4_DNA_CYTOSINE
  name = G4_DNA_CYTOSINE
  specific = 4
FEATURE [App::DocumentObjectGroupPython] H_element127  label="H_element : 074"  # scripted group (container) (typed FeaturePython)
  n = 5
  ref = H_element
FEATURE [App::DocumentObjectGroupPython] C_element137  label="C_element : 082"  # scripted group (container) (typed FeaturePython)
  n = 5
  ref = C_element
FEATURE [App::DocumentObjectGroupPython] N_element057  label="N_element : 029"  # scripted group (container) (typed FeaturePython)
  n = 2
  ref = N_element
FEATURE [App::DocumentObjectGroupPython] O_element118  label="O_element : 071"  # scripted group (container) (typed FeaturePython)
  n = 2
  ref = O_element
FEATURE [App::DocumentObjectGroupPython] G4_DNA_THYMINE  # scripted group (container) (typed FeaturePython)
  Dunit = g/cm3
  Dvalue = 1
  Group = -> [H_element127,C_element137,N_element057,O_element118]
  conduct = 2
  density = 1
  expand = 3
  formula = G4_DNA_THYMINE
  name = G4_DNA_THYMINE
  specific = 4
FEATURE [App::DocumentObjectGroupPython] H_element128  label="H_element : 075"  # scripted group (container) (typed FeaturePython)
  n = 3
  ref = H_element
FEATURE [App::DocumentObjectGroupPython] C_element138  label="C_element : 083"  # scripted group (container) (typed FeaturePython)
  n = 4
  ref = C_element
FEATURE [App::DocumentObjectGroupPython] N_element058  label="N_element : 030"  # scripted group (container) (typed FeaturePython)
  n = 2
  ref = N_element
FEATURE [App::DocumentObjectGroupPython] O_element119  label="O_element : 072"  # scripted group (container) (typed FeaturePython)
  n = 2
  ref = O_element
FEATURE [App::DocumentObjectGroupPython] G4_DNA_URACIL  # scripted group (container) (typed FeaturePython)
  Dunit = g/cm3
  Dvalue = 1
  Group = -> [H_element128,C_element138,N_element058,O_element119]
  conduct = 2
  density = 1
  expand = 3
  formula = G4_DNA_URACIL
  name = G4_DNA_URACIL
  specific = 4
FEATURE [App::DocumentObjectGroupPython] H_element129  label="H_element : 076"  # scripted group (container) (typed FeaturePython)
  n = 10
  ref = H_element
FEATURE [App::DocumentObjectGroupPython] C_element139  label="C_element : 084"  # scripted group (container) (typed FeaturePython)
  n = 10
  ref = C_element
FEATURE [App::DocumentObjectGroupPython] N_element059  label="N_element : 031"  # scripted group (container) (typed FeaturePython)
  n = 5
  ref = N_element
FEATURE [App::DocumentObjectGroupPython] O_element120  label="O_element : 073"  # scripted group (container) (typed FeaturePython)
  n = 4
  ref = O_element
FEATURE [App::DocumentObjectGroupPython] G4_DNA_ADENOSINE  # scripted group (container) (typed FeaturePython)
  Dunit = g/cm3
  Dvalue = 1
  Group = -> [H_element129,C_element139,N_element059,O_element120]
  conduct = 2
  density = 1
  expand = 3
  formula = G4_DNA_ADENOSINE
  name = G4_DNA_ADENOSINE
  specific = 4
FEATURE [App::DocumentObjectGroupPython] H_element130  label="H_element : 077"  # scripted group (container) (typed FeaturePython)
  n = 10
  ref = H_element
FEATURE [App::DocumentObjectGroupPython] C_element140  label="C_element : 085"  # scripted group (container) (typed FeaturePython)
  n = 10
  ref = C_element
FEATURE [App::DocumentObjectGroupPython] N_element060  label="N_element : 032"  # scripted group (container) (typed FeaturePython)
  n = 5
  ref = N_element
FEATURE [App::DocumentObjectGroupPython] O_element121  label="O_element : 074"  # scripted group (container) (typed FeaturePython)
  n = 5
  ref = O_element
FEATURE [App::DocumentObjectGroupPython] G4_DNA_GUANOSINE  # scripted group (container) (typed FeaturePython)
  Dunit = g/cm3
  Dvalue = 1
  Group = -> [H_element130,C_element140,N_element060,O_element121]
  conduct = 2
  density = 1
  expand = 3
  formula = G4_DNA_GUANOSINE
  name = G4_DNA_GUANOSINE
  specific = 4
FEATURE [App::DocumentObjectGroupPython] H_element131  label="H_element : 078"  # scripted group (container) (typed FeaturePython)
  n = 10
  ref = H_element
FEATURE [App::DocumentObjectGroupPython] C_element141  label="C_element : 086"  # scripted group (container) (typed FeaturePython)
  n = 9
  ref = C_element
FEATURE [App::DocumentObjectGroupPython] N_element061  label="N_element : 033"  # scripted group (container) (typed FeaturePython)
  n = 3
  ref = N_element
FEATURE [App::DocumentObjectGroupPython] O_element122  label="O_element : 075"  # scripted group (container) (typed FeaturePython)
  n = 5
  ref = O_element
FEATURE [App::DocumentObjectGroupPython] G4_DNA_CYTIDINE  # scripted group (container) (typed FeaturePython)
  Dunit = g/cm3
  Dvalue = 1
  Group = -> [H_element131,C_element141,N_element061,O_element122]
  conduct = 2
  density = 1
  expand = 3
  formula = G4_DNA_CYTIDINE
  name = G4_DNA_CYTIDINE
  specific = 4
FEATURE [App::DocumentObjectGroupPython] H_element132  label="H_element : 079"  # scripted group (container) (typed FeaturePython)
  n = 9
  ref = H_element
FEATURE [App::DocumentObjectGroupPython] C_element142  label="C_element : 087"  # scripted group (container) (typed FeaturePython)
  n = 9
  ref = C_element
FEATURE [App::DocumentObjectGroupPython] N_element062  label="N_element : 034"  # scripted group (container) (typed FeaturePython)
  n = 2
  ref = N_element
FEATURE [App::DocumentObjectGroupPython] O_element123  label="O_element : 076"  # scripted group (container) (typed FeaturePython)
  n = 6
  ref = O_element
FEATURE [App::DocumentObjectGroupPython] G4_DNA_URIDINE  # scripted group (container) (typed FeaturePython)
  Dunit = g/cm3
  Dvalue = 1
  Group = -> [H_element132,C_element142,N_element062,O_element123]
  conduct = 2
  density = 1
  expand = 3
  formula = G4_DNA_URIDINE
  name = G4_DNA_URIDINE
  specific = 4
FEATURE [App::DocumentObjectGroupPython] H_element133  label="H_element : 080"  # scripted group (container) (typed FeaturePython)
  n = 11
  ref = H_element
FEATURE [App::DocumentObjectGroupPython] C_element143  label="C_element : 088"  # scripted group (container) (typed FeaturePython)
  n = 10
  ref = C_element
FEATURE [App::DocumentObjectGroupPython] N_element063  label="N_element : 035"  # scripted group (container) (typed FeaturePython)
  n = 2
  ref = N_element
FEATURE [App::DocumentObjectGroupPython] O_element124  label="O_element : 077"  # scripted group (container) (typed FeaturePython)
  n = 6
  ref = O_element
FEATURE [App::DocumentObjectGroupPython] G4_DNA_METHYLURIDINE  # scripted group (container) (typed FeaturePython)
  Dunit = g/cm3
  Dvalue = 1
  Group = -> [H_element133,C_element143,N_element063,O_element124]
  conduct = 2
  density = 1
  expand = 3
  formula = G4_DNA_METHYLURIDINE
  name = G4_DNA_METHYLURIDINE
  specific = 4
FEATURE [App::DocumentObjectGroupPython] P_element014  label="P_element : 003"  # scripted group (container) (typed FeaturePython)
  n = 1
  ref = P_element
FEATURE [App::DocumentObjectGroupPython] O_element125  label="O_element : 078"  # scripted group (container) (typed FeaturePython)
  n = 3
  ref = O_element
FEATURE [App::DocumentObjectGroupPython] G4_DNA_MONOPHOSPHATE  # scripted group (container) (typed FeaturePython)
  Dunit = g/cm3
  Dvalue = 1
  Group = -> [P_element014,O_element125]
  conduct = 2
  density = 1
  expand = 3
  formula = G4_DNA_MONOPHOSPHATE
  name = G4_DNA_MONOPHOSPHATE
  specific = 4
FEATURE [App::DocumentObjectGroupPython] H_element134  label="H_element : 081"  # scripted group (container) (typed FeaturePython)
  n = 10
  ref = H_element
FEATURE [App::DocumentObjectGroupPython] C_element144  label="C_element : 089"  # scripted group (container) (typed FeaturePython)
  n = 10
  ref = C_element
FEATURE [App::DocumentObjectGroupPython] N_element064  label="N_element : 036"  # scripted group (container) (typed FeaturePython)
  n = 5
  ref = N_element
FEATURE [App::DocumentObjectGroupPython] O_element126  label="O_element : 079"  # scripted group (container) (typed FeaturePython)
  n = 7
  ref = O_element
FEATURE [App::DocumentObjectGroupPython] P_element015  label="P_element : 004"  # scripted group (container) (typed FeaturePython)
  n = 1
  ref = P_element
FEATURE [App::DocumentObjectGroupPython] G4_DNA_A  # scripted group (container) (typed FeaturePython)
  Dunit = g/cm3
  Dvalue = 1
  Group = -> [H_element134,C_element144,N_element064,O_element126,P_element015]
  conduct = 2
  density = 1
  expand = 3
  formula = G4_DNA_A
  name = G4_DNA_A
  specific = 4
FEATURE [App::DocumentObjectGroupPython] H_element135  label="H_element : 082"  # scripted group (container) (typed FeaturePython)
  n = 10
  ref = H_element
FEATURE [App::DocumentObjectGroupPython] C_element145  label="C_element : 090"  # scripted group (container) (typed FeaturePython)
  n = 10
  ref = C_element
FEATURE [App::DocumentObjectGroupPython] N_element065  label="N_element : 037"  # scripted group (container) (typed FeaturePython)
  n = 5
  ref = N_element
FEATURE [App::DocumentObjectGroupPython] O_element127  label="O_element : 8"  # scripted group (container) (typed FeaturePython)
  n = 8
  ref = O_element
FEATURE [App::DocumentObjectGroupPython] P_element016  label="P_element : 005"  # scripted group (container) (typed FeaturePython)
  n = 1
  ref = P_element
FEATURE [App::DocumentObjectGroupPython] G4_DNA_G  # scripted group (container) (typed FeaturePython)
  Dunit = g/cm3
  Dvalue = 1
  Group = -> [H_element135,C_element145,N_element065,O_element127,P_element016]
  conduct = 2
  density = 1
  expand = 3
  formula = G4_DNA_G
  name = G4_DNA_G
  specific = 4
FEATURE [App::DocumentObjectGroupPython] H_element136  label="H_element : 083"  # scripted group (container) (typed FeaturePython)
  n = 10
  ref = H_element
FEATURE [App::DocumentObjectGroupPython] C_element146  label="C_element : 091"  # scripted group (container) (typed FeaturePython)
  n = 9
  ref = C_element
FEATURE [App::DocumentObjectGroupPython] N_element066  label="N_element : 038"  # scripted group (container) (typed FeaturePython)
  n = 3
  ref = N_element
FEATURE [App::DocumentObjectGroupPython] O_element128  label="O_element : 080"  # scripted group (container) (typed FeaturePython)
  n = 8
  ref = O_element
FEATURE [App::DocumentObjectGroupPython] P_element017  label="P_element : 006"  # scripted group (container) (typed FeaturePython)
  n = 1
  ref = P_element
FEATURE [App::DocumentObjectGroupPython] G4_DNA_C  # scripted group (container) (typed FeaturePython)
  Dunit = g/cm3
  Dvalue = 1
  Group = -> [H_element136,C_element146,N_element066,O_element128,P_element017]
  conduct = 2
  density = 1
  expand = 3
  formula = G4_DNA_C
  name = G4_DNA_C
  specific = 4
FEATURE [App::DocumentObjectGroupPython] H_element137  label="H_element : 084"  # scripted group (container) (typed FeaturePython)
  n = 9
  ref = H_element
FEATURE [App::DocumentObjectGroupPython] C_element147  label="C_element : 092"  # scripted group (container) (typed FeaturePython)
  n = 9
  ref = C_element
FEATURE [App::DocumentObjectGroupPython] N_element067  label="N_element : 039"  # scripted group (container) (typed FeaturePython)
  n = 2
  ref = N_element
FEATURE [App::DocumentObjectGroupPython] O_element129  label="O_element : 9"  # scripted group (container) (typed FeaturePython)
  n = 9
  ref = O_element
FEATURE [App::DocumentObjectGroupPython] P_element018  label="P_element : 007"  # scripted group (container) (typed FeaturePython)
  n = 1
  ref = P_element
FEATURE [App::DocumentObjectGroupPython] G4_DNA_U  # scripted group (container) (typed FeaturePython)
  Dunit = g/cm3
  Dvalue = 1
  Group = -> [H_element137,C_element147,N_element067,O_element129,P_element018]
  conduct = 2
  density = 1
  expand = 3
  formula = G4_DNA_U
  name = G4_DNA_U
  specific = 4
FEATURE [App::DocumentObjectGroupPython] H_element138  label="H_element : 085"  # scripted group (container) (typed FeaturePython)
  n = 11
  ref = H_element
FEATURE [App::DocumentObjectGroupPython] C_element148  label="C_element : 093"  # scripted group (container) (typed FeaturePython)
  n = 10
  ref = C_element
FEATURE [App::DocumentObjectGroupPython] N_element068  label="N_element : 040"  # scripted group (container) (typed FeaturePython)
  n = 2
  ref = N_element
FEATURE [App::DocumentObjectGroupPython] O_element130  label="O_element : 081"  # scripted group (container) (typed FeaturePython)
  n = 9
  ref = O_element
FEATURE [App::DocumentObjectGroupPython] P_element019  label="P_element : 008"  # scripted group (container) (typed FeaturePython)
  n = 1
  ref = P_element
FEATURE [App::DocumentObjectGroupPython] G4_DNA_MU  # scripted group (container) (typed FeaturePython)
  Dunit = g/cm3
  Dvalue = 1
  Group = -> [H_element138,C_element148,N_element068,O_element130,P_element019]
  conduct = 2
  density = 1
  expand = 3
  formula = G4_DNA_MU
  name = G4_DNA_MU
  specific = 4
FEATURE [App::DocumentObjectGroupPython] BioChemical  # scripted group (container) (typed FeaturePython)
  Group = -> [G4_CYTOSINE,G4_THYMINE,G4_URACIL,G4_DNA_ADENINE,G4_DNA_GUANINE,G4_DNA_CYTOSINE,G4_DNA_THYMINE,G4_DNA_URACIL,G4_DNA_ADENOSINE,G4_DNA_GUANOSINE,G4_DNA_CYTIDINE,G4_DNA_URIDINE,G4_DNA_METHYLURIDINE,G4_DNA_MONOPHOSPHATE,G4_DNA_A,G4_DNA_G,G4_DNA_C,G4_DNA_U,G4_DNA_MU]
FEATURE [App::DocumentObjectGroupPython] G4Materials  # scripted group (container) (typed FeaturePython)
  Group = -> [NIST,Element,HEP,Space,BioChemical]
  version = 1
FEATURE [App::DocumentObjectGroupPython] Geant4  # scripted group (container) (typed FeaturePython)
  Group = -> [G4Isotopes,G4Elements,G4Materials]
FEATURE [App::DocumentObjectGroupPython] Materials  # scripted group (container) (typed FeaturePython)
  Group = -> [Geant4]
FEATURE [Part::FeaturePython] GDMLBox_WorldBox  # WARN: FeaturePython — macro-defined, semantics opaque (R4)
  lunit = 2
  material = 5
  x = 100
  y = 100
  z = 100
FEATURE [Sketcher::SketchObject] Sketch
  FullyConstrained = false
  sketch-geometry (15):
    g0-g5: Circle x6 (B-spline internal-alignment scaffolding for g6; pole/knot coordinates omitted)
    g6: BSplineCurve PolesCount=7 KnotsCount=5 Degree=3 IsPeriodic=0
    g7-g10: GeomPoint x4 (B-spline internal-alignment scaffolding for g6; pole/knot coordinates omitted)
    g11: LineSegment StartX=-4.39557 StartY=8.39124 StartZ=0 EndX=-5.2662 EndY=10.5884 EndZ=0
    g12: LineSegment StartX=-5.2662 StartY=10.5884 StartZ=0 EndX=-7.82152 EndY=9.89481 EndZ=0
    g13: LineSegment StartX=-7.82152 StartY=9.89481 StartZ=0 EndX=-9.50073 EndY=7.63152 EndZ=0
    g14: ArcOfCircle CenterX=-7.8377 CenterY=5.34547 CenterZ=0 NormalX=0 NormalY=0 NormalZ=1 AngleXU=0 Radius=2.82696 StartAngle=4.84147 EndAngle=8.48291
  constraints (9):
    c: Weight(g0) = 1
    c: Equal(g0, g1-g5) x5
    c: InternalAlignment(g0-g5 -> g6) x6
    c: InternalAlignment(g7-g10 -> g6) x4
    c: Coincident(g11,g6)
    c: Coincident(g11,g12)
    c: Coincident(g12,g13)
    c: Coincident(g14,g13)
    c: Coincident(g14,g6)
FEATURE [Part::Extrusion] Extrude
  Base = -> Sketch
  Dir = (0,0,1)
  DirMode = 2
  FaceMakerClass = Part::FaceMakerBullseye
  LengthFwd = 10
  LengthRev = 0
  Placement = pos=(13,9,0) rot=(0,0,1;0rad)
  Solid = true
  Symmetric = false
  material = 1
FEATURE [Part::Mirroring] Part__Mirroring  label="Extrude_mirror"
  Base = (0,0,0)
  Normal = (0.83205,0.5547,0)
  Source = -> Extrude
  material = 261
FEATURE [App::Part] Part
  Group = -> [Sketch,Extrude,Part__Mirroring]
  Origin = -> Origin001
FEATURE [App::Part] worldVOL
  Group = -> [GDMLBox_WorldBox,Part]
  Origin = -> Origin
